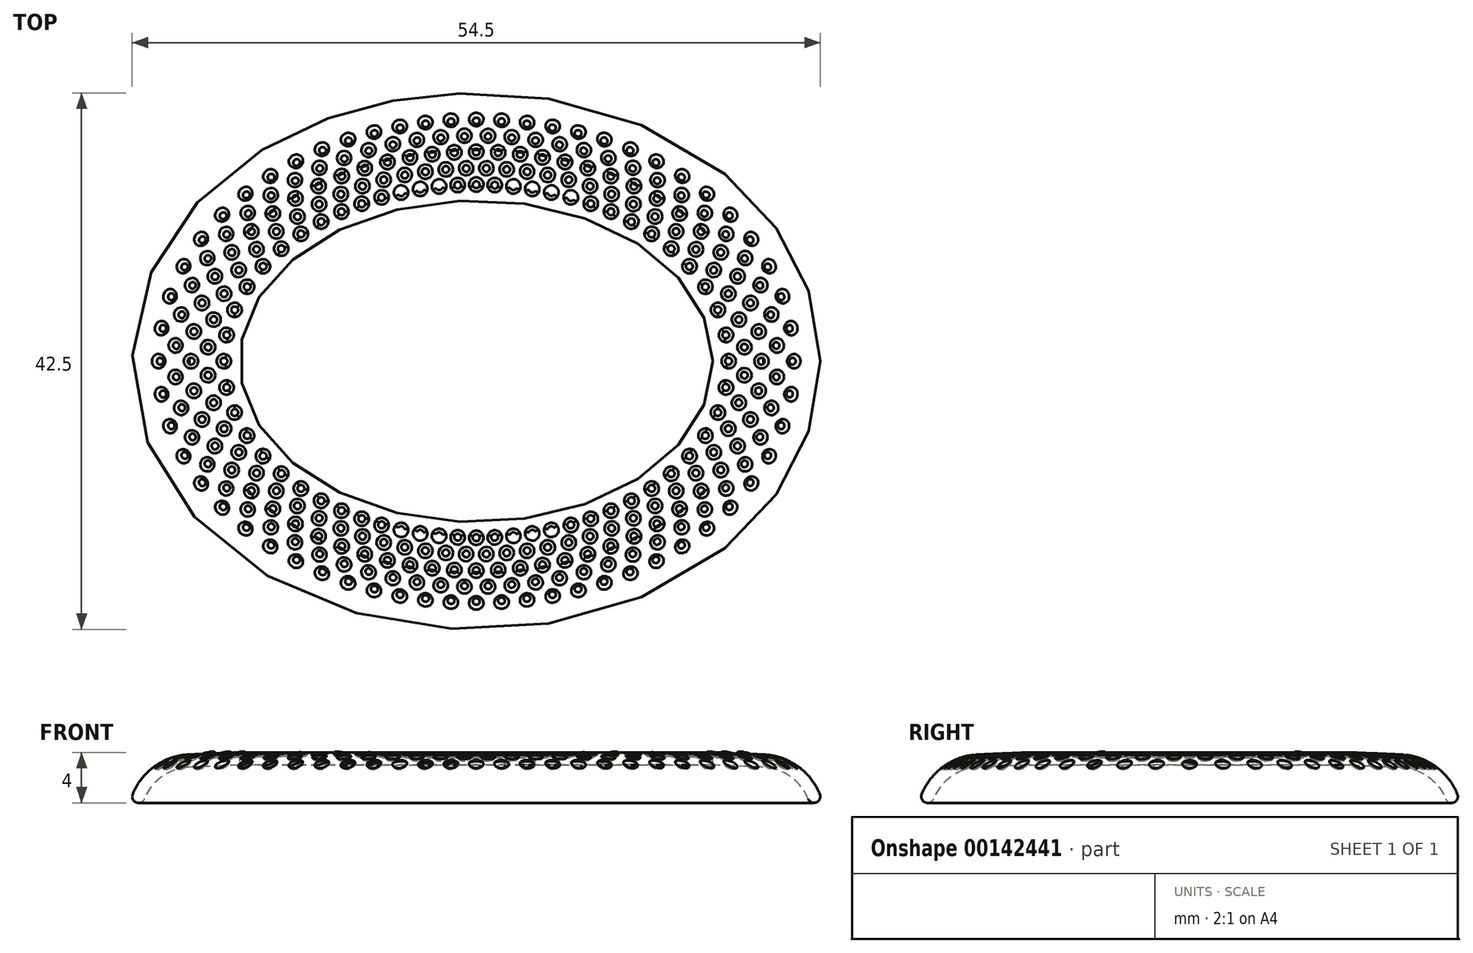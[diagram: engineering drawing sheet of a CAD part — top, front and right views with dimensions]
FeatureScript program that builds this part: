
annotation { "Feature Type Name" : "Feature", "Feature Type Description" : "" }
export const myFeature = defineFeature(function(context is Context, id is Id, definition is map)
    precondition{}
    {
        {
            var Q0;
            Q0=qCreatedBy(makeId("Top.planeOp"),FACE);
            var sketch = newSketch(context, id + "F0", { "sketchPlane" : qUnion([Q0])});
            skEllipse(sketch, "E0", {"center": v(0, 0) * mm, "majorRadius": 12.75 * mm, "minorRadius": 18.75 * mm, "majorAxis": v(0, -1)});
            skFitSpline(sketch, "E1.0", {"points": [v(27.13, -2.49) * mm, v(27.31, 0) * mm, v(27.13, 2.49) * mm, v(26.6, 4.9) * mm, v(25.75, 7.19) * mm, v(24.63, 9.32) * mm, v(23.26, 11.3) * mm, v(21.15, 13.67) * mm, v(18.12, 16.16) * mm, v(14.7, 18.07) * mm, v(11.75, 19.26) * mm, v(8.73, 20.23) * mm, v(5.6, 20.87) * mm, v(2.42, 21.2) * mm, v(0, 21.28) * mm, v(-2.42, 21.2) * mm, v(-5.6, 20.87) * mm, v(-8.73, 20.23) * mm, v(-11.75, 19.26) * mm, v(-14.7, 18.07) * mm, v(-18.12, 16.16) * mm, v(-21.15, 13.67) * mm, v(-23.26, 11.3) * mm, v(-24.63, 9.32) * mm, v(-25.75, 7.19) * mm, v(-26.6, 4.9) * mm, v(-27.13, 2.49) * mm, v(-27.31, 0) * mm, v(-27.13, -2.49) * mm, v(-26.6, -4.9) * mm, v(-25.75, -7.19) * mm, v(-24.63, -9.32) * mm, v(-23.26, -11.3) * mm, v(-21.15, -13.67) * mm, v(-18.12, -16.16) * mm, v(-14.7, -18.07) * mm, v(-11.75, -19.26) * mm, v(-8.73, -20.23) * mm, v(-5.6, -20.87) * mm, v(-2.42, -21.2) * mm, v(0, -21.28) * mm, v(2.42, -21.2) * mm, v(5.6, -20.87) * mm, v(8.73, -20.23) * mm, v(11.75, -19.26) * mm, v(14.7, -18.07) * mm, v(18.12, -16.16) * mm, v(21.15, -13.67) * mm, v(23.26, -11.3) * mm, v(24.63, -9.32) * mm, v(25.75, -7.19) * mm, v(26.6, -4.9) * mm, v(27.13, -2.49) * mm, v(27.31, 0) * mm, v(27.13, 2.49) * mm, v(27.13, -2.49) * mm]});
            skLineSegment(sketch, "E2", {"start": v(18.75, 0) * mm, "end": v(27.25, 0) * mm, "construction": true});
            skSolve(sketch);
        }
        {
            var Q0;
            Q0=qCreatedBy(makeId("Front.planeOp"),FACE);
            var sketch = newSketch(context, id + "F1", { "sketchPlane" : qUnion([Q0])});
            skLineSegment(sketch, "E3", {"start": v(18.75, 0) * mm, "end": v(18.75, -1) * mm, "construction": true});
            skLineSegment(sketch, "E4", {"start": v(18.75, -4) * mm, "end": v(27.25, -4) * mm, "construction": true});
            skLineSegment(sketch, "E5", {"start": v(18.75, 0) * mm, "end": v(22.75, -0.17) * mm});
            skLineSegment(sketch, "E6", {"start": v(18.75, 0) * mm, "end": v(18.75, -1) * mm});
            skArc(sketch, "E7", {"start": v(27.21, -3.31) * mm, "mid": v(25.44, -1.09) * mm, "end": v(22.75, -0.17) * mm});
            skPoint(sketch, "E7.third.point", {"position": v(22.75, -0.17) * mm});
            skArc(sketch, "E8.0", {"start": v(26.29, -3.69) * mm, "mid": v(24.89, -1.91) * mm, "end": v(22.75, -1.18) * mm});
            skLineSegment(sketch, "E8.1", {"start": v(18.75, -1) * mm, "end": v(22.75, -1.18) * mm});
            skLineSegment(sketch, "E9.trimOffspring", {"start": v(18.75, -1.3) * mm, "end": v(18.75, -4) * mm, "construction": true});
            skArc(sketch, "E10", {"start": v(26.29, -3.69) * mm, "mid": v(26.94, -3.96) * mm, "end": v(27.21, -3.31) * mm});
            skLineSegment(sketch, "E11", {"start": v(27.25, -4) * mm, "end": v(27.25, 0) * mm, "construction": true});
            skSolve(sketch);
        }
        {
            var Q0;
            Q0=qCreatedBy(makeId("Top.planeOp"),FACE);
            var sketch = newSketch(context, id + "F2", { "sketchPlane" : qUnion([Q0])});
            skFitSpline(sketch, "E12.0", {"points": [v(19.93, -1.44) * mm, v(20.03, 0) * mm, v(19.93, 1.44) * mm, v(19.52, 3.32) * mm, v(18.71, 5.12) * mm, v(17.55, 6.8) * mm, v(16.15, 8.37) * mm, v(14.04, 10.12) * mm, v(11.52, 11.53) * mm, v(9.28, 12.44) * mm, v(6.93, 13.2) * mm, v(4.47, 13.7) * mm, v(1.93, 13.96) * mm, v(0, 14.02) * mm, v(-1.93, 13.96) * mm, v(-4.47, 13.7) * mm, v(-6.93, 13.2) * mm, v(-9.28, 12.44) * mm, v(-11.52, 11.53) * mm, v(-14.04, 10.12) * mm, v(-16.15, 8.37) * mm, v(-17.55, 6.8) * mm, v(-18.71, 5.12) * mm, v(-19.52, 3.32) * mm, v(-19.93, 1.44) * mm, v(-20.03, 0) * mm, v(-19.93, -1.44) * mm, v(-19.52, -3.32) * mm, v(-18.71, -5.12) * mm, v(-17.55, -6.8) * mm, v(-16.15, -8.37) * mm, v(-14.04, -10.12) * mm, v(-11.52, -11.53) * mm, v(-9.28, -12.44) * mm, v(-6.93, -13.2) * mm, v(-4.47, -13.7) * mm, v(-1.93, -13.96) * mm, v(0, -14.02) * mm, v(1.93, -13.96) * mm, v(4.47, -13.7) * mm, v(6.93, -13.2) * mm, v(9.28, -12.44) * mm, v(11.52, -11.53) * mm, v(14.04, -10.12) * mm, v(16.15, -8.37) * mm, v(17.55, -6.8) * mm, v(18.71, -5.12) * mm, v(19.52, -3.32) * mm, v(19.93, -1.44) * mm, v(20.03, 0) * mm, v(19.93, 1.44) * mm, v(19.93, -1.44) * mm], "construction": true});
            skFitSpline(sketch, "E13.0", {"points": [v(21.22, -1.63) * mm, v(21.34, 0) * mm, v(21.22, 1.63) * mm, v(20.76, 3.75) * mm, v(19.86, 5.75) * mm, v(18.57, 7.6) * mm, v(17.05, 9.32) * mm, v(14.77, 11.2) * mm, v(12.09, 12.7) * mm, v(9.72, 13.66) * mm, v(7.26, 14.45) * mm, v(4.67, 14.99) * mm, v(2.02, 15.25) * mm, v(0, 15.32) * mm, v(-2.02, 15.25) * mm, v(-4.67, 14.99) * mm, v(-7.26, 14.45) * mm, v(-9.72, 13.66) * mm, v(-12.09, 12.7) * mm, v(-14.77, 11.2) * mm, v(-17.05, 9.32) * mm, v(-18.57, 7.6) * mm, v(-19.86, 5.75) * mm, v(-20.76, 3.75) * mm, v(-21.22, 1.63) * mm, v(-21.34, 0) * mm, v(-21.22, -1.63) * mm, v(-20.76, -3.75) * mm, v(-19.86, -5.75) * mm, v(-18.57, -7.6) * mm, v(-17.05, -9.32) * mm, v(-14.77, -11.2) * mm, v(-12.09, -12.7) * mm, v(-9.72, -13.66) * mm, v(-7.26, -14.45) * mm, v(-4.67, -14.99) * mm, v(-2.02, -15.25) * mm, v(0, -15.32) * mm, v(2.02, -15.25) * mm, v(4.67, -14.99) * mm, v(7.26, -14.45) * mm, v(9.72, -13.66) * mm, v(12.09, -12.7) * mm, v(14.77, -11.2) * mm, v(17.05, -9.32) * mm, v(18.57, -7.6) * mm, v(19.86, -5.75) * mm, v(20.76, -3.75) * mm, v(21.22, -1.63) * mm, v(21.34, 0) * mm, v(21.22, 1.63) * mm, v(21.22, -1.63) * mm], "construction": true});
            skFitSpline(sketch, "E14.0", {"points": [v(22.51, -1.81) * mm, v(22.64, 0) * mm, v(22.51, 1.81) * mm, v(22, 4.17) * mm, v(21, 6.4) * mm, v(19.6, 8.4) * mm, v(17.95, 10.27) * mm, v(15.5, 12.28) * mm, v(12.65, 13.87) * mm, v(10.16, 14.89) * mm, v(7.58, 15.72) * mm, v(4.88, 16.27) * mm, v(2.1, 16.55) * mm, v(0, 16.62) * mm, v(-2.1, 16.55) * mm, v(-4.88, 16.27) * mm, v(-7.58, 15.72) * mm, v(-10.16, 14.89) * mm, v(-12.65, 13.87) * mm, v(-15.5, 12.28) * mm, v(-17.95, 10.27) * mm, v(-19.6, 8.4) * mm, v(-21, 6.4) * mm, v(-22, 4.17) * mm, v(-22.51, 1.81) * mm, v(-22.64, 0) * mm, v(-22.51, -1.81) * mm, v(-22, -4.17) * mm, v(-21, -6.4) * mm, v(-19.6, -8.4) * mm, v(-17.95, -10.27) * mm, v(-15.5, -12.28) * mm, v(-12.65, -13.87) * mm, v(-10.16, -14.89) * mm, v(-7.58, -15.72) * mm, v(-4.88, -16.27) * mm, v(-2.1, -16.55) * mm, v(0, -16.62) * mm, v(2.1, -16.55) * mm, v(4.88, -16.27) * mm, v(7.58, -15.72) * mm, v(10.16, -14.89) * mm, v(12.65, -13.87) * mm, v(15.5, -12.28) * mm, v(17.95, -10.27) * mm, v(19.6, -8.4) * mm, v(21, -6.4) * mm, v(22, -4.17) * mm, v(22.51, -1.81) * mm, v(22.64, 0) * mm, v(22.51, 1.81) * mm, v(22.51, -1.81) * mm], "construction": true});
            skFitSpline(sketch, "E15.0", {"points": [v(23.8, -2) * mm, v(23.95, 0) * mm, v(23.8, 2) * mm, v(23.23, 4.6) * mm, v(22.14, 7.03) * mm, v(20.62, 9.21) * mm, v(18.84, 11.22) * mm, v(16.24, 13.37) * mm, v(13.22, 15.04) * mm, v(10.6, 16.11) * mm, v(7.9, 16.98) * mm, v(5.08, 17.56) * mm, v(2.2, 17.85) * mm, v(0, 17.92) * mm, v(-2.2, 17.85) * mm, v(-5.08, 17.56) * mm, v(-7.9, 16.98) * mm, v(-10.6, 16.11) * mm, v(-13.22, 15.04) * mm, v(-16.24, 13.37) * mm, v(-18.84, 11.22) * mm, v(-20.62, 9.21) * mm, v(-22.14, 7.03) * mm, v(-23.23, 4.6) * mm, v(-23.8, 2) * mm, v(-23.95, 0) * mm, v(-23.8, -2) * mm, v(-23.23, -4.6) * mm, v(-22.14, -7.03) * mm, v(-20.62, -9.21) * mm, v(-18.84, -11.22) * mm, v(-16.24, -13.37) * mm, v(-13.22, -15.04) * mm, v(-10.6, -16.11) * mm, v(-7.9, -16.98) * mm, v(-5.08, -17.56) * mm, v(-2.2, -17.85) * mm, v(0, -17.92) * mm, v(2.2, -17.85) * mm, v(5.08, -17.56) * mm, v(7.9, -16.98) * mm, v(10.6, -16.11) * mm, v(13.22, -15.04) * mm, v(16.24, -13.37) * mm, v(18.84, -11.22) * mm, v(20.62, -9.21) * mm, v(22.14, -7.03) * mm, v(23.23, -4.6) * mm, v(23.8, -2) * mm, v(23.95, 0) * mm, v(23.8, 2) * mm, v(23.8, -2) * mm], "construction": true});
            skFitSpline(sketch, "E16.0", {"points": [v(25.1, -2.2) * mm, v(25.25, 0) * mm, v(25.1, 2.2) * mm, v(24.47, 5.03) * mm, v(22.99, 8.32) * mm, v(20.3, 11.72) * mm, v(16.97, 14.45) * mm, v(13.8, 16.22) * mm, v(11.05, 17.33) * mm, v(8.22, 18.24) * mm, v(5.28, 18.85) * mm, v(2.28, 19.15) * mm, v(0, 19.23) * mm, v(-2.28, 19.15) * mm, v(-5.28, 18.85) * mm, v(-8.22, 18.24) * mm, v(-11.05, 17.33) * mm, v(-13.8, 16.22) * mm, v(-16.97, 14.45) * mm, v(-20.3, 11.72) * mm, v(-22.99, 8.32) * mm, v(-24.47, 5.03) * mm, v(-25.1, 2.2) * mm, v(-25.25, 0) * mm, v(-25.1, -2.2) * mm, v(-24.47, -5.03) * mm, v(-22.99, -8.32) * mm, v(-20.3, -11.72) * mm, v(-16.97, -14.45) * mm, v(-13.8, -16.22) * mm, v(-11.05, -17.33) * mm, v(-8.22, -18.24) * mm, v(-5.28, -18.85) * mm, v(-2.28, -19.15) * mm, v(0, -19.23) * mm, v(2.28, -19.15) * mm, v(5.28, -18.85) * mm, v(8.22, -18.24) * mm, v(11.05, -17.33) * mm, v(13.8, -16.22) * mm, v(16.97, -14.45) * mm, v(20.3, -11.72) * mm, v(22.99, -8.32) * mm, v(24.47, -5.03) * mm, v(25.1, -2.2) * mm, v(25.25, 0) * mm, v(25.1, 2.2) * mm, v(25.1, -2.2) * mm], "construction": true});
            skCircle(sketch, "E17", {"center": v(0, 14) * mm, "radius": 0.57 * mm});
            skCircle(sketch, "E18", {"center": v(0, 16.6) * mm, "radius": 0.57 * mm});
            skCircle(sketch, "E19", {"center": v(0, 19.2) * mm, "radius": 0.57 * mm});
            skLineSegment(sketch, "E20", {"start": v(0, 0) * mm, "end": v(0, 14) * mm, "construction": true});
            skLineSegment(sketch, "E21", {"start": v(0, 14) * mm, "end": v(0, 16.6) * mm, "construction": true});
            skLineSegment(sketch, "E22", {"start": v(0, 16.6) * mm, "end": v(0, 19.2) * mm, "construction": true});
            skLineSegment(sketch, "E23", {"start": v(0, 0) * mm, "end": v(0.8, 15.29) * mm, "construction": true});
            skLineSegment(sketch, "E24", {"start": v(0.8, 15.29) * mm, "end": v(0.94, 17.89) * mm, "construction": true});
            skCircle(sketch, "E25", {"center": v(0.94, 17.89) * mm, "radius": 0.57 * mm});
            skCircle(sketch, "E26", {"center": v(0.8, 15.29) * mm, "radius": 0.57 * mm});
            skLineSegment(sketch, "E27", {"start": v(0, 0) * mm, "end": v(1.47, 13.96) * mm, "construction": true});
            skLineSegment(sketch, "E28", {"start": v(1.47, 13.96) * mm, "end": v(1.74, 16.55) * mm, "construction": true});
            skLineSegment(sketch, "E29", {"start": v(1.74, 16.55) * mm, "end": v(2.01, 19.14) * mm, "construction": true});
            skLineSegment(sketch, "E30", {"start": v(0, 0) * mm, "end": v(2.4, 15.2) * mm, "construction": true});
            skLineSegment(sketch, "E31", {"start": v(2.4, 15.2) * mm, "end": v(2.82, 17.78) * mm, "construction": true});
            skLineSegment(sketch, "E32", {"start": v(0, 0) * mm, "end": v(2.94, 13.85) * mm, "construction": true});
            skLineSegment(sketch, "E33", {"start": v(2.94, 13.85) * mm, "end": v(3.49, 16.4) * mm, "construction": true});
            skLineSegment(sketch, "E34", {"start": v(3.49, 16.4) * mm, "end": v(4.03, 18.96) * mm, "construction": true});
            skLineSegment(sketch, "E35", {"start": v(0, 0) * mm, "end": v(4.03, 15.03) * mm, "construction": true});
            skLineSegment(sketch, "E36", {"start": v(4.03, 15.03) * mm, "end": v(4.7, 17.56) * mm, "construction": true});
            skLineSegment(sketch, "E37", {"start": v(0, 0) * mm, "end": v(4.44, 13.65) * mm, "construction": true});
            skLineSegment(sketch, "E38", {"start": v(4.44, 13.65) * mm, "end": v(5.25, 16.16) * mm, "construction": true});
            skLineSegment(sketch, "E39", {"start": v(5.25, 16.16) * mm, "end": v(6.06, 18.65) * mm, "construction": true});
            skLineSegment(sketch, "E40", {"start": v(0, 0) * mm, "end": v(5.66, 14.76) * mm, "construction": true});
            skLineSegment(sketch, "E41", {"start": v(5.66, 14.76) * mm, "end": v(6.6, 17.22) * mm, "construction": true});
            skLineSegment(sketch, "E42", {"start": v(0, 0) * mm, "end": v(5.95, 13.37) * mm, "construction": true});
            skLineSegment(sketch, "E43", {"start": v(5.95, 13.37) * mm, "end": v(7.03, 15.8) * mm, "construction": true});
            skLineSegment(sketch, "E44", {"start": v(7.03, 15.8) * mm, "end": v(8.1, 18.2) * mm, "construction": true});
            skLineSegment(sketch, "E45", {"start": v(0, 0) * mm, "end": v(7.33, 14.38) * mm, "construction": true});
            skLineSegment(sketch, "E46", {"start": v(7.33, 14.38) * mm, "end": v(8.53, 16.75) * mm, "construction": true});
            skLineSegment(sketch, "E47", {"start": v(0, 0) * mm, "end": v(7.5, 12.99) * mm, "construction": true});
            skLineSegment(sketch, "E48", {"start": v(7.5, 12.99) * mm, "end": v(8.84, 15.3) * mm, "construction": true});
            skLineSegment(sketch, "E49", {"start": v(8.84, 15.3) * mm, "end": v(10.17, 17.6) * mm, "construction": true});
            skLineSegment(sketch, "E50", {"start": v(0, 0) * mm, "end": v(9.02, 13.88) * mm, "construction": true});
            skLineSegment(sketch, "E51", {"start": v(9.02, 13.88) * mm, "end": v(10.47, 16.13) * mm, "construction": true});
            skLineSegment(sketch, "E52", {"start": v(0, 0) * mm, "end": v(9.07, 12.49) * mm, "construction": true});
            skLineSegment(sketch, "E53", {"start": v(9.07, 12.49) * mm, "end": v(10.66, 14.67) * mm, "construction": true});
            skLineSegment(sketch, "E54", {"start": v(10.66, 14.67) * mm, "end": v(12.24, 16.84) * mm, "construction": true});
            skLineSegment(sketch, "E55", {"start": v(0, 0) * mm, "end": v(10.73, 13.25) * mm, "construction": true});
            skLineSegment(sketch, "E56", {"start": v(10.73, 13.25) * mm, "end": v(12.43, 15.34) * mm, "construction": true});
            skLineSegment(sketch, "E57", {"start": v(0, 0) * mm, "end": v(10.67, 11.86) * mm, "construction": true});
            skLineSegment(sketch, "E58", {"start": v(10.67, 11.86) * mm, "end": v(12.5, 13.88) * mm, "construction": true});
            skLineSegment(sketch, "E59", {"start": v(12.5, 13.88) * mm, "end": v(14.3, 15.88) * mm, "construction": true});
            skLineSegment(sketch, "E60", {"start": v(0, 0) * mm, "end": v(12.45, 12.45) * mm, "construction": true});
            skLineSegment(sketch, "E61", {"start": v(12.45, 12.45) * mm, "end": v(14.37, 14.37) * mm, "construction": true});
            skLineSegment(sketch, "E62", {"start": v(0, 0) * mm, "end": v(12.29, 11.07) * mm, "construction": true});
            skLineSegment(sketch, "E63", {"start": v(12.29, 11.07) * mm, "end": v(14.33, 12.9) * mm, "construction": true});
            skLineSegment(sketch, "E64", {"start": v(14.33, 12.9) * mm, "end": v(16.34, 14.71) * mm, "construction": true});
            skLineSegment(sketch, "E65", {"start": v(0, 0) * mm, "end": v(14.17, 11.47) * mm, "construction": true});
            skLineSegment(sketch, "E66", {"start": v(14.17, 11.47) * mm, "end": v(16.28, 13.19) * mm, "construction": true});
            skLineSegment(sketch, "E67", {"start": v(0, 0) * mm, "end": v(13.9, 10.1) * mm, "construction": true});
            skLineSegment(sketch, "E68", {"start": v(13.9, 10.1) * mm, "end": v(16.11, 11.7) * mm, "construction": true});
            skLineSegment(sketch, "E69", {"start": v(16.11, 11.7) * mm, "end": v(18.3, 13.3) * mm, "construction": true});
            skLineSegment(sketch, "E70", {"start": v(0, 0) * mm, "end": v(15.84, 10.28) * mm, "construction": true});
            skLineSegment(sketch, "E71", {"start": v(15.84, 10.28) * mm, "end": v(18.12, 11.77) * mm, "construction": true});
            skLineSegment(sketch, "E72", {"start": v(0, 0) * mm, "end": v(15.45, 8.92) * mm, "construction": true});
            skLineSegment(sketch, "E73", {"start": v(15.45, 8.92) * mm, "end": v(17.82, 10.29) * mm, "construction": true});
            skLineSegment(sketch, "E74", {"start": v(17.82, 10.29) * mm, "end": v(20.16, 11.64) * mm, "construction": true});
            skLineSegment(sketch, "E75", {"start": v(0, 0) * mm, "end": v(17.4, 8.87) * mm, "construction": true});
            skLineSegment(sketch, "E76", {"start": v(17.4, 8.87) * mm, "end": v(19.82, 10.1) * mm, "construction": true});
            skLineSegment(sketch, "E77", {"start": v(0, 0) * mm, "end": v(16.9, 7.52) * mm, "construction": true});
            skLineSegment(sketch, "E78", {"start": v(16.9, 7.52) * mm, "end": v(19.37, 8.63) * mm, "construction": true});
            skLineSegment(sketch, "E79", {"start": v(19.37, 8.63) * mm, "end": v(21.82, 9.72) * mm, "construction": true});
            skLineSegment(sketch, "E80", {"start": v(0, 0) * mm, "end": v(18.82, 7.22) * mm, "construction": true});
            skLineSegment(sketch, "E81", {"start": v(18.82, 7.22) * mm, "end": v(21.32, 8.18) * mm, "construction": true});
            skLineSegment(sketch, "E82", {"start": v(0, 0) * mm, "end": v(18.16, 5.9) * mm, "construction": true});
            skLineSegment(sketch, "E83", {"start": v(18.16, 5.9) * mm, "end": v(20.7, 6.73) * mm, "construction": true});
            skLineSegment(sketch, "E84", {"start": v(20.7, 6.73) * mm, "end": v(23.23, 7.55) * mm, "construction": true});
            skLineSegment(sketch, "E85", {"start": v(0, 0) * mm, "end": v(19.98, 5.35) * mm, "construction": true});
            skLineSegment(sketch, "E86", {"start": v(19.98, 5.35) * mm, "end": v(22.54, 6.04) * mm, "construction": true});
            skLineSegment(sketch, "E87", {"start": v(0, 0) * mm, "end": v(19.15, 4.07) * mm, "construction": true});
            skLineSegment(sketch, "E88", {"start": v(19.15, 4.07) * mm, "end": v(21.73, 4.62) * mm, "construction": true});
            skLineSegment(sketch, "E89", {"start": v(21.73, 4.62) * mm, "end": v(24.3, 5.16) * mm, "construction": true});
            skLineSegment(sketch, "E90", {"start": v(0, 0) * mm, "end": v(20.8, 3.3) * mm, "construction": true});
            skLineSegment(sketch, "E91", {"start": v(20.8, 3.3) * mm, "end": v(23.4, 3.7) * mm, "construction": true});
            skLineSegment(sketch, "E92", {"start": v(0, 0) * mm, "end": v(19.78, 2.08) * mm, "construction": true});
            skLineSegment(sketch, "E93", {"start": v(19.78, 2.08) * mm, "end": v(22.38, 2.35) * mm, "construction": true});
            skLineSegment(sketch, "E94", {"start": v(22.38, 2.35) * mm, "end": v(24.97, 2.62) * mm, "construction": true});
            skLineSegment(sketch, "E95", {"start": v(0, 0) * mm, "end": v(21.24, 1.11) * mm, "construction": true});
            skLineSegment(sketch, "E96", {"start": v(21.24, 1.11) * mm, "end": v(23.84, 1.25) * mm, "construction": true});
            skLineSegment(sketch, "E97", {"start": v(0, 0) * mm, "end": v(20, 0) * mm, "construction": true});
            skLineSegment(sketch, "E98", {"start": v(20, 0) * mm, "end": v(22.6, 0) * mm, "construction": true});
            skLineSegment(sketch, "E99", {"start": v(22.6, 0) * mm, "end": v(25.2, 0) * mm, "construction": true});
            skCircle(sketch, "E100", {"center": v(2.01, 19.14) * mm, "radius": 0.57 * mm});
            skCircle(sketch, "E101", {"center": v(4.03, 18.96) * mm, "radius": 0.57 * mm});
            skCircle(sketch, "E102", {"center": v(6.06, 18.65) * mm, "radius": 0.57 * mm});
            skCircle(sketch, "E103", {"center": v(8.1, 18.2) * mm, "radius": 0.57 * mm});
            skCircle(sketch, "E104", {"center": v(10.17, 17.6) * mm, "radius": 0.57 * mm});
            skCircle(sketch, "E105", {"center": v(12.24, 16.84) * mm, "radius": 0.57 * mm});
            skCircle(sketch, "E106", {"center": v(14.3, 15.88) * mm, "radius": 0.57 * mm});
            skCircle(sketch, "E107", {"center": v(16.34, 14.71) * mm, "radius": 0.57 * mm});
            skCircle(sketch, "E108", {"center": v(18.3, 13.3) * mm, "radius": 0.57 * mm});
            skCircle(sketch, "E109", {"center": v(20.16, 11.64) * mm, "radius": 0.57 * mm});
            skCircle(sketch, "E110", {"center": v(21.82, 9.72) * mm, "radius": 0.57 * mm});
            skCircle(sketch, "E111", {"center": v(23.23, 7.55) * mm, "radius": 0.57 * mm});
            skCircle(sketch, "E112", {"center": v(24.3, 5.16) * mm, "radius": 0.57 * mm});
            skCircle(sketch, "E113", {"center": v(24.97, 2.62) * mm, "radius": 0.57 * mm});
            skCircle(sketch, "E114", {"center": v(25.2, 0) * mm, "radius": 0.57 * mm});
            skCircle(sketch, "E115", {"center": v(22.6, 0) * mm, "radius": 0.57 * mm});
            skCircle(sketch, "E116", {"center": v(20, 0) * mm, "radius": 0.57 * mm});
            skCircle(sketch, "E117", {"center": v(22.38, 2.35) * mm, "radius": 0.57 * mm});
            skCircle(sketch, "E118", {"center": v(19.78, 2.08) * mm, "radius": 0.57 * mm});
            skCircle(sketch, "E119", {"center": v(19.15, 4.07) * mm, "radius": 0.57 * mm});
            skCircle(sketch, "E120", {"center": v(21.73, 4.62) * mm, "radius": 0.57 * mm});
            skCircle(sketch, "E121", {"center": v(20.7, 6.73) * mm, "radius": 0.57 * mm});
            skCircle(sketch, "E122", {"center": v(18.16, 5.9) * mm, "radius": 0.57 * mm});
            skCircle(sketch, "E123", {"center": v(19.37, 8.63) * mm, "radius": 0.57 * mm});
            skCircle(sketch, "E124", {"center": v(16.9, 7.52) * mm, "radius": 0.57 * mm});
            skCircle(sketch, "E125", {"center": v(17.82, 10.29) * mm, "radius": 0.57 * mm});
            skCircle(sketch, "E126", {"center": v(15.45, 8.92) * mm, "radius": 0.57 * mm});
            skCircle(sketch, "E127", {"center": v(16.11, 11.7) * mm, "radius": 0.57 * mm});
            skCircle(sketch, "E128", {"center": v(13.9, 10.1) * mm, "radius": 0.57 * mm});
            skCircle(sketch, "E129", {"center": v(14.33, 12.9) * mm, "radius": 0.57 * mm});
            skCircle(sketch, "E130", {"center": v(12.29, 11.07) * mm, "radius": 0.57 * mm});
            skCircle(sketch, "E131", {"center": v(12.5, 13.88) * mm, "radius": 0.57 * mm});
            skCircle(sketch, "E132", {"center": v(10.67, 11.86) * mm, "radius": 0.57 * mm});
            skCircle(sketch, "E133", {"center": v(9.07, 12.49) * mm, "radius": 0.57 * mm});
            skCircle(sketch, "E134", {"center": v(10.66, 14.67) * mm, "radius": 0.57 * mm});
            skCircle(sketch, "E135", {"center": v(8.84, 15.3) * mm, "radius": 0.57 * mm});
            skCircle(sketch, "E136", {"center": v(7.03, 15.8) * mm, "radius": 0.57 * mm});
            skCircle(sketch, "E137", {"center": v(7.5, 12.99) * mm, "radius": 0.57 * mm});
            skCircle(sketch, "E138", {"center": v(5.95, 13.37) * mm, "radius": 0.57 * mm});
            skCircle(sketch, "E139", {"center": v(4.44, 13.65) * mm, "radius": 0.57 * mm});
            skCircle(sketch, "E140", {"center": v(2.94, 13.85) * mm, "radius": 0.57 * mm});
            skCircle(sketch, "E141", {"center": v(1.47, 13.96) * mm, "radius": 0.57 * mm});
            skCircle(sketch, "E142", {"center": v(1.74, 16.55) * mm, "radius": 0.57 * mm});
            skCircle(sketch, "E143", {"center": v(3.49, 16.4) * mm, "radius": 0.57 * mm});
            skCircle(sketch, "E144", {"center": v(5.25, 16.16) * mm, "radius": 0.57 * mm});
            skCircle(sketch, "E145", {"center": v(2.82, 17.78) * mm, "radius": 0.57 * mm});
            skCircle(sketch, "E146", {"center": v(4.7, 17.56) * mm, "radius": 0.57 * mm});
            skCircle(sketch, "E147", {"center": v(6.6, 17.22) * mm, "radius": 0.57 * mm});
            skCircle(sketch, "E148", {"center": v(8.53, 16.75) * mm, "radius": 0.57 * mm});
            skCircle(sketch, "E149", {"center": v(10.47, 16.13) * mm, "radius": 0.57 * mm});
            skCircle(sketch, "E150", {"center": v(12.43, 15.34) * mm, "radius": 0.57 * mm});
            skCircle(sketch, "E151", {"center": v(14.37, 14.37) * mm, "radius": 0.57 * mm});
            skCircle(sketch, "E152", {"center": v(16.28, 13.19) * mm, "radius": 0.57 * mm});
            skCircle(sketch, "E153", {"center": v(18.12, 11.77) * mm, "radius": 0.57 * mm});
            skCircle(sketch, "E154", {"center": v(19.82, 10.1) * mm, "radius": 0.57 * mm});
            skCircle(sketch, "E155", {"center": v(21.32, 8.18) * mm, "radius": 0.57 * mm});
            skCircle(sketch, "E156", {"center": v(22.54, 6.04) * mm, "radius": 0.57 * mm});
            skCircle(sketch, "E157", {"center": v(23.4, 3.7) * mm, "radius": 0.57 * mm});
            skCircle(sketch, "E158", {"center": v(23.84, 1.25) * mm, "radius": 0.57 * mm});
            skCircle(sketch, "E159", {"center": v(2.4, 15.2) * mm, "radius": 0.57 * mm});
            skCircle(sketch, "E160", {"center": v(4.03, 15.03) * mm, "radius": 0.57 * mm});
            skCircle(sketch, "E161", {"center": v(5.66, 14.76) * mm, "radius": 0.57 * mm});
            skCircle(sketch, "E162", {"center": v(7.33, 14.38) * mm, "radius": 0.57 * mm});
            skCircle(sketch, "E163", {"center": v(9.02, 13.88) * mm, "radius": 0.57 * mm});
            skCircle(sketch, "E164", {"center": v(10.73, 13.25) * mm, "radius": 0.57 * mm});
            skCircle(sketch, "E165", {"center": v(12.45, 12.45) * mm, "radius": 0.57 * mm});
            skCircle(sketch, "E166", {"center": v(14.17, 11.47) * mm, "radius": 0.57 * mm});
            skCircle(sketch, "E167", {"center": v(15.84, 10.28) * mm, "radius": 0.57 * mm});
            skCircle(sketch, "E168", {"center": v(17.4, 8.87) * mm, "radius": 0.57 * mm});
            skCircle(sketch, "E169", {"center": v(18.82, 7.22) * mm, "radius": 0.57 * mm});
            skCircle(sketch, "E170", {"center": v(19.98, 5.35) * mm, "radius": 0.57 * mm});
            skCircle(sketch, "E171", {"center": v(20.8, 3.3) * mm, "radius": 0.57 * mm});
            skCircle(sketch, "E172", {"center": v(21.24, 1.11) * mm, "radius": 0.57 * mm});
            skCircle(sketch, "E173.MirrorC", {"center": v(-10.66, 14.67) * mm, "radius": 0.57 * mm});
            skCircle(sketch, "E174.MirrorC", {"center": v(-12.43, 15.34) * mm, "radius": 0.57 * mm});
            skLineSegment(sketch, "E175.MirrorCS", {"start": v(0, 0) * mm, "end": v(-1.47, 13.96) * mm, "construction": true});
            skCircle(sketch, "E176.MirrorC", {"center": v(-14.17, 11.47) * mm, "radius": 0.57 * mm});
            skLineSegment(sketch, "E177.MirrorCS", {"start": v(-19.98, 5.35) * mm, "end": v(-22.54, 6.04) * mm, "construction": true});
            skLineSegment(sketch, "E178.MirrorCS", {"start": v(0, 0) * mm, "end": v(-15.84, 10.28) * mm, "construction": true});
            skCircle(sketch, "E179.MirrorC", {"center": v(-0.8, 15.29) * mm, "radius": 0.57 * mm});
            skCircle(sketch, "E180.MirrorC", {"center": v(-6.06, 18.65) * mm, "radius": 0.57 * mm});
            skCircle(sketch, "E181.MirrorC", {"center": v(-19.78, 2.08) * mm, "radius": 0.57 * mm});
            skCircle(sketch, "E182.MirrorC", {"center": v(-0.94, 17.89) * mm, "radius": 0.57 * mm});
            skLineSegment(sketch, "E183.MirrorCS", {"start": v(-4.44, 13.65) * mm, "end": v(-5.25, 16.16) * mm, "construction": true});
            skLineSegment(sketch, "E184.MirrorCS", {"start": v(-10.66, 14.67) * mm, "end": v(-12.24, 16.84) * mm, "construction": true});
            skCircle(sketch, "E185.MirrorC", {"center": v(-9.07, 12.49) * mm, "radius": 0.57 * mm});
            skCircle(sketch, "E186.MirrorC", {"center": v(-10.47, 16.13) * mm, "radius": 0.57 * mm});
            skCircle(sketch, "E187.MirrorC", {"center": v(-12.45, 12.45) * mm, "radius": 0.57 * mm});
            skLineSegment(sketch, "E188.MirrorCS", {"start": v(-16.11, 11.7) * mm, "end": v(-18.3, 13.3) * mm, "construction": true});
            skLineSegment(sketch, "E189.MirrorCS", {"start": v(0, 0) * mm, "end": v(-19.98, 5.35) * mm, "construction": true});
            skCircle(sketch, "E190.MirrorC", {"center": v(-4.03, 18.96) * mm, "radius": 0.57 * mm});
            skLineSegment(sketch, "E191.MirrorCS", {"start": v(0, 0) * mm, "end": v(-10.67, 11.86) * mm, "construction": true});
            skCircle(sketch, "E192.MirrorC", {"center": v(-22.38, 2.35) * mm, "radius": 0.57 * mm});
            skLineSegment(sketch, "E193.MirrorCS", {"start": v(0, 0) * mm, "end": v(-4.44, 13.65) * mm, "construction": true});
            skLineSegment(sketch, "E194.MirrorCS", {"start": v(-9.07, 12.49) * mm, "end": v(-10.66, 14.67) * mm, "construction": true});
            skCircle(sketch, "E195.MirrorC", {"center": v(-2.01, 19.14) * mm, "radius": 0.57 * mm});
            skLineSegment(sketch, "E196.MirrorCS", {"start": v(0, 0) * mm, "end": v(-15.45, 8.92) * mm, "construction": true});
            skLineSegment(sketch, "E197.MirrorCS", {"start": v(0, 0) * mm, "end": v(-5.95, 13.37) * mm, "construction": true});
            skCircle(sketch, "E198.MirrorC", {"center": v(-5.95, 13.37) * mm, "radius": 0.57 * mm});
            skCircle(sketch, "E199.MirrorC", {"center": v(-10.67, 11.86) * mm, "radius": 0.57 * mm});
            skLineSegment(sketch, "E200.MirrorCS", {"start": v(-21.24, 1.11) * mm, "end": v(-23.84, 1.25) * mm, "construction": true});
            skCircle(sketch, "E201.MirrorC", {"center": v(-4.03, 15.03) * mm, "radius": 0.57 * mm});
            skCircle(sketch, "E202.MirrorC", {"center": v(-24.3, 5.16) * mm, "radius": 0.57 * mm});
            skCircle(sketch, "E203.MirrorC", {"center": v(-13.9, 10.1) * mm, "radius": 0.57 * mm});
            skCircle(sketch, "E204.MirrorC", {"center": v(-5.25, 16.16) * mm, "radius": 0.57 * mm});
            skLineSegment(sketch, "E205.MirrorCS", {"start": v(0, 0) * mm, "end": v(-2.94, 13.85) * mm, "construction": true});
            skLineSegment(sketch, "E206.MirrorCS", {"start": v(-7.5, 12.99) * mm, "end": v(-8.84, 15.3) * mm, "construction": true});
            skLineSegment(sketch, "E207.MirrorCS", {"start": v(-14.33, 12.9) * mm, "end": v(-16.34, 14.71) * mm, "construction": true});
            skLineSegment(sketch, "E208.MirrorCS", {"start": v(0, 0) * mm, "end": v(-18.82, 7.22) * mm, "construction": true});
            skLineSegment(sketch, "E209.MirrorCS", {"start": v(-19.15, 4.07) * mm, "end": v(-21.73, 4.62) * mm, "construction": true});
            skLineSegment(sketch, "E210.MirrorCS", {"start": v(0, 0) * mm, "end": v(-0.8, 15.29) * mm, "construction": true});
            skCircle(sketch, "E211.MirrorC", {"center": v(-10.73, 13.25) * mm, "radius": 0.57 * mm});
            skCircle(sketch, "E212.MirrorC", {"center": v(-8.53, 16.75) * mm, "radius": 0.57 * mm});
            skLineSegment(sketch, "E213.MirrorCS", {"start": v(-13.9, 10.1) * mm, "end": v(-16.11, 11.7) * mm, "construction": true});
            skLineSegment(sketch, "E214.MirrorCS", {"start": v(-20.7, 6.73) * mm, "end": v(-23.23, 7.55) * mm, "construction": true});
            skLineSegment(sketch, "E215.MirrorCS", {"start": v(-18.82, 7.22) * mm, "end": v(-21.32, 8.18) * mm, "construction": true});
            skLineSegment(sketch, "E216.MirrorCS", {"start": v(0, 0) * mm, "end": v(-14.17, 11.47) * mm, "construction": true});
            skLineSegment(sketch, "E217.MirrorCS", {"start": v(-0.8, 15.29) * mm, "end": v(-0.94, 17.89) * mm, "construction": true});
            skCircle(sketch, "E218.MirrorC", {"center": v(-7.03, 15.8) * mm, "radius": 0.57 * mm});
            skLineSegment(sketch, "E219.MirrorCS", {"start": v(-4.03, 15.03) * mm, "end": v(-4.7, 17.56) * mm, "construction": true});
            skLineSegment(sketch, "E220.MirrorCS", {"start": v(0, 0) * mm, "end": v(-9.07, 12.49) * mm, "construction": true});
            skCircle(sketch, "E221.MirrorC", {"center": v(-20, 0) * mm, "radius": 0.57 * mm});
            skLineSegment(sketch, "E222.MirrorCS", {"start": v(-8.84, 15.3) * mm, "end": v(-10.17, 17.6) * mm, "construction": true});
            skLineSegment(sketch, "E223.MirrorCS", {"start": v(-2.94, 13.85) * mm, "end": v(-3.49, 16.4) * mm, "construction": true});
            skCircle(sketch, "E224.MirrorC", {"center": v(-2.82, 17.78) * mm, "radius": 0.57 * mm});
            skLineSegment(sketch, "E225.MirrorCS", {"start": v(-9.02, 13.88) * mm, "end": v(-10.47, 16.13) * mm, "construction": true});
            skCircle(sketch, "E226.MirrorC", {"center": v(-12.5, 13.88) * mm, "radius": 0.57 * mm});
            skCircle(sketch, "E227.MirrorC", {"center": v(-24.97, 2.62) * mm, "radius": 0.57 * mm});
            skLineSegment(sketch, "E228.MirrorCS", {"start": v(0, 0) * mm, "end": v(-20, 0) * mm, "construction": true});
            skCircle(sketch, "E229.MirrorC", {"center": v(-14.33, 12.9) * mm, "radius": 0.57 * mm});
            skCircle(sketch, "E230.MirrorC", {"center": v(-6.6, 17.22) * mm, "radius": 0.57 * mm});
            skCircle(sketch, "E231.MirrorC", {"center": v(-9.02, 13.88) * mm, "radius": 0.57 * mm});
            skLineSegment(sketch, "E232.MirrorCS", {"start": v(-19.78, 2.08) * mm, "end": v(-22.38, 2.35) * mm, "construction": true});
            skCircle(sketch, "E233.MirrorC", {"center": v(-5.66, 14.76) * mm, "radius": 0.57 * mm});
            skCircle(sketch, "E234.MirrorC", {"center": v(-10.17, 17.6) * mm, "radius": 0.57 * mm});
            skCircle(sketch, "E235.MirrorC", {"center": v(-19.98, 5.35) * mm, "radius": 0.57 * mm});
            skLineSegment(sketch, "E236.MirrorCS", {"start": v(0, 0) * mm, "end": v(-13.9, 10.1) * mm, "construction": true});
            skLineSegment(sketch, "E237.MirrorCS", {"start": v(-18.16, 5.9) * mm, "end": v(-20.7, 6.73) * mm, "construction": true});
            skLineSegment(sketch, "E238.MirrorCS", {"start": v(0, 0) * mm, "end": v(-10.73, 13.25) * mm, "construction": true});
            skLineSegment(sketch, "E239.MirrorCS", {"start": v(-5.25, 16.16) * mm, "end": v(-6.06, 18.65) * mm, "construction": true});
            skCircle(sketch, "E240.MirrorC", {"center": v(-19.15, 4.07) * mm, "radius": 0.57 * mm});
            skLineSegment(sketch, "E241.MirrorCS", {"start": v(-10.67, 11.86) * mm, "end": v(-12.5, 13.88) * mm, "construction": true});
            skLineSegment(sketch, "E242.MirrorCS", {"start": v(-22.6, 0) * mm, "end": v(-25.2, 0) * mm, "construction": true});
            skCircle(sketch, "E243.MirrorC", {"center": v(-14.37, 14.37) * mm, "radius": 0.57 * mm});
            skLineSegment(sketch, "E244.MirrorCS", {"start": v(0, 0) * mm, "end": v(-19.15, 4.07) * mm, "construction": true});
            skCircle(sketch, "E245.MirrorC", {"center": v(-14.3, 15.88) * mm, "radius": 0.57 * mm});
            skCircle(sketch, "E246.MirrorC", {"center": v(-16.28, 13.19) * mm, "radius": 0.57 * mm});
            skCircle(sketch, "E247.MirrorC", {"center": v(-22.6, 0) * mm, "radius": 0.57 * mm});
            skCircle(sketch, "E248.MirrorC", {"center": v(-2.4, 15.2) * mm, "radius": 0.57 * mm});
            skCircle(sketch, "E249.MirrorC", {"center": v(-7.5, 12.99) * mm, "radius": 0.57 * mm});
            skLineSegment(sketch, "E250.MirrorCS", {"start": v(-5.66, 14.76) * mm, "end": v(-6.6, 17.22) * mm, "construction": true});
            skLineSegment(sketch, "E251.MirrorCS", {"start": v(-15.45, 8.92) * mm, "end": v(-17.82, 10.29) * mm, "construction": true});
            skCircle(sketch, "E252.MirrorC", {"center": v(-20.7, 6.73) * mm, "radius": 0.57 * mm});
            skLineSegment(sketch, "E253.MirrorCS", {"start": v(0, 0) * mm, "end": v(-21.24, 1.11) * mm, "construction": true});
            skCircle(sketch, "E254.MirrorC", {"center": v(-23.23, 7.55) * mm, "radius": 0.57 * mm});
            skCircle(sketch, "E255.MirrorC", {"center": v(-16.11, 11.7) * mm, "radius": 0.57 * mm});
            skCircle(sketch, "E256.MirrorC", {"center": v(-3.49, 16.4) * mm, "radius": 0.57 * mm});
            skLineSegment(sketch, "E257.MirrorCS", {"start": v(-2.4, 15.2) * mm, "end": v(-2.82, 17.78) * mm, "construction": true});
            skCircle(sketch, "E258.MirrorC", {"center": v(-12.24, 16.84) * mm, "radius": 0.57 * mm});
            skLineSegment(sketch, "E259.MirrorCS", {"start": v(0, 0) * mm, "end": v(-7.5, 12.99) * mm, "construction": true});
            skLineSegment(sketch, "E260.MirrorCS", {"start": v(-21.73, 4.62) * mm, "end": v(-24.3, 5.16) * mm, "construction": true});
            skLineSegment(sketch, "E261.MirrorCS", {"start": v(-17.82, 10.29) * mm, "end": v(-20.16, 11.64) * mm, "construction": true});
            skLineSegment(sketch, "E262.MirrorCS", {"start": v(-10.73, 13.25) * mm, "end": v(-12.43, 15.34) * mm, "construction": true});
            skLineSegment(sketch, "E263.MirrorCS", {"start": v(-12.29, 11.07) * mm, "end": v(-14.33, 12.9) * mm, "construction": true});
            skLineSegment(sketch, "E264.MirrorCS", {"start": v(-19.37, 8.63) * mm, "end": v(-21.82, 9.72) * mm, "construction": true});
            skCircle(sketch, "E265.MirrorC", {"center": v(-18.16, 5.9) * mm, "radius": 0.57 * mm});
            skLineSegment(sketch, "E266.MirrorCS", {"start": v(-12.5, 13.88) * mm, "end": v(-14.3, 15.88) * mm, "construction": true});
            skCircle(sketch, "E267.MirrorC", {"center": v(-18.12, 11.77) * mm, "radius": 0.57 * mm});
            skCircle(sketch, "E268.MirrorC", {"center": v(-8.84, 15.3) * mm, "radius": 0.57 * mm});
            skCircle(sketch, "E269.MirrorC", {"center": v(-18.82, 7.22) * mm, "radius": 0.57 * mm});
            skCircle(sketch, "E270.MirrorC", {"center": v(-21.32, 8.18) * mm, "radius": 0.57 * mm});
            skCircle(sketch, "E271.MirrorC", {"center": v(-16.34, 14.71) * mm, "radius": 0.57 * mm});
            skLineSegment(sketch, "E272.MirrorCS", {"start": v(-5.95, 13.37) * mm, "end": v(-7.03, 15.8) * mm, "construction": true});
            skLineSegment(sketch, "E273.MirrorCS", {"start": v(-20.8, 3.3) * mm, "end": v(-23.4, 3.7) * mm, "construction": true});
            skLineSegment(sketch, "E274.MirrorCS", {"start": v(0, 0) * mm, "end": v(-9.02, 13.88) * mm, "construction": true});
            skCircle(sketch, "E275.MirrorC", {"center": v(-15.84, 10.28) * mm, "radius": 0.57 * mm});
            skLineSegment(sketch, "E276.MirrorCS", {"start": v(0, 0) * mm, "end": v(-20.8, 3.3) * mm, "construction": true});
            skCircle(sketch, "E277.MirrorC", {"center": v(-21.73, 4.62) * mm, "radius": 0.57 * mm});
            skLineSegment(sketch, "E278.MirrorCS", {"start": v(0, 0) * mm, "end": v(-4.03, 15.03) * mm, "construction": true});
            skLineSegment(sketch, "E279.MirrorCS", {"start": v(0, 0) * mm, "end": v(-12.45, 12.45) * mm, "construction": true});
            skCircle(sketch, "E280.MirrorC", {"center": v(-21.82, 9.72) * mm, "radius": 0.57 * mm});
            skLineSegment(sketch, "E281.MirrorCS", {"start": v(-17.4, 8.87) * mm, "end": v(-19.82, 10.1) * mm, "construction": true});
            skCircle(sketch, "E282.MirrorC", {"center": v(-15.45, 8.92) * mm, "radius": 0.57 * mm});
            skLineSegment(sketch, "E283.MirrorCS", {"start": v(0, 0) * mm, "end": v(-2.4, 15.2) * mm, "construction": true});
            skLineSegment(sketch, "E284.MirrorCS", {"start": v(-22.38, 2.35) * mm, "end": v(-24.97, 2.62) * mm, "construction": true});
            skCircle(sketch, "E285.MirrorC", {"center": v(-20.16, 11.64) * mm, "radius": 0.57 * mm});
            skLineSegment(sketch, "E286.MirrorCS", {"start": v(-1.47, 13.96) * mm, "end": v(-1.74, 16.55) * mm, "construction": true});
            skCircle(sketch, "E287.MirrorC", {"center": v(-17.4, 8.87) * mm, "radius": 0.57 * mm});
            skCircle(sketch, "E288.MirrorC", {"center": v(-1.74, 16.55) * mm, "radius": 0.57 * mm});
            skCircle(sketch, "E289.MirrorC", {"center": v(-18.3, 13.3) * mm, "radius": 0.57 * mm});
            skLineSegment(sketch, "E290.MirrorCS", {"start": v(-7.03, 15.8) * mm, "end": v(-8.1, 18.2) * mm, "construction": true});
            skCircle(sketch, "E291.MirrorC", {"center": v(-2.94, 13.85) * mm, "radius": 0.57 * mm});
            skCircle(sketch, "E292.MirrorC", {"center": v(-16.9, 7.52) * mm, "radius": 0.57 * mm});
            skLineSegment(sketch, "E293.MirrorCS", {"start": v(-7.33, 14.38) * mm, "end": v(-8.53, 16.75) * mm, "construction": true});
            skLineSegment(sketch, "E294.MirrorCS", {"start": v(0, 0) * mm, "end": v(-19.78, 2.08) * mm, "construction": true});
            skCircle(sketch, "E295.MirrorC", {"center": v(-22.54, 6.04) * mm, "radius": 0.57 * mm});
            skLineSegment(sketch, "E296.MirrorCS", {"start": v(-14.17, 11.47) * mm, "end": v(-16.28, 13.19) * mm, "construction": true});
            skCircle(sketch, "E297.MirrorC", {"center": v(-17.82, 10.29) * mm, "radius": 0.57 * mm});
            skCircle(sketch, "E298.MirrorC", {"center": v(-1.47, 13.96) * mm, "radius": 0.57 * mm});
            skCircle(sketch, "E299.MirrorC", {"center": v(-21.24, 1.11) * mm, "radius": 0.57 * mm});
            skLineSegment(sketch, "E300.MirrorCS", {"start": v(0, 0) * mm, "end": v(-5.66, 14.76) * mm, "construction": true});
            skCircle(sketch, "E301.MirrorC", {"center": v(-19.82, 10.1) * mm, "radius": 0.57 * mm});
            skLineSegment(sketch, "E302.MirrorCS", {"start": v(0, 0) * mm, "end": v(-7.33, 14.38) * mm, "construction": true});
            skCircle(sketch, "E303.MirrorC", {"center": v(-4.7, 17.56) * mm, "radius": 0.57 * mm});
            skCircle(sketch, "E304.MirrorC", {"center": v(-12.29, 11.07) * mm, "radius": 0.57 * mm});
            skCircle(sketch, "E305.MirrorC", {"center": v(-25.2, 0) * mm, "radius": 0.57 * mm});
            skLineSegment(sketch, "E306.MirrorCS", {"start": v(-3.49, 16.4) * mm, "end": v(-4.03, 18.96) * mm, "construction": true});
            skLineSegment(sketch, "E307.MirrorCS", {"start": v(0, 0) * mm, "end": v(-12.29, 11.07) * mm, "construction": true});
            skCircle(sketch, "E308.MirrorC", {"center": v(-23.4, 3.7) * mm, "radius": 0.57 * mm});
            skLineSegment(sketch, "E309.MirrorCS", {"start": v(-20, 0) * mm, "end": v(-22.6, 0) * mm, "construction": true});
            skLineSegment(sketch, "E310.MirrorCS", {"start": v(-12.45, 12.45) * mm, "end": v(-14.37, 14.37) * mm, "construction": true});
            skCircle(sketch, "E311.MirrorC", {"center": v(-4.44, 13.65) * mm, "radius": 0.57 * mm});
            skCircle(sketch, "E312.MirrorC", {"center": v(-7.33, 14.38) * mm, "radius": 0.57 * mm});
            skLineSegment(sketch, "E313.MirrorCS", {"start": v(-1.74, 16.55) * mm, "end": v(-2.01, 19.14) * mm, "construction": true});
            skLineSegment(sketch, "E314.MirrorCS", {"start": v(-16.9, 7.52) * mm, "end": v(-19.37, 8.63) * mm, "construction": true});
            skCircle(sketch, "E315.MirrorC", {"center": v(-8.1, 18.2) * mm, "radius": 0.57 * mm});
            skLineSegment(sketch, "E316.MirrorCS", {"start": v(0, 0) * mm, "end": v(-17.4, 8.87) * mm, "construction": true});
            skCircle(sketch, "E317.MirrorC", {"center": v(-19.37, 8.63) * mm, "radius": 0.57 * mm});
            skLineSegment(sketch, "E318.MirrorCS", {"start": v(-15.84, 10.28) * mm, "end": v(-18.12, 11.77) * mm, "construction": true});
            skCircle(sketch, "E319.MirrorC", {"center": v(-23.84, 1.25) * mm, "radius": 0.57 * mm});
            skCircle(sketch, "E320.MirrorC", {"center": v(-20.8, 3.3) * mm, "radius": 0.57 * mm});
            skLineSegment(sketch, "E321.MirrorCS", {"start": v(0, 0) * mm, "end": v(-16.9, 7.52) * mm, "construction": true});
            skLineSegment(sketch, "E322.MirrorCS", {"start": v(0, 0) * mm, "end": v(-18.16, 5.9) * mm, "construction": true});
            skCircle(sketch, "E323.MirrorC", {"center": v(0, -16.6) * mm, "radius": 0.57 * mm});
            skCircle(sketch, "E324.MirrorC", {"center": v(0, -14) * mm, "radius": 0.57 * mm});
            skCircle(sketch, "E325.MirrorC", {"center": v(0, -19.2) * mm, "radius": 0.57 * mm});
            skLineSegment(sketch, "E326.MirrorCS", {"start": v(0, -14) * mm, "end": v(0, -16.6) * mm, "construction": true});
            skCircle(sketch, "E327.MirrorC", {"center": v(-15.84, -10.28) * mm, "radius": 0.57 * mm});
            skCircle(sketch, "E328.MirrorC", {"center": v(-2.94, -13.85) * mm, "radius": 0.57 * mm});
            skCircle(sketch, "E329.MirrorC", {"center": v(-10.73, -13.25) * mm, "radius": 0.57 * mm});
            skCircle(sketch, "E330.MirrorC", {"center": v(8.84, -15.3) * mm, "radius": 0.57 * mm});
            skCircle(sketch, "E331.MirrorC", {"center": v(15.84, -10.28) * mm, "radius": 0.57 * mm});
            skLineSegment(sketch, "E332.MirrorCS", {"start": v(-4.44, -13.65) * mm, "end": v(-5.25, -16.16) * mm, "construction": true});
            skCircle(sketch, "E333.MirrorC", {"center": v(19.15, -4.07) * mm, "radius": 0.57 * mm});
            skCircle(sketch, "E334.MirrorC", {"center": v(-12.5, -13.88) * mm, "radius": 0.57 * mm});
            skCircle(sketch, "E335.MirrorC", {"center": v(10.66, -14.67) * mm, "radius": 0.57 * mm});
            skCircle(sketch, "E336.MirrorC", {"center": v(14.17, -11.47) * mm, "radius": 0.57 * mm});
            skCircle(sketch, "E337.MirrorC", {"center": v(0.8, -15.29) * mm, "radius": 0.57 * mm});
            skCircle(sketch, "E338.MirrorC", {"center": v(19.78, -2.08) * mm, "radius": 0.57 * mm});
            skLineSegment(sketch, "E339.MirrorCS", {"start": v(4.44, -13.65) * mm, "end": v(5.25, -16.16) * mm, "construction": true});
            skCircle(sketch, "E340.MirrorC", {"center": v(-20.8, -3.3) * mm, "radius": 0.57 * mm});
            skCircle(sketch, "E341.MirrorC", {"center": v(-12.29, -11.07) * mm, "radius": 0.57 * mm});
            skLineSegment(sketch, "E342.MirrorCS", {"start": v(-19.15, -4.07) * mm, "end": v(-21.73, -4.62) * mm, "construction": true});
            skLineSegment(sketch, "E343.MirrorCS", {"start": v(-10.67, -11.86) * mm, "end": v(-12.5, -13.88) * mm, "construction": true});
            skCircle(sketch, "E344.MirrorC", {"center": v(9.07, -12.49) * mm, "radius": 0.57 * mm});
            skCircle(sketch, "E345.MirrorC", {"center": v(12.45, -12.45) * mm, "radius": 0.57 * mm});
            skCircle(sketch, "E346.MirrorC", {"center": v(-19.78, -2.08) * mm, "radius": 0.57 * mm});
            skCircle(sketch, "E347.MirrorC", {"center": v(22.38, -2.35) * mm, "radius": 0.57 * mm});
            skLineSegment(sketch, "E348.MirrorCS", {"start": v(9.07, -12.49) * mm, "end": v(10.66, -14.67) * mm, "construction": true});
            skCircle(sketch, "E349.MirrorC", {"center": v(-3.49, -16.4) * mm, "radius": 0.57 * mm});
            skLineSegment(sketch, "E350.MirrorCS", {"start": v(-5.95, -13.37) * mm, "end": v(-7.03, -15.8) * mm, "construction": true});
            skCircle(sketch, "E351.MirrorC", {"center": v(-1.74, -16.55) * mm, "radius": 0.57 * mm});
            skLineSegment(sketch, "E352.MirrorCS", {"start": v(-9.07, -12.49) * mm, "end": v(-10.66, -14.67) * mm, "construction": true});
            skCircle(sketch, "E353.MirrorC", {"center": v(-19.15, -4.07) * mm, "radius": 0.57 * mm});
            skCircle(sketch, "E354.MirrorC", {"center": v(10.67, -11.86) * mm, "radius": 0.57 * mm});
            skLineSegment(sketch, "E355.MirrorCS", {"start": v(0, -16.6) * mm, "end": v(0, -19.2) * mm, "construction": true});
            skCircle(sketch, "E356.MirrorC", {"center": v(13.9, -10.1) * mm, "radius": 0.57 * mm});
            skCircle(sketch, "E357.MirrorC", {"center": v(5.25, -16.16) * mm, "radius": 0.57 * mm});
            skLineSegment(sketch, "E358.MirrorCS", {"start": v(7.5, -12.99) * mm, "end": v(8.84, -15.3) * mm, "construction": true});
            skCircle(sketch, "E359.MirrorC", {"center": v(10.73, -13.25) * mm, "radius": 0.57 * mm});
            skLineSegment(sketch, "E360.MirrorCS", {"start": v(13.9, -10.1) * mm, "end": v(16.11, -11.7) * mm, "construction": true});
            skCircle(sketch, "E361.MirrorC", {"center": v(15.45, -8.92) * mm, "radius": 0.57 * mm});
            skLineSegment(sketch, "E362.MirrorCS", {"start": v(15.45, -8.92) * mm, "end": v(17.82, -10.29) * mm, "construction": true});
            skCircle(sketch, "E363.MirrorC", {"center": v(17.4, -8.87) * mm, "radius": 0.57 * mm});
            skCircle(sketch, "E364.MirrorC", {"center": v(-19.98, -5.35) * mm, "radius": 0.57 * mm});
            skCircle(sketch, "E365.MirrorC", {"center": v(-14.17, -11.47) * mm, "radius": 0.57 * mm});
            skCircle(sketch, "E366.MirrorC", {"center": v(20.7, -6.73) * mm, "radius": 0.57 * mm});
            skCircle(sketch, "E367.MirrorC", {"center": v(-21.73, -4.62) * mm, "radius": 0.57 * mm});
            skLineSegment(sketch, "E368.MirrorCS", {"start": v(5.95, -13.37) * mm, "end": v(7.03, -15.8) * mm, "construction": true});
            skCircle(sketch, "E369.MirrorC", {"center": v(4.44, -13.65) * mm, "radius": 0.57 * mm});
            skCircle(sketch, "E370.MirrorC", {"center": v(-4.03, -15.03) * mm, "radius": 0.57 * mm});
            skCircle(sketch, "E371.MirrorC", {"center": v(19.37, -8.63) * mm, "radius": 0.57 * mm});
            skCircle(sketch, "E372.MirrorC", {"center": v(20.8, -3.3) * mm, "radius": 0.57 * mm});
            skLineSegment(sketch, "E373.MirrorCS", {"start": v(-12.29, -11.07) * mm, "end": v(-14.33, -12.9) * mm, "construction": true});
            skCircle(sketch, "E374.MirrorC", {"center": v(-9.02, -13.88) * mm, "radius": 0.57 * mm});
            skLineSegment(sketch, "E375.MirrorCS", {"start": v(12.29, -11.07) * mm, "end": v(14.33, -12.9) * mm, "construction": true});
            skCircle(sketch, "E376.MirrorC", {"center": v(7.5, -12.99) * mm, "radius": 0.57 * mm});
            skCircle(sketch, "E377.MirrorC", {"center": v(-10.67, -11.86) * mm, "radius": 0.57 * mm});
            skCircle(sketch, "E378.MirrorC", {"center": v(-9.07, -12.49) * mm, "radius": 0.57 * mm});
            skCircle(sketch, "E379.MirrorC", {"center": v(18.82, -7.22) * mm, "radius": 0.57 * mm});
            skCircle(sketch, "E380.MirrorC", {"center": v(-14.33, -12.9) * mm, "radius": 0.57 * mm});
            skLineSegment(sketch, "E381.MirrorCS", {"start": v(-13.9, -10.1) * mm, "end": v(-16.11, -11.7) * mm, "construction": true});
            skCircle(sketch, "E382.MirrorC", {"center": v(-21.24, -1.11) * mm, "radius": 0.57 * mm});
            skLineSegment(sketch, "E383.MirrorCS", {"start": v(-16.9, -7.52) * mm, "end": v(-19.37, -8.63) * mm, "construction": true});
            skCircle(sketch, "E384.MirrorC", {"center": v(4.03, -15.03) * mm, "radius": 0.57 * mm});
            skCircle(sketch, "E385.MirrorC", {"center": v(-8.84, -15.3) * mm, "radius": 0.57 * mm});
            skLineSegment(sketch, "E386.MirrorCS", {"start": v(1.47, -13.96) * mm, "end": v(1.74, -16.55) * mm, "construction": true});
            skCircle(sketch, "E387.MirrorC", {"center": v(16.9, -7.52) * mm, "radius": 0.57 * mm});
            skCircle(sketch, "E388.MirrorC", {"center": v(2.94, -13.85) * mm, "radius": 0.57 * mm});
            skCircle(sketch, "E389.MirrorC", {"center": v(-17.4, -8.87) * mm, "radius": 0.57 * mm});
            skCircle(sketch, "E390.MirrorC", {"center": v(-16.11, -11.7) * mm, "radius": 0.57 * mm});
            skCircle(sketch, "E391.MirrorC", {"center": v(21.24, -1.11) * mm, "radius": 0.57 * mm});
            skLineSegment(sketch, "E392.MirrorCS", {"start": v(-2.94, -13.85) * mm, "end": v(-3.49, -16.4) * mm, "construction": true});
            skCircle(sketch, "E393.MirrorC", {"center": v(12.5, -13.88) * mm, "radius": 0.57 * mm});
            skLineSegment(sketch, "E394.MirrorCS", {"start": v(16.9, -7.52) * mm, "end": v(19.37, -8.63) * mm, "construction": true});
            skLineSegment(sketch, "E395.MirrorCS", {"start": v(-15.45, -8.92) * mm, "end": v(-17.82, -10.29) * mm, "construction": true});
            skCircle(sketch, "E396.MirrorC", {"center": v(-2.4, -15.2) * mm, "radius": 0.57 * mm});
            skLineSegment(sketch, "E397.MirrorCS", {"start": v(-19.78, -2.08) * mm, "end": v(-22.38, -2.35) * mm, "construction": true});
            skLineSegment(sketch, "E398.MirrorCS", {"start": v(19.15, -4.07) * mm, "end": v(21.73, -4.62) * mm, "construction": true});
            skCircle(sketch, "E399.MirrorC", {"center": v(-4.44, -13.65) * mm, "radius": 0.57 * mm});
            skCircle(sketch, "E400.MirrorC", {"center": v(21.73, -4.62) * mm, "radius": 0.57 * mm});
            skCircle(sketch, "E401.MirrorC", {"center": v(1.74, -16.55) * mm, "radius": 0.57 * mm});
            skCircle(sketch, "E402.MirrorC", {"center": v(9.02, -13.88) * mm, "radius": 0.57 * mm});
            skCircle(sketch, "E403.MirrorC", {"center": v(-0.8, -15.29) * mm, "radius": 0.57 * mm});
            skCircle(sketch, "E404.MirrorC", {"center": v(-20.7, -6.73) * mm, "radius": 0.57 * mm});
            skLineSegment(sketch, "E405.MirrorCS", {"start": v(18.16, -5.9) * mm, "end": v(20.7, -6.73) * mm, "construction": true});
            skCircle(sketch, "E406.MirrorC", {"center": v(3.49, -16.4) * mm, "radius": 0.57 * mm});
            skCircle(sketch, "E407.MirrorC", {"center": v(7.03, -15.8) * mm, "radius": 0.57 * mm});
            skCircle(sketch, "E408.MirrorC", {"center": v(-15.45, -8.92) * mm, "radius": 0.57 * mm});
            skCircle(sketch, "E409.MirrorC", {"center": v(-1.47, -13.96) * mm, "radius": 0.57 * mm});
            skLineSegment(sketch, "E410.MirrorCS", {"start": v(-1.47, -13.96) * mm, "end": v(-1.74, -16.55) * mm, "construction": true});
            skCircle(sketch, "E411.MirrorC", {"center": v(-19.37, -8.63) * mm, "radius": 0.57 * mm});
            skCircle(sketch, "E412.MirrorC", {"center": v(-7.03, -15.8) * mm, "radius": 0.57 * mm});
            skLineSegment(sketch, "E413.MirrorCS", {"start": v(2.94, -13.85) * mm, "end": v(3.49, -16.4) * mm, "construction": true});
            skCircle(sketch, "E414.MirrorC", {"center": v(14.33, -12.9) * mm, "radius": 0.57 * mm});
            skCircle(sketch, "E415.MirrorC", {"center": v(16.11, -11.7) * mm, "radius": 0.57 * mm});
            skCircle(sketch, "E416.MirrorC", {"center": v(7.33, -14.38) * mm, "radius": 0.57 * mm});
            skLineSegment(sketch, "E417.MirrorCS", {"start": v(-7.5, -12.99) * mm, "end": v(-8.84, -15.3) * mm, "construction": true});
            skCircle(sketch, "E418.MirrorC", {"center": v(-22.38, -2.35) * mm, "radius": 0.57 * mm});
            skCircle(sketch, "E419.MirrorC", {"center": v(-5.25, -16.16) * mm, "radius": 0.57 * mm});
            skCircle(sketch, "E420.MirrorC", {"center": v(2.4, -15.2) * mm, "radius": 0.57 * mm});
            skCircle(sketch, "E421.MirrorC", {"center": v(12.29, -11.07) * mm, "radius": 0.57 * mm});
            skCircle(sketch, "E422.MirrorC", {"center": v(19.98, -5.35) * mm, "radius": 0.57 * mm});
            skCircle(sketch, "E423.MirrorC", {"center": v(5.66, -14.76) * mm, "radius": 0.57 * mm});
            skCircle(sketch, "E424.MirrorC", {"center": v(-18.82, -7.22) * mm, "radius": 0.57 * mm});
            skCircle(sketch, "E425.MirrorC", {"center": v(-17.82, -10.29) * mm, "radius": 0.57 * mm});
            skLineSegment(sketch, "E426.MirrorCS", {"start": v(10.67, -11.86) * mm, "end": v(12.5, -13.88) * mm, "construction": true});
            skCircle(sketch, "E427.MirrorC", {"center": v(-7.33, -14.38) * mm, "radius": 0.57 * mm});
            skCircle(sketch, "E428.MirrorC", {"center": v(-7.5, -12.99) * mm, "radius": 0.57 * mm});
            skCircle(sketch, "E429.MirrorC", {"center": v(-16.9, -7.52) * mm, "radius": 0.57 * mm});
            skCircle(sketch, "E430.MirrorC", {"center": v(-5.66, -14.76) * mm, "radius": 0.57 * mm});
            skCircle(sketch, "E431.MirrorC", {"center": v(17.82, -10.29) * mm, "radius": 0.57 * mm});
            skCircle(sketch, "E432.MirrorC", {"center": v(-12.45, -12.45) * mm, "radius": 0.57 * mm});
            skCircle(sketch, "E433.MirrorC", {"center": v(-13.9, -10.1) * mm, "radius": 0.57 * mm});
            skLineSegment(sketch, "E434.MirrorCS", {"start": v(-18.16, -5.9) * mm, "end": v(-20.7, -6.73) * mm, "construction": true});
            skCircle(sketch, "E435.MirrorC", {"center": v(-5.95, -13.37) * mm, "radius": 0.57 * mm});
            skCircle(sketch, "E436.MirrorC", {"center": v(-18.16, -5.9) * mm, "radius": 0.57 * mm});
            skCircle(sketch, "E437.MirrorC", {"center": v(-10.66, -14.67) * mm, "radius": 0.57 * mm});
            skCircle(sketch, "E438.MirrorC", {"center": v(5.95, -13.37) * mm, "radius": 0.57 * mm});
            skCircle(sketch, "E439.MirrorC", {"center": v(18.16, -5.9) * mm, "radius": 0.57 * mm});
            skCircle(sketch, "E440.MirrorC", {"center": v(1.47, -13.96) * mm, "radius": 0.57 * mm});
            skLineSegment(sketch, "E441.MirrorCS", {"start": v(19.78, -2.08) * mm, "end": v(22.38, -2.35) * mm, "construction": true});
            skLineSegment(sketch, "E442.MirrorCS", {"start": v(-3.49, -16.4) * mm, "end": v(-4.03, -18.96) * mm, "construction": true});
            skCircle(sketch, "E443.MirrorC", {"center": v(-24.97, -2.62) * mm, "radius": 0.57 * mm});
            skCircle(sketch, "E444.MirrorC", {"center": v(-14.37, -14.37) * mm, "radius": 0.57 * mm});
            skCircle(sketch, "E445.MirrorC", {"center": v(14.37, -14.37) * mm, "radius": 0.57 * mm});
            skLineSegment(sketch, "E446.MirrorCS", {"start": v(15.84, -10.28) * mm, "end": v(18.12, -11.77) * mm, "construction": true});
            skCircle(sketch, "E447.MirrorC", {"center": v(8.1, -18.2) * mm, "radius": 0.57 * mm});
            skLineSegment(sketch, "E448.MirrorCS", {"start": v(5.25, -16.16) * mm, "end": v(6.06, -18.65) * mm, "construction": true});
            skCircle(sketch, "E449.MirrorC", {"center": v(-12.24, -16.84) * mm, "radius": 0.57 * mm});
            skLineSegment(sketch, "E450.MirrorCS", {"start": v(-7.03, -15.8) * mm, "end": v(-8.1, -18.2) * mm, "construction": true});
            skLineSegment(sketch, "E451.MirrorCS", {"start": v(0.8, -15.29) * mm, "end": v(0.94, -17.89) * mm, "construction": true});
            skCircle(sketch, "E452.MirrorC", {"center": v(12.43, -15.34) * mm, "radius": 0.57 * mm});
            skCircle(sketch, "E453.MirrorC", {"center": v(-0.94, -17.89) * mm, "radius": 0.57 * mm});
            skLineSegment(sketch, "E454.MirrorCS", {"start": v(19.98, -5.35) * mm, "end": v(22.54, -6.04) * mm, "construction": true});
            skCircle(sketch, "E455.MirrorC", {"center": v(6.06, -18.65) * mm, "radius": 0.57 * mm});
            skCircle(sketch, "E456.MirrorC", {"center": v(0.94, -17.89) * mm, "radius": 0.57 * mm});
            skLineSegment(sketch, "E457.MirrorCS", {"start": v(10.66, -14.67) * mm, "end": v(12.24, -16.84) * mm, "construction": true});
            skLineSegment(sketch, "E458.MirrorCS", {"start": v(-2.4, -15.2) * mm, "end": v(-2.82, -17.78) * mm, "construction": true});
            skLineSegment(sketch, "E459.MirrorCS", {"start": v(-20.8, -3.3) * mm, "end": v(-23.4, -3.7) * mm, "construction": true});
            skCircle(sketch, "E460.MirrorC", {"center": v(-18.3, -13.3) * mm, "radius": 0.57 * mm});
            skCircle(sketch, "E461.MirrorC", {"center": v(-2.01, -19.14) * mm, "radius": 0.57 * mm});
            skLineSegment(sketch, "E462.MirrorCS", {"start": v(-9.02, -13.88) * mm, "end": v(-10.47, -16.13) * mm, "construction": true});
            skCircle(sketch, "E463.MirrorC", {"center": v(10.47, -16.13) * mm, "radius": 0.57 * mm});
            skLineSegment(sketch, "E464.MirrorCS", {"start": v(16.11, -11.7) * mm, "end": v(18.3, -13.3) * mm, "construction": true});
            skCircle(sketch, "E465.MirrorC", {"center": v(4.03, -18.96) * mm, "radius": 0.57 * mm});
            skCircle(sketch, "E466.MirrorC", {"center": v(-23.84, -1.25) * mm, "radius": 0.57 * mm});
            skCircle(sketch, "E467.MirrorC", {"center": v(-4.7, -17.56) * mm, "radius": 0.57 * mm});
            skCircle(sketch, "E468.MirrorC", {"center": v(-2.82, -17.78) * mm, "radius": 0.57 * mm});
            skLineSegment(sketch, "E469.MirrorCS", {"start": v(14.33, -12.9) * mm, "end": v(16.34, -14.71) * mm, "construction": true});
            skCircle(sketch, "E470.MirrorC", {"center": v(8.53, -16.75) * mm, "radius": 0.57 * mm});
            skCircle(sketch, "E471.MirrorC", {"center": v(-6.06, -18.65) * mm, "radius": 0.57 * mm});
            skLineSegment(sketch, "E472.MirrorCS", {"start": v(20.7, -6.73) * mm, "end": v(23.23, -7.55) * mm, "construction": true});
            skCircle(sketch, "E473.MirrorC", {"center": v(2.01, -19.14) * mm, "radius": 0.57 * mm});
            skLineSegment(sketch, "E474.MirrorCS", {"start": v(4.03, -15.03) * mm, "end": v(4.7, -17.56) * mm, "construction": true});
            skCircle(sketch, "E475.MirrorC", {"center": v(-23.4, -3.7) * mm, "radius": 0.57 * mm});
            skLineSegment(sketch, "E476.MirrorCS", {"start": v(12.5, -13.88) * mm, "end": v(14.3, -15.88) * mm, "construction": true});
            skLineSegment(sketch, "E477.MirrorCS", {"start": v(-7.33, -14.38) * mm, "end": v(-8.53, -16.75) * mm, "construction": true});
            skCircle(sketch, "E478.MirrorC", {"center": v(16.34, -14.71) * mm, "radius": 0.57 * mm});
            skLineSegment(sketch, "E479.MirrorCS", {"start": v(20.8, -3.3) * mm, "end": v(23.4, -3.7) * mm, "construction": true});
            skCircle(sketch, "E480.MirrorC", {"center": v(21.32, -8.18) * mm, "radius": 0.57 * mm});
            skCircle(sketch, "E481.MirrorC", {"center": v(-4.03, -18.96) * mm, "radius": 0.57 * mm});
            skLineSegment(sketch, "E482.MirrorCS", {"start": v(19.37, -8.63) * mm, "end": v(21.82, -9.72) * mm, "construction": true});
            skCircle(sketch, "E483.MirrorC", {"center": v(24.3, -5.16) * mm, "radius": 0.57 * mm});
            skLineSegment(sketch, "E484.MirrorCS", {"start": v(-18.82, -7.22) * mm, "end": v(-21.32, -8.18) * mm, "construction": true});
            skLineSegment(sketch, "E485.MirrorCS", {"start": v(-12.45, -12.45) * mm, "end": v(-14.37, -14.37) * mm, "construction": true});
            skCircle(sketch, "E486.MirrorC", {"center": v(-22.54, -6.04) * mm, "radius": 0.57 * mm});
            skLineSegment(sketch, "E487.MirrorCS", {"start": v(5.66, -14.76) * mm, "end": v(6.6, -17.22) * mm, "construction": true});
            skLineSegment(sketch, "E488.MirrorCS", {"start": v(21.73, -4.62) * mm, "end": v(24.3, -5.16) * mm, "construction": true});
            skCircle(sketch, "E489.MirrorC", {"center": v(12.24, -16.84) * mm, "radius": 0.57 * mm});
            skLineSegment(sketch, "E490.MirrorCS", {"start": v(17.4, -8.87) * mm, "end": v(19.82, -10.1) * mm, "construction": true});
            skCircle(sketch, "E491.MirrorC", {"center": v(-14.3, -15.88) * mm, "radius": 0.57 * mm});
            skCircle(sketch, "E492.MirrorC", {"center": v(18.12, -11.77) * mm, "radius": 0.57 * mm});
            skLineSegment(sketch, "E493.MirrorCS", {"start": v(-17.82, -10.29) * mm, "end": v(-20.16, -11.64) * mm, "construction": true});
            skLineSegment(sketch, "E494.MirrorCS", {"start": v(7.03, -15.8) * mm, "end": v(8.1, -18.2) * mm, "construction": true});
            skLineSegment(sketch, "E495.MirrorCS", {"start": v(-15.84, -10.28) * mm, "end": v(-18.12, -11.77) * mm, "construction": true});
            skCircle(sketch, "E496.MirrorC", {"center": v(-16.34, -14.71) * mm, "radius": 0.57 * mm});
            skCircle(sketch, "E497.MirrorC", {"center": v(18.3, -13.3) * mm, "radius": 0.57 * mm});
            skLineSegment(sketch, "E498.MirrorCS", {"start": v(-21.73, -4.62) * mm, "end": v(-24.3, -5.16) * mm, "construction": true});
            skCircle(sketch, "E499.MirrorC", {"center": v(-24.3, -5.16) * mm, "radius": 0.57 * mm});
            skLineSegment(sketch, "E500.MirrorCS", {"start": v(21.24, -1.11) * mm, "end": v(23.84, -1.25) * mm, "construction": true});
            skLineSegment(sketch, "E501.MirrorCS", {"start": v(7.33, -14.38) * mm, "end": v(8.53, -16.75) * mm, "construction": true});
            skCircle(sketch, "E502.MirrorC", {"center": v(-10.47, -16.13) * mm, "radius": 0.57 * mm});
            skLineSegment(sketch, "E503.MirrorCS", {"start": v(-14.33, -12.9) * mm, "end": v(-16.34, -14.71) * mm, "construction": true});
            skCircle(sketch, "E504.MirrorC", {"center": v(22.54, -6.04) * mm, "radius": 0.57 * mm});
            skLineSegment(sketch, "E505.MirrorCS", {"start": v(-10.66, -14.67) * mm, "end": v(-12.24, -16.84) * mm, "construction": true});
            skCircle(sketch, "E506.MirrorC", {"center": v(-8.1, -18.2) * mm, "radius": 0.57 * mm});
            skCircle(sketch, "E507.MirrorC", {"center": v(6.6, -17.22) * mm, "radius": 0.57 * mm});
            skLineSegment(sketch, "E508.MirrorCS", {"start": v(-5.25, -16.16) * mm, "end": v(-6.06, -18.65) * mm, "construction": true});
            skLineSegment(sketch, "E509.MirrorCS", {"start": v(-19.37, -8.63) * mm, "end": v(-21.82, -9.72) * mm, "construction": true});
            skCircle(sketch, "E510.MirrorC", {"center": v(16.28, -13.19) * mm, "radius": 0.57 * mm});
            skCircle(sketch, "E511.MirrorC", {"center": v(-18.12, -11.77) * mm, "radius": 0.57 * mm});
            skLineSegment(sketch, "E512.MirrorCS", {"start": v(-4.03, -15.03) * mm, "end": v(-4.7, -17.56) * mm, "construction": true});
            skCircle(sketch, "E513.MirrorC", {"center": v(10.17, -17.6) * mm, "radius": 0.57 * mm});
            skCircle(sketch, "E514.MirrorC", {"center": v(21.82, -9.72) * mm, "radius": 0.57 * mm});
            skLineSegment(sketch, "E515.MirrorCS", {"start": v(-14.17, -11.47) * mm, "end": v(-16.28, -13.19) * mm, "construction": true});
            skCircle(sketch, "E516.MirrorC", {"center": v(-21.82, -9.72) * mm, "radius": 0.57 * mm});
            skLineSegment(sketch, "E517.MirrorCS", {"start": v(2.4, -15.2) * mm, "end": v(2.82, -17.78) * mm, "construction": true});
            skLineSegment(sketch, "E518.MirrorCS", {"start": v(10.73, -13.25) * mm, "end": v(12.43, -15.34) * mm, "construction": true});
            skLineSegment(sketch, "E519.MirrorCS", {"start": v(-10.73, -13.25) * mm, "end": v(-12.43, -15.34) * mm, "construction": true});
            skLineSegment(sketch, "E520.MirrorCS", {"start": v(18.82, -7.22) * mm, "end": v(21.32, -8.18) * mm, "construction": true});
            skCircle(sketch, "E521.MirrorC", {"center": v(-8.53, -16.75) * mm, "radius": 0.57 * mm});
            skCircle(sketch, "E522.MirrorC", {"center": v(-23.23, -7.55) * mm, "radius": 0.57 * mm});
            skLineSegment(sketch, "E523.MirrorCS", {"start": v(8.84, -15.3) * mm, "end": v(10.17, -17.6) * mm, "construction": true});
            skCircle(sketch, "E524.MirrorC", {"center": v(-21.32, -8.18) * mm, "radius": 0.57 * mm});
            skLineSegment(sketch, "E525.MirrorCS", {"start": v(-1.74, -16.55) * mm, "end": v(-2.01, -19.14) * mm, "construction": true});
            skLineSegment(sketch, "E526.MirrorCS", {"start": v(-5.66, -14.76) * mm, "end": v(-6.6, -17.22) * mm, "construction": true});
            skCircle(sketch, "E527.MirrorC", {"center": v(-12.43, -15.34) * mm, "radius": 0.57 * mm});
            skCircle(sketch, "E528.MirrorC", {"center": v(2.82, -17.78) * mm, "radius": 0.57 * mm});
            skCircle(sketch, "E529.MirrorC", {"center": v(24.97, -2.62) * mm, "radius": 0.57 * mm});
            skCircle(sketch, "E530.MirrorC", {"center": v(-10.17, -17.6) * mm, "radius": 0.57 * mm});
            skLineSegment(sketch, "E531.MirrorCS", {"start": v(-12.5, -13.88) * mm, "end": v(-14.3, -15.88) * mm, "construction": true});
            skLineSegment(sketch, "E532.MirrorCS", {"start": v(-8.84, -15.3) * mm, "end": v(-10.17, -17.6) * mm, "construction": true});
            skCircle(sketch, "E533.MirrorC", {"center": v(23.84, -1.25) * mm, "radius": 0.57 * mm});
            skLineSegment(sketch, "E534.MirrorCS", {"start": v(-20.7, -6.73) * mm, "end": v(-23.23, -7.55) * mm, "construction": true});
            skLineSegment(sketch, "E535.MirrorCS", {"start": v(-16.11, -11.7) * mm, "end": v(-18.3, -13.3) * mm, "construction": true});
            skCircle(sketch, "E536.MirrorC", {"center": v(-16.28, -13.19) * mm, "radius": 0.57 * mm});
            skLineSegment(sketch, "E537.MirrorCS", {"start": v(9.02, -13.88) * mm, "end": v(10.47, -16.13) * mm, "construction": true});
            skCircle(sketch, "E538.MirrorC", {"center": v(4.7, -17.56) * mm, "radius": 0.57 * mm});
            skCircle(sketch, "E539.MirrorC", {"center": v(23.23, -7.55) * mm, "radius": 0.57 * mm});
            skLineSegment(sketch, "E540.MirrorCS", {"start": v(-21.24, -1.11) * mm, "end": v(-23.84, -1.25) * mm, "construction": true});
            skLineSegment(sketch, "E541.MirrorCS", {"start": v(1.74, -16.55) * mm, "end": v(2.01, -19.14) * mm, "construction": true});
            skLineSegment(sketch, "E542.MirrorCS", {"start": v(-19.98, -5.35) * mm, "end": v(-22.54, -6.04) * mm, "construction": true});
            skCircle(sketch, "E543.MirrorC", {"center": v(19.82, -10.1) * mm, "radius": 0.57 * mm});
            skLineSegment(sketch, "E544.MirrorCS", {"start": v(12.45, -12.45) * mm, "end": v(14.37, -14.37) * mm, "construction": true});
            skLineSegment(sketch, "E545.MirrorCS", {"start": v(3.49, -16.4) * mm, "end": v(4.03, -18.96) * mm, "construction": true});
            skLineSegment(sketch, "E546.MirrorCS", {"start": v(17.82, -10.29) * mm, "end": v(20.16, -11.64) * mm, "construction": true});
            skCircle(sketch, "E547.MirrorC", {"center": v(14.3, -15.88) * mm, "radius": 0.57 * mm});
            skLineSegment(sketch, "E548.MirrorCS", {"start": v(-17.4, -8.87) * mm, "end": v(-19.82, -10.1) * mm, "construction": true});
            skLineSegment(sketch, "E549.MirrorCS", {"start": v(-0.8, -15.29) * mm, "end": v(-0.94, -17.89) * mm, "construction": true});
            skCircle(sketch, "E550.MirrorC", {"center": v(-19.82, -10.1) * mm, "radius": 0.57 * mm});
            skCircle(sketch, "E551.MirrorC", {"center": v(20.16, -11.64) * mm, "radius": 0.57 * mm});
            skLineSegment(sketch, "E552.MirrorCS", {"start": v(14.17, -11.47) * mm, "end": v(16.28, -13.19) * mm, "construction": true});
            skCircle(sketch, "E553.MirrorC", {"center": v(-20.16, -11.64) * mm, "radius": 0.57 * mm});
            skCircle(sketch, "E554.MirrorC", {"center": v(23.4, -3.7) * mm, "radius": 0.57 * mm});
            skCircle(sketch, "E555.MirrorC", {"center": v(-6.6, -17.22) * mm, "radius": 0.57 * mm});
            skLineSegment(sketch, "E556.MirrorCS", {"start": v(0, 0) * mm, "end": v(-18.16, -5.9) * mm, "construction": true});
            skLineSegment(sketch, "E557.MirrorCS", {"start": v(0, 0) * mm, "end": v(-7.5, -12.99) * mm, "construction": true});
            skLineSegment(sketch, "E558.MirrorCS", {"start": v(0, 0) * mm, "end": v(-5.95, -13.37) * mm, "construction": true});
            skLineSegment(sketch, "E559.MirrorCS", {"start": v(0, 0) * mm, "end": v(19.15, -4.07) * mm, "construction": true});
            skLineSegment(sketch, "E560.MirrorCS", {"start": v(0, 0) * mm, "end": v(10.73, -13.25) * mm, "construction": true});
            skLineSegment(sketch, "E561.MirrorCS", {"start": v(0, 0) * mm, "end": v(-16.9, -7.52) * mm, "construction": true});
            skLineSegment(sketch, "E562.MirrorCS", {"start": v(0, 0) * mm, "end": v(-9.02, -13.88) * mm, "construction": true});
            skLineSegment(sketch, "E563.MirrorCS", {"start": v(0, 0) * mm, "end": v(0.8, -15.29) * mm, "construction": true});
            skLineSegment(sketch, "E564.MirrorCS", {"start": v(0, 0) * mm, "end": v(0, -14) * mm, "construction": true});
            skLineSegment(sketch, "E565.MirrorCS", {"start": v(0, 0) * mm, "end": v(-15.45, -8.92) * mm, "construction": true});
            skLineSegment(sketch, "E566.MirrorCS", {"start": v(0, 0) * mm, "end": v(-0.8, -15.29) * mm, "construction": true});
            skLineSegment(sketch, "E567.MirrorCS", {"start": v(0, 0) * mm, "end": v(1.47, -13.96) * mm, "construction": true});
            skLineSegment(sketch, "E568.MirrorCS", {"start": v(0, 0) * mm, "end": v(15.84, -10.28) * mm, "construction": true});
            skLineSegment(sketch, "E569.MirrorCS", {"start": v(0, 0) * mm, "end": v(19.98, -5.35) * mm, "construction": true});
            skLineSegment(sketch, "E570.MirrorCS", {"start": v(0, 0) * mm, "end": v(4.44, -13.65) * mm, "construction": true});
            skLineSegment(sketch, "E571.MirrorCS", {"start": v(0, 0) * mm, "end": v(-18.82, -7.22) * mm, "construction": true});
            skLineSegment(sketch, "E572.MirrorCS", {"start": v(0, 0) * mm, "end": v(2.94, -13.85) * mm, "construction": true});
            skLineSegment(sketch, "E573.MirrorCS", {"start": v(0, 0) * mm, "end": v(18.82, -7.22) * mm, "construction": true});
            skLineSegment(sketch, "E574.MirrorCS", {"start": v(0, 0) * mm, "end": v(10.67, -11.86) * mm, "construction": true});
            skLineSegment(sketch, "E575.MirrorCS", {"start": v(0, 0) * mm, "end": v(9.07, -12.49) * mm, "construction": true});
            skLineSegment(sketch, "E576.MirrorCS", {"start": v(0, 0) * mm, "end": v(17.4, -8.87) * mm, "construction": true});
            skLineSegment(sketch, "E577.MirrorCS", {"start": v(-22.38, -2.35) * mm, "end": v(-24.97, -2.62) * mm, "construction": true});
            skLineSegment(sketch, "E578.MirrorCS", {"start": v(0, 0) * mm, "end": v(2.4, -15.2) * mm, "construction": true});
            skLineSegment(sketch, "E579.MirrorCS", {"start": v(0, 0) * mm, "end": v(-12.45, -12.45) * mm, "construction": true});
            skLineSegment(sketch, "E580.MirrorCS", {"start": v(0, 0) * mm, "end": v(-2.4, -15.2) * mm, "construction": true});
            skLineSegment(sketch, "E581.MirrorCS", {"start": v(0, 0) * mm, "end": v(12.45, -12.45) * mm, "construction": true});
            skLineSegment(sketch, "E582.MirrorCS", {"start": v(0, 0) * mm, "end": v(12.29, -11.07) * mm, "construction": true});
            skLineSegment(sketch, "E583.MirrorCS", {"start": v(0, 0) * mm, "end": v(-7.33, -14.38) * mm, "construction": true});
            skLineSegment(sketch, "E584.MirrorCS", {"start": v(0, 0) * mm, "end": v(-20.8, -3.3) * mm, "construction": true});
            skLineSegment(sketch, "E585.MirrorCS", {"start": v(0, 0) * mm, "end": v(-13.9, -10.1) * mm, "construction": true});
            skLineSegment(sketch, "E586.MirrorCS", {"start": v(0, 0) * mm, "end": v(19.78, -2.08) * mm, "construction": true});
            skLineSegment(sketch, "E587.MirrorCS", {"start": v(0, 0) * mm, "end": v(-12.29, -11.07) * mm, "construction": true});
            skLineSegment(sketch, "E588.MirrorCS", {"start": v(0, 0) * mm, "end": v(-4.44, -13.65) * mm, "construction": true});
            skLineSegment(sketch, "E589.MirrorCS", {"start": v(0, 0) * mm, "end": v(15.45, -8.92) * mm, "construction": true});
            skLineSegment(sketch, "E590.MirrorCS", {"start": v(0, 0) * mm, "end": v(-14.17, -11.47) * mm, "construction": true});
            skLineSegment(sketch, "E591.MirrorCS", {"start": v(0, 0) * mm, "end": v(7.5, -12.99) * mm, "construction": true});
            skLineSegment(sketch, "E592.MirrorCS", {"start": v(0, 0) * mm, "end": v(5.66, -14.76) * mm, "construction": true});
            skLineSegment(sketch, "E593.MirrorCS", {"start": v(0, 0) * mm, "end": v(13.9, -10.1) * mm, "construction": true});
            skLineSegment(sketch, "E594.MirrorCS", {"start": v(0, 0) * mm, "end": v(-19.15, -4.07) * mm, "construction": true});
            skLineSegment(sketch, "E595.MirrorCS", {"start": v(22.38, -2.35) * mm, "end": v(24.97, -2.62) * mm, "construction": true});
            skLineSegment(sketch, "E596.MirrorCS", {"start": v(0, 0) * mm, "end": v(-10.73, -13.25) * mm, "construction": true});
            skLineSegment(sketch, "E597.MirrorCS", {"start": v(0, 0) * mm, "end": v(14.17, -11.47) * mm, "construction": true});
            skLineSegment(sketch, "E598.MirrorCS", {"start": v(0, 0) * mm, "end": v(-5.66, -14.76) * mm, "construction": true});
            skLineSegment(sketch, "E599.MirrorCS", {"start": v(0, 0) * mm, "end": v(-10.67, -11.86) * mm, "construction": true});
            skLineSegment(sketch, "E600.MirrorCS", {"start": v(0, 0) * mm, "end": v(-2.94, -13.85) * mm, "construction": true});
            skLineSegment(sketch, "E601.MirrorCS", {"start": v(0, 0) * mm, "end": v(-15.84, -10.28) * mm, "construction": true});
            skLineSegment(sketch, "E602.MirrorCS", {"start": v(0, 0) * mm, "end": v(-4.03, -15.03) * mm, "construction": true});
            skLineSegment(sketch, "E603.MirrorCS", {"start": v(0, 0) * mm, "end": v(-19.78, -2.08) * mm, "construction": true});
            skLineSegment(sketch, "E604.MirrorCS", {"start": v(0, 0) * mm, "end": v(4.03, -15.03) * mm, "construction": true});
            skLineSegment(sketch, "E605.MirrorCS", {"start": v(0, 0) * mm, "end": v(16.9, -7.52) * mm, "construction": true});
            skLineSegment(sketch, "E606.MirrorCS", {"start": v(0, 0) * mm, "end": v(-19.98, -5.35) * mm, "construction": true});
            skLineSegment(sketch, "E607.MirrorCS", {"start": v(0, 0) * mm, "end": v(-1.47, -13.96) * mm, "construction": true});
            skLineSegment(sketch, "E608.MirrorCS", {"start": v(0, 0) * mm, "end": v(7.33, -14.38) * mm, "construction": true});
            skLineSegment(sketch, "E609.MirrorCS", {"start": v(0, 0) * mm, "end": v(20.8, -3.3) * mm, "construction": true});
            skLineSegment(sketch, "E610.MirrorCS", {"start": v(0, 0) * mm, "end": v(21.24, -1.11) * mm, "construction": true});
            skLineSegment(sketch, "E611.MirrorCS", {"start": v(0, 0) * mm, "end": v(-17.4, -8.87) * mm, "construction": true});
            skLineSegment(sketch, "E612.MirrorCS", {"start": v(0, 0) * mm, "end": v(-9.07, -12.49) * mm, "construction": true});
            skLineSegment(sketch, "E613.MirrorCS", {"start": v(0, 0) * mm, "end": v(5.95, -13.37) * mm, "construction": true});
            skLineSegment(sketch, "E614.MirrorCS", {"start": v(0, 0) * mm, "end": v(18.16, -5.9) * mm, "construction": true});
            skLineSegment(sketch, "E615.MirrorCS", {"start": v(0, 0) * mm, "end": v(-21.24, -1.11) * mm, "construction": true});
            skLineSegment(sketch, "E616.MirrorCS", {"start": v(0, 0) * mm, "end": v(9.02, -13.88) * mm, "construction": true});
            skSolve(sketch);
        }
        {
            var Q0;
            Q0=qCreatedBy(makeId("Front.planeOp"),FACE);
            var sketch = newSketch(context, id + "F3", { "sketchPlane" : qUnion([Q0])});
            skLineSegment(sketch, "E617.0.1", {"start": v(18.75, -0.25) * mm, "end": v(18.75, -1) * mm});
            skLineSegment(sketch, "E617.0.2", {"start": v(18.75, -1) * mm, "end": v(22.75, -1.18) * mm});
            skArc(sketch, "E617.0.3", {"start": v(22.75, -1.18) * mm, "mid": v(24.89, -1.91) * mm, "end": v(26.29, -3.69) * mm});
            skArc(sketch, "E617.0.4", {"start": v(26.29, -3.69) * mm, "mid": v(26.94, -3.96) * mm, "end": v(27.21, -3.31) * mm});
            skLineSegment(sketch, "E618.0", {"start": v(22.74, -0.42) * mm, "end": v(18.74, -0.25) * mm});
            skArc(sketch, "E618.1", {"start": v(26.98, -3.4) * mm, "mid": v(25.3, -1.29) * mm, "end": v(22.74, -0.42) * mm});
            skLineSegment(sketch, "E619", {"start": v(26.98, -3.4) * mm, "end": v(27.21, -3.31) * mm});
            skPoint(sketch, "E617.0.0.end.orphan", {"position": v(18.75, 0) * mm});
            skPoint(sketch, "E617.0.5.end.orphan", {"position": v(22.75, -0.17) * mm});
            skSolve(sketch);
        }
        {
            var Q0;
            Q0 = qSketchRegion(id + "F2", true);
            extrude(context, id + "F4", {"entities" : qUnion([Q0]), "oppositeDirection" : true, "depth" : 4 * mm});
        }
        {
            var Q0;
            Q0 = qSketchRegion(id + "F3", true);
            var Q1;
            Q1=sQuery(id+"F0.wireOp",EDGE,"E0");
            sweep(context, id + "F5", {"profiles" : qUnion([Q0]), "path" : qUnion([Q1])});
        }
        {
            var Q0;
            Q0=makeQuery(id+"F4.opExtrude","SWEPT_BODY",BODY,{"disambiguationData":[OSD([sQuery(id+"F2.wireOp",EDGE,"E25")])]});
            var Q1;
            Q1=makeQuery(id+"F4.opExtrude","SWEPT_BODY",BODY,{"disambiguationData":[OSD([sQuery(id+"F2.wireOp",EDGE,"E26")])]});
            var Q2;
            Q2=makeQuery(id+"F4.opExtrude","SWEPT_BODY",BODY,{"disambiguationData":[OSD([sQuery(id+"F2.wireOp",EDGE,"E100")])]});
            var Q3;
            Q3=makeQuery(id+"F4.opExtrude","SWEPT_BODY",BODY,{"disambiguationData":[OSD([sQuery(id+"F2.wireOp",EDGE,"E101")])]});
            var Q4;
            Q4=makeQuery(id+"F4.opExtrude","SWEPT_BODY",BODY,{"disambiguationData":[OSD([sQuery(id+"F2.wireOp",EDGE,"E102")])]});
            var Q5;
            Q5=makeQuery(id+"F4.opExtrude","SWEPT_BODY",BODY,{"disambiguationData":[OSD([sQuery(id+"F2.wireOp",EDGE,"E103")])]});
            var Q6;
            Q6=makeQuery(id+"F4.opExtrude","SWEPT_BODY",BODY,{"disambiguationData":[OSD([sQuery(id+"F2.wireOp",EDGE,"E104")])]});
            var Q7;
            Q7=makeQuery(id+"F4.opExtrude","SWEPT_BODY",BODY,{"disambiguationData":[OSD([sQuery(id+"F2.wireOp",EDGE,"E105")])]});
            var Q8;
            Q8=makeQuery(id+"F4.opExtrude","SWEPT_BODY",BODY,{"disambiguationData":[OSD([sQuery(id+"F2.wireOp",EDGE,"E106")])]});
            var Q9;
            Q9=makeQuery(id+"F4.opExtrude","SWEPT_BODY",BODY,{"disambiguationData":[OSD([sQuery(id+"F2.wireOp",EDGE,"E107")])]});
            var Q10;
            Q10=makeQuery(id+"F4.opExtrude","SWEPT_BODY",BODY,{"disambiguationData":[OSD([sQuery(id+"F2.wireOp",EDGE,"E108")])]});
            var Q11;
            Q11=makeQuery(id+"F4.opExtrude","SWEPT_BODY",BODY,{"disambiguationData":[OSD([sQuery(id+"F2.wireOp",EDGE,"E109")])]});
            var Q12;
            Q12=makeQuery(id+"F4.opExtrude","SWEPT_BODY",BODY,{"disambiguationData":[OSD([sQuery(id+"F2.wireOp",EDGE,"E110")])]});
            var Q13;
            Q13=makeQuery(id+"F4.opExtrude","SWEPT_BODY",BODY,{"disambiguationData":[OSD([sQuery(id+"F2.wireOp",EDGE,"E111")])]});
            var Q14;
            Q14=makeQuery(id+"F4.opExtrude","SWEPT_BODY",BODY,{"disambiguationData":[OSD([sQuery(id+"F2.wireOp",EDGE,"E112")])]});
            var Q15;
            Q15=makeQuery(id+"F4.opExtrude","SWEPT_BODY",BODY,{"disambiguationData":[OSD([sQuery(id+"F2.wireOp",EDGE,"E113")])]});
            var Q16;
            Q16=makeQuery(id+"F4.opExtrude","SWEPT_BODY",BODY,{"disambiguationData":[OSD([sQuery(id+"F2.wireOp",EDGE,"E117")])]});
            var Q17;
            Q17=makeQuery(id+"F4.opExtrude","SWEPT_BODY",BODY,{"disambiguationData":[OSD([sQuery(id+"F2.wireOp",EDGE,"E118")])]});
            var Q18;
            Q18=makeQuery(id+"F4.opExtrude","SWEPT_BODY",BODY,{"disambiguationData":[OSD([sQuery(id+"F2.wireOp",EDGE,"E119")])]});
            var Q19;
            Q19=makeQuery(id+"F4.opExtrude","SWEPT_BODY",BODY,{"disambiguationData":[OSD([sQuery(id+"F2.wireOp",EDGE,"E120")])]});
            var Q20;
            Q20=makeQuery(id+"F4.opExtrude","SWEPT_BODY",BODY,{"disambiguationData":[OSD([sQuery(id+"F2.wireOp",EDGE,"E121")])]});
            var Q21;
            Q21=makeQuery(id+"F4.opExtrude","SWEPT_BODY",BODY,{"disambiguationData":[OSD([sQuery(id+"F2.wireOp",EDGE,"E122")])]});
            var Q22;
            Q22=makeQuery(id+"F4.opExtrude","SWEPT_BODY",BODY,{"disambiguationData":[OSD([sQuery(id+"F2.wireOp",EDGE,"E123")])]});
            var Q23;
            Q23=makeQuery(id+"F4.opExtrude","SWEPT_BODY",BODY,{"disambiguationData":[OSD([sQuery(id+"F2.wireOp",EDGE,"E124")])]});
            var Q24;
            Q24=makeQuery(id+"F4.opExtrude","SWEPT_BODY",BODY,{"disambiguationData":[OSD([sQuery(id+"F2.wireOp",EDGE,"E125")])]});
            var Q25;
            Q25=makeQuery(id+"F4.opExtrude","SWEPT_BODY",BODY,{"disambiguationData":[OSD([sQuery(id+"F2.wireOp",EDGE,"E126")])]});
            var Q26;
            Q26=makeQuery(id+"F4.opExtrude","SWEPT_BODY",BODY,{"disambiguationData":[OSD([sQuery(id+"F2.wireOp",EDGE,"E127")])]});
            var Q27;
            Q27=makeQuery(id+"F4.opExtrude","SWEPT_BODY",BODY,{"disambiguationData":[OSD([sQuery(id+"F2.wireOp",EDGE,"E128")])]});
            var Q28;
            Q28=makeQuery(id+"F4.opExtrude","SWEPT_BODY",BODY,{"disambiguationData":[OSD([sQuery(id+"F2.wireOp",EDGE,"E129")])]});
            var Q29;
            Q29=makeQuery(id+"F4.opExtrude","SWEPT_BODY",BODY,{"disambiguationData":[OSD([sQuery(id+"F2.wireOp",EDGE,"E130")])]});
            var Q30;
            Q30=makeQuery(id+"F4.opExtrude","SWEPT_BODY",BODY,{"disambiguationData":[OSD([sQuery(id+"F2.wireOp",EDGE,"E131")])]});
            var Q31;
            Q31=makeQuery(id+"F4.opExtrude","SWEPT_BODY",BODY,{"disambiguationData":[OSD([sQuery(id+"F2.wireOp",EDGE,"E132")])]});
            var Q32;
            Q32=makeQuery(id+"F4.opExtrude","SWEPT_BODY",BODY,{"disambiguationData":[OSD([sQuery(id+"F2.wireOp",EDGE,"E133")])]});
            var Q33;
            Q33=makeQuery(id+"F4.opExtrude","SWEPT_BODY",BODY,{"disambiguationData":[OSD([sQuery(id+"F2.wireOp",EDGE,"E134")])]});
            var Q34;
            Q34=makeQuery(id+"F4.opExtrude","SWEPT_BODY",BODY,{"disambiguationData":[OSD([sQuery(id+"F2.wireOp",EDGE,"E135")])]});
            var Q35;
            Q35=makeQuery(id+"F4.opExtrude","SWEPT_BODY",BODY,{"disambiguationData":[OSD([sQuery(id+"F2.wireOp",EDGE,"E136")])]});
            var Q36;
            Q36=makeQuery(id+"F4.opExtrude","SWEPT_BODY",BODY,{"disambiguationData":[OSD([sQuery(id+"F2.wireOp",EDGE,"E137")])]});
            var Q37;
            Q37=makeQuery(id+"F4.opExtrude","SWEPT_BODY",BODY,{"disambiguationData":[OSD([sQuery(id+"F2.wireOp",EDGE,"E138")])]});
            var Q38;
            Q38=makeQuery(id+"F4.opExtrude","SWEPT_BODY",BODY,{"disambiguationData":[OSD([sQuery(id+"F2.wireOp",EDGE,"E139")])]});
            var Q39;
            Q39=makeQuery(id+"F4.opExtrude","SWEPT_BODY",BODY,{"disambiguationData":[OSD([sQuery(id+"F2.wireOp",EDGE,"E140")])]});
            var Q40;
            Q40=makeQuery(id+"F4.opExtrude","SWEPT_BODY",BODY,{"disambiguationData":[OSD([sQuery(id+"F2.wireOp",EDGE,"E141")])]});
            var Q41;
            Q41=makeQuery(id+"F4.opExtrude","SWEPT_BODY",BODY,{"disambiguationData":[OSD([sQuery(id+"F2.wireOp",EDGE,"E142")])]});
            var Q42;
            Q42=makeQuery(id+"F4.opExtrude","SWEPT_BODY",BODY,{"disambiguationData":[OSD([sQuery(id+"F2.wireOp",EDGE,"E143")])]});
            var Q43;
            Q43=makeQuery(id+"F4.opExtrude","SWEPT_BODY",BODY,{"disambiguationData":[OSD([sQuery(id+"F2.wireOp",EDGE,"E144")])]});
            var Q44;
            Q44=makeQuery(id+"F4.opExtrude","SWEPT_BODY",BODY,{"disambiguationData":[OSD([sQuery(id+"F2.wireOp",EDGE,"E145")])]});
            var Q45;
            Q45=makeQuery(id+"F4.opExtrude","SWEPT_BODY",BODY,{"disambiguationData":[OSD([sQuery(id+"F2.wireOp",EDGE,"E146")])]});
            var Q46;
            Q46=makeQuery(id+"F4.opExtrude","SWEPT_BODY",BODY,{"disambiguationData":[OSD([sQuery(id+"F2.wireOp",EDGE,"E147")])]});
            var Q47;
            Q47=makeQuery(id+"F4.opExtrude","SWEPT_BODY",BODY,{"disambiguationData":[OSD([sQuery(id+"F2.wireOp",EDGE,"E148")])]});
            var Q48;
            Q48=makeQuery(id+"F4.opExtrude","SWEPT_BODY",BODY,{"disambiguationData":[OSD([sQuery(id+"F2.wireOp",EDGE,"E149")])]});
            var Q49;
            Q49=makeQuery(id+"F4.opExtrude","SWEPT_BODY",BODY,{"disambiguationData":[OSD([sQuery(id+"F2.wireOp",EDGE,"E150")])]});
            var Q50;
            Q50=makeQuery(id+"F4.opExtrude","SWEPT_BODY",BODY,{"disambiguationData":[OSD([sQuery(id+"F2.wireOp",EDGE,"E151")])]});
            var Q51;
            Q51=makeQuery(id+"F4.opExtrude","SWEPT_BODY",BODY,{"disambiguationData":[OSD([sQuery(id+"F2.wireOp",EDGE,"E152")])]});
            var Q52;
            Q52=makeQuery(id+"F4.opExtrude","SWEPT_BODY",BODY,{"disambiguationData":[OSD([sQuery(id+"F2.wireOp",EDGE,"E153")])]});
            var Q53;
            Q53=makeQuery(id+"F4.opExtrude","SWEPT_BODY",BODY,{"disambiguationData":[OSD([sQuery(id+"F2.wireOp",EDGE,"E154")])]});
            var Q54;
            Q54=makeQuery(id+"F4.opExtrude","SWEPT_BODY",BODY,{"disambiguationData":[OSD([sQuery(id+"F2.wireOp",EDGE,"E155")])]});
            var Q55;
            Q55=makeQuery(id+"F4.opExtrude","SWEPT_BODY",BODY,{"disambiguationData":[OSD([sQuery(id+"F2.wireOp",EDGE,"E156")])]});
            var Q56;
            Q56=makeQuery(id+"F4.opExtrude","SWEPT_BODY",BODY,{"disambiguationData":[OSD([sQuery(id+"F2.wireOp",EDGE,"E157")])]});
            var Q57;
            Q57=makeQuery(id+"F4.opExtrude","SWEPT_BODY",BODY,{"disambiguationData":[OSD([sQuery(id+"F2.wireOp",EDGE,"E158")])]});
            var Q58;
            Q58=makeQuery(id+"F4.opExtrude","SWEPT_BODY",BODY,{"disambiguationData":[OSD([sQuery(id+"F2.wireOp",EDGE,"E159")])]});
            var Q59;
            Q59=makeQuery(id+"F4.opExtrude","SWEPT_BODY",BODY,{"disambiguationData":[OSD([sQuery(id+"F2.wireOp",EDGE,"E160")])]});
            var Q60;
            Q60=makeQuery(id+"F4.opExtrude","SWEPT_BODY",BODY,{"disambiguationData":[OSD([sQuery(id+"F2.wireOp",EDGE,"E161")])]});
            var Q61;
            Q61=makeQuery(id+"F4.opExtrude","SWEPT_BODY",BODY,{"disambiguationData":[OSD([sQuery(id+"F2.wireOp",EDGE,"E162")])]});
            var Q62;
            Q62=makeQuery(id+"F4.opExtrude","SWEPT_BODY",BODY,{"disambiguationData":[OSD([sQuery(id+"F2.wireOp",EDGE,"E163")])]});
            var Q63;
            Q63=makeQuery(id+"F4.opExtrude","SWEPT_BODY",BODY,{"disambiguationData":[OSD([sQuery(id+"F2.wireOp",EDGE,"E164")])]});
            var Q64;
            Q64=makeQuery(id+"F4.opExtrude","SWEPT_BODY",BODY,{"disambiguationData":[OSD([sQuery(id+"F2.wireOp",EDGE,"E165")])]});
            var Q65;
            Q65=makeQuery(id+"F4.opExtrude","SWEPT_BODY",BODY,{"disambiguationData":[OSD([sQuery(id+"F2.wireOp",EDGE,"E166")])]});
            var Q66;
            Q66=makeQuery(id+"F4.opExtrude","SWEPT_BODY",BODY,{"disambiguationData":[OSD([sQuery(id+"F2.wireOp",EDGE,"E167")])]});
            var Q67;
            Q67=makeQuery(id+"F4.opExtrude","SWEPT_BODY",BODY,{"disambiguationData":[OSD([sQuery(id+"F2.wireOp",EDGE,"E168")])]});
            var Q68;
            Q68=makeQuery(id+"F4.opExtrude","SWEPT_BODY",BODY,{"disambiguationData":[OSD([sQuery(id+"F2.wireOp",EDGE,"E169")])]});
            var Q69;
            Q69=makeQuery(id+"F4.opExtrude","SWEPT_BODY",BODY,{"disambiguationData":[OSD([sQuery(id+"F2.wireOp",EDGE,"E170")])]});
            var Q70;
            Q70=makeQuery(id+"F4.opExtrude","SWEPT_BODY",BODY,{"disambiguationData":[OSD([sQuery(id+"F2.wireOp",EDGE,"E171")])]});
            var Q71;
            Q71=makeQuery(id+"F4.opExtrude","SWEPT_BODY",BODY,{"disambiguationData":[OSD([sQuery(id+"F2.wireOp",EDGE,"E172")])]});
            var Q72;
            Q72=makeQuery(id+"F4.opExtrude","SWEPT_BODY",BODY,{"disambiguationData":[OSD([sQuery(id+"F2.wireOp",EDGE,"E173.MirrorC")])]});
            var Q73;
            Q73=makeQuery(id+"F4.opExtrude","SWEPT_BODY",BODY,{"disambiguationData":[OSD([sQuery(id+"F2.wireOp",EDGE,"E174.MirrorC")])]});
            var Q74;
            Q74=makeQuery(id+"F4.opExtrude","SWEPT_BODY",BODY,{"disambiguationData":[OSD([sQuery(id+"F2.wireOp",EDGE,"E176.MirrorC")])]});
            var Q75;
            Q75=makeQuery(id+"F4.opExtrude","SWEPT_BODY",BODY,{"disambiguationData":[OSD([sQuery(id+"F2.wireOp",EDGE,"E179.MirrorC")])]});
            var Q76;
            Q76=makeQuery(id+"F4.opExtrude","SWEPT_BODY",BODY,{"disambiguationData":[OSD([sQuery(id+"F2.wireOp",EDGE,"E180.MirrorC")])]});
            var Q77;
            Q77=makeQuery(id+"F4.opExtrude","SWEPT_BODY",BODY,{"disambiguationData":[OSD([sQuery(id+"F2.wireOp",EDGE,"E181.MirrorC")])]});
            var Q78;
            Q78=makeQuery(id+"F4.opExtrude","SWEPT_BODY",BODY,{"disambiguationData":[OSD([sQuery(id+"F2.wireOp",EDGE,"E182.MirrorC")])]});
            var Q79;
            Q79=makeQuery(id+"F4.opExtrude","SWEPT_BODY",BODY,{"disambiguationData":[OSD([sQuery(id+"F2.wireOp",EDGE,"E185.MirrorC")])]});
            var Q80;
            Q80=makeQuery(id+"F4.opExtrude","SWEPT_BODY",BODY,{"disambiguationData":[OSD([sQuery(id+"F2.wireOp",EDGE,"E17")])]});
            var Q81;
            Q81=makeQuery(id+"F4.opExtrude","SWEPT_BODY",BODY,{"disambiguationData":[OSD([sQuery(id+"F2.wireOp",EDGE,"E18")])]});
            var Q82;
            Q82=makeQuery(id+"F4.opExtrude","SWEPT_BODY",BODY,{"disambiguationData":[OSD([sQuery(id+"F2.wireOp",EDGE,"E186.MirrorC")])]});
            var Q83;
            Q83=makeQuery(id+"F4.opExtrude","SWEPT_BODY",BODY,{"disambiguationData":[OSD([sQuery(id+"F2.wireOp",EDGE,"E187.MirrorC")])]});
            var Q84;
            Q84=makeQuery(id+"F4.opExtrude","SWEPT_BODY",BODY,{"disambiguationData":[OSD([sQuery(id+"F2.wireOp",EDGE,"E190.MirrorC")])]});
            var Q85;
            Q85=makeQuery(id+"F4.opExtrude","SWEPT_BODY",BODY,{"disambiguationData":[OSD([sQuery(id+"F2.wireOp",EDGE,"E192.MirrorC")])]});
            var Q86;
            Q86=makeQuery(id+"F4.opExtrude","SWEPT_BODY",BODY,{"disambiguationData":[OSD([sQuery(id+"F2.wireOp",EDGE,"E195.MirrorC")])]});
            var Q87;
            Q87=makeQuery(id+"F4.opExtrude","SWEPT_BODY",BODY,{"disambiguationData":[OSD([sQuery(id+"F2.wireOp",EDGE,"E198.MirrorC")])]});
            var Q88;
            Q88=makeQuery(id+"F4.opExtrude","SWEPT_BODY",BODY,{"disambiguationData":[OSD([sQuery(id+"F2.wireOp",EDGE,"E199.MirrorC")])]});
            var Q89;
            Q89=makeQuery(id+"F4.opExtrude","SWEPT_BODY",BODY,{"disambiguationData":[OSD([sQuery(id+"F2.wireOp",EDGE,"E201.MirrorC")])]});
            var Q90;
            Q90=makeQuery(id+"F4.opExtrude","SWEPT_BODY",BODY,{"disambiguationData":[OSD([sQuery(id+"F2.wireOp",EDGE,"E202.MirrorC")])]});
            var Q91;
            Q91=makeQuery(id+"F4.opExtrude","SWEPT_BODY",BODY,{"disambiguationData":[OSD([sQuery(id+"F2.wireOp",EDGE,"E203.MirrorC")])]});
            var Q92;
            Q92=makeQuery(id+"F4.opExtrude","SWEPT_BODY",BODY,{"disambiguationData":[OSD([sQuery(id+"F2.wireOp",EDGE,"E204.MirrorC")])]});
            var Q93;
            Q93=makeQuery(id+"F4.opExtrude","SWEPT_BODY",BODY,{"disambiguationData":[OSD([sQuery(id+"F2.wireOp",EDGE,"E211.MirrorC")])]});
            var Q94;
            Q94=makeQuery(id+"F4.opExtrude","SWEPT_BODY",BODY,{"disambiguationData":[OSD([sQuery(id+"F2.wireOp",EDGE,"E212.MirrorC")])]});
            var Q95;
            Q95=makeQuery(id+"F4.opExtrude","SWEPT_BODY",BODY,{"disambiguationData":[OSD([sQuery(id+"F2.wireOp",EDGE,"E218.MirrorC")])]});
            var Q96;
            Q96=makeQuery(id+"F4.opExtrude","SWEPT_BODY",BODY,{"disambiguationData":[OSD([sQuery(id+"F2.wireOp",EDGE,"E224.MirrorC")])]});
            var Q97;
            Q97=makeQuery(id+"F4.opExtrude","SWEPT_BODY",BODY,{"disambiguationData":[OSD([sQuery(id+"F2.wireOp",EDGE,"E226.MirrorC")])]});
            var Q98;
            Q98=makeQuery(id+"F4.opExtrude","SWEPT_BODY",BODY,{"disambiguationData":[OSD([sQuery(id+"F2.wireOp",EDGE,"E227.MirrorC")])]});
            var Q99;
            Q99=makeQuery(id+"F4.opExtrude","SWEPT_BODY",BODY,{"disambiguationData":[OSD([sQuery(id+"F2.wireOp",EDGE,"E229.MirrorC")])]});
            var Q100;
            Q100=makeQuery(id+"F4.opExtrude","SWEPT_BODY",BODY,{"disambiguationData":[OSD([sQuery(id+"F2.wireOp",EDGE,"E230.MirrorC")])]});
            var Q101;
            Q101=makeQuery(id+"F4.opExtrude","SWEPT_BODY",BODY,{"disambiguationData":[OSD([sQuery(id+"F2.wireOp",EDGE,"E231.MirrorC")])]});
            var Q102;
            Q102=makeQuery(id+"F4.opExtrude","SWEPT_BODY",BODY,{"disambiguationData":[OSD([sQuery(id+"F2.wireOp",EDGE,"E233.MirrorC")])]});
            var Q103;
            Q103=makeQuery(id+"F4.opExtrude","SWEPT_BODY",BODY,{"disambiguationData":[OSD([sQuery(id+"F2.wireOp",EDGE,"E234.MirrorC")])]});
            var Q104;
            Q104=makeQuery(id+"F4.opExtrude","SWEPT_BODY",BODY,{"disambiguationData":[OSD([sQuery(id+"F2.wireOp",EDGE,"E235.MirrorC")])]});
            var Q105;
            Q105=makeQuery(id+"F4.opExtrude","SWEPT_BODY",BODY,{"disambiguationData":[OSD([sQuery(id+"F2.wireOp",EDGE,"E240.MirrorC")])]});
            var Q106;
            Q106=makeQuery(id+"F4.opExtrude","SWEPT_BODY",BODY,{"disambiguationData":[OSD([sQuery(id+"F2.wireOp",EDGE,"E243.MirrorC")])]});
            var Q107;
            Q107=makeQuery(id+"F4.opExtrude","SWEPT_BODY",BODY,{"disambiguationData":[OSD([sQuery(id+"F2.wireOp",EDGE,"E245.MirrorC")])]});
            var Q108;
            Q108=makeQuery(id+"F4.opExtrude","SWEPT_BODY",BODY,{"disambiguationData":[OSD([sQuery(id+"F2.wireOp",EDGE,"E246.MirrorC")])]});
            var Q109;
            Q109=makeQuery(id+"F4.opExtrude","SWEPT_BODY",BODY,{"disambiguationData":[OSD([sQuery(id+"F2.wireOp",EDGE,"E248.MirrorC")])]});
            var Q110;
            Q110=makeQuery(id+"F4.opExtrude","SWEPT_BODY",BODY,{"disambiguationData":[OSD([sQuery(id+"F2.wireOp",EDGE,"E249.MirrorC")])]});
            var Q111;
            Q111=makeQuery(id+"F4.opExtrude","SWEPT_BODY",BODY,{"disambiguationData":[OSD([sQuery(id+"F2.wireOp",EDGE,"E252.MirrorC")])]});
            var Q112;
            Q112=makeQuery(id+"F4.opExtrude","SWEPT_BODY",BODY,{"disambiguationData":[OSD([sQuery(id+"F2.wireOp",EDGE,"E254.MirrorC")])]});
            var Q113;
            Q113=makeQuery(id+"F4.opExtrude","SWEPT_BODY",BODY,{"disambiguationData":[OSD([sQuery(id+"F2.wireOp",EDGE,"E255.MirrorC")])]});
            var Q114;
            Q114=makeQuery(id+"F4.opExtrude","SWEPT_BODY",BODY,{"disambiguationData":[OSD([sQuery(id+"F2.wireOp",EDGE,"E256.MirrorC")])]});
            var Q115;
            Q115=makeQuery(id+"F4.opExtrude","SWEPT_BODY",BODY,{"disambiguationData":[OSD([sQuery(id+"F2.wireOp",EDGE,"E258.MirrorC")])]});
            var Q116;
            Q116=makeQuery(id+"F4.opExtrude","SWEPT_BODY",BODY,{"disambiguationData":[OSD([sQuery(id+"F2.wireOp",EDGE,"E265.MirrorC")])]});
            var Q117;
            Q117=makeQuery(id+"F4.opExtrude","SWEPT_BODY",BODY,{"disambiguationData":[OSD([sQuery(id+"F2.wireOp",EDGE,"E267.MirrorC")])]});
            var Q118;
            Q118=makeQuery(id+"F4.opExtrude","SWEPT_BODY",BODY,{"disambiguationData":[OSD([sQuery(id+"F2.wireOp",EDGE,"E268.MirrorC")])]});
            var Q119;
            Q119=makeQuery(id+"F4.opExtrude","SWEPT_BODY",BODY,{"disambiguationData":[OSD([sQuery(id+"F2.wireOp",EDGE,"E269.MirrorC")])]});
            var Q120;
            Q120=makeQuery(id+"F4.opExtrude","SWEPT_BODY",BODY,{"disambiguationData":[OSD([sQuery(id+"F2.wireOp",EDGE,"E270.MirrorC")])]});
            var Q121;
            Q121=makeQuery(id+"F4.opExtrude","SWEPT_BODY",BODY,{"disambiguationData":[OSD([sQuery(id+"F2.wireOp",EDGE,"E271.MirrorC")])]});
            var Q122;
            Q122=makeQuery(id+"F4.opExtrude","SWEPT_BODY",BODY,{"disambiguationData":[OSD([sQuery(id+"F2.wireOp",EDGE,"E275.MirrorC")])]});
            var Q123;
            Q123=makeQuery(id+"F4.opExtrude","SWEPT_BODY",BODY,{"disambiguationData":[OSD([sQuery(id+"F2.wireOp",EDGE,"E277.MirrorC")])]});
            var Q124;
            Q124=makeQuery(id+"F4.opExtrude","SWEPT_BODY",BODY,{"disambiguationData":[OSD([sQuery(id+"F2.wireOp",EDGE,"E280.MirrorC")])]});
            var Q125;
            Q125=makeQuery(id+"F4.opExtrude","SWEPT_BODY",BODY,{"disambiguationData":[OSD([sQuery(id+"F2.wireOp",EDGE,"E282.MirrorC")])]});
            var Q126;
            Q126=makeQuery(id+"F4.opExtrude","SWEPT_BODY",BODY,{"disambiguationData":[OSD([sQuery(id+"F2.wireOp",EDGE,"E285.MirrorC")])]});
            var Q127;
            Q127=makeQuery(id+"F4.opExtrude","SWEPT_BODY",BODY,{"disambiguationData":[OSD([sQuery(id+"F2.wireOp",EDGE,"E287.MirrorC")])]});
            var Q128;
            Q128=makeQuery(id+"F4.opExtrude","SWEPT_BODY",BODY,{"disambiguationData":[OSD([sQuery(id+"F2.wireOp",EDGE,"E288.MirrorC")])]});
            var Q129;
            Q129=makeQuery(id+"F4.opExtrude","SWEPT_BODY",BODY,{"disambiguationData":[OSD([sQuery(id+"F2.wireOp",EDGE,"E289.MirrorC")])]});
            var Q130;
            Q130=makeQuery(id+"F4.opExtrude","SWEPT_BODY",BODY,{"disambiguationData":[OSD([sQuery(id+"F2.wireOp",EDGE,"E291.MirrorC")])]});
            var Q131;
            Q131=makeQuery(id+"F4.opExtrude","SWEPT_BODY",BODY,{"disambiguationData":[OSD([sQuery(id+"F2.wireOp",EDGE,"E292.MirrorC")])]});
            var Q132;
            Q132=makeQuery(id+"F4.opExtrude","SWEPT_BODY",BODY,{"disambiguationData":[OSD([sQuery(id+"F2.wireOp",EDGE,"E295.MirrorC")])]});
            var Q133;
            Q133=makeQuery(id+"F4.opExtrude","SWEPT_BODY",BODY,{"disambiguationData":[OSD([sQuery(id+"F2.wireOp",EDGE,"E297.MirrorC")])]});
            var Q134;
            Q134=makeQuery(id+"F4.opExtrude","SWEPT_BODY",BODY,{"disambiguationData":[OSD([sQuery(id+"F2.wireOp",EDGE,"E298.MirrorC")])]});
            var Q135;
            Q135=makeQuery(id+"F4.opExtrude","SWEPT_BODY",BODY,{"disambiguationData":[OSD([sQuery(id+"F2.wireOp",EDGE,"E299.MirrorC")])]});
            var Q136;
            Q136=makeQuery(id+"F4.opExtrude","SWEPT_BODY",BODY,{"disambiguationData":[OSD([sQuery(id+"F2.wireOp",EDGE,"E301.MirrorC")])]});
            var Q137;
            Q137=makeQuery(id+"F4.opExtrude","SWEPT_BODY",BODY,{"disambiguationData":[OSD([sQuery(id+"F2.wireOp",EDGE,"E19")])]});
            var Q138;
            Q138=makeQuery(id+"F4.opExtrude","SWEPT_BODY",BODY,{"disambiguationData":[OSD([sQuery(id+"F2.wireOp",EDGE,"E303.MirrorC")])]});
            var Q139;
            Q139=makeQuery(id+"F4.opExtrude","SWEPT_BODY",BODY,{"disambiguationData":[OSD([sQuery(id+"F2.wireOp",EDGE,"E304.MirrorC")])]});
            var Q140;
            Q140=makeQuery(id+"F4.opExtrude","SWEPT_BODY",BODY,{"disambiguationData":[OSD([sQuery(id+"F2.wireOp",EDGE,"E308.MirrorC")])]});
            var Q141;
            Q141=makeQuery(id+"F4.opExtrude","SWEPT_BODY",BODY,{"disambiguationData":[OSD([sQuery(id+"F2.wireOp",EDGE,"E311.MirrorC")])]});
            var Q142;
            Q142=makeQuery(id+"F4.opExtrude","SWEPT_BODY",BODY,{"disambiguationData":[OSD([sQuery(id+"F2.wireOp",EDGE,"E312.MirrorC")])]});
            var Q143;
            Q143=makeQuery(id+"F4.opExtrude","SWEPT_BODY",BODY,{"disambiguationData":[OSD([sQuery(id+"F2.wireOp",EDGE,"E315.MirrorC")])]});
            var Q144;
            Q144=makeQuery(id+"F4.opExtrude","SWEPT_BODY",BODY,{"disambiguationData":[OSD([sQuery(id+"F2.wireOp",EDGE,"E317.MirrorC")])]});
            var Q145;
            Q145=makeQuery(id+"F4.opExtrude","SWEPT_BODY",BODY,{"disambiguationData":[OSD([sQuery(id+"F2.wireOp",EDGE,"E319.MirrorC")])]});
            var Q146;
            Q146=makeQuery(id+"F4.opExtrude","SWEPT_BODY",BODY,{"disambiguationData":[OSD([sQuery(id+"F2.wireOp",EDGE,"E320.MirrorC")])]});
            var Q147;
            Q147=makeQuery(id+"F4.opExtrude","SWEPT_BODY",BODY,{"disambiguationData":[OSD([sQuery(id+"F2.wireOp",EDGE,"E323.MirrorC")])]});
            var Q148;
            Q148=makeQuery(id+"F4.opExtrude","SWEPT_BODY",BODY,{"disambiguationData":[OSD([sQuery(id+"F2.wireOp",EDGE,"E324.MirrorC")])]});
            var Q149;
            Q149=makeQuery(id+"F4.opExtrude","SWEPT_BODY",BODY,{"disambiguationData":[OSD([sQuery(id+"F2.wireOp",EDGE,"E325.MirrorC")])]});
            var Q150;
            Q150=makeQuery(id+"F4.opExtrude","SWEPT_BODY",BODY,{"disambiguationData":[OSD([sQuery(id+"F2.wireOp",EDGE,"E247.MirrorC")])]});
            var Q151;
            Q151=makeQuery(id+"F4.opExtrude","SWEPT_BODY",BODY,{"disambiguationData":[OSD([sQuery(id+"F2.wireOp",EDGE,"E221.MirrorC")])]});
            var Q152;
            Q152=makeQuery(id+"F4.opExtrude","SWEPT_BODY",BODY,{"disambiguationData":[OSD([sQuery(id+"F2.wireOp",EDGE,"E327.MirrorC")])]});
            var Q153;
            Q153=makeQuery(id+"F4.opExtrude","SWEPT_BODY",BODY,{"disambiguationData":[OSD([sQuery(id+"F2.wireOp",EDGE,"E328.MirrorC")])]});
            var Q154;
            Q154=makeQuery(id+"F4.opExtrude","SWEPT_BODY",BODY,{"disambiguationData":[OSD([sQuery(id+"F2.wireOp",EDGE,"E329.MirrorC")])]});
            var Q155;
            Q155=makeQuery(id+"F4.opExtrude","SWEPT_BODY",BODY,{"disambiguationData":[OSD([sQuery(id+"F2.wireOp",EDGE,"E330.MirrorC")])]});
            var Q156;
            Q156=makeQuery(id+"F4.opExtrude","SWEPT_BODY",BODY,{"disambiguationData":[OSD([sQuery(id+"F2.wireOp",EDGE,"E331.MirrorC")])]});
            var Q157;
            Q157=makeQuery(id+"F4.opExtrude","SWEPT_BODY",BODY,{"disambiguationData":[OSD([sQuery(id+"F2.wireOp",EDGE,"E333.MirrorC")])]});
            var Q158;
            Q158=makeQuery(id+"F4.opExtrude","SWEPT_BODY",BODY,{"disambiguationData":[OSD([sQuery(id+"F2.wireOp",EDGE,"E305.MirrorC")])]});
            var Q159;
            Q159=makeQuery(id+"F4.opExtrude","SWEPT_BODY",BODY,{"disambiguationData":[OSD([sQuery(id+"F2.wireOp",EDGE,"E334.MirrorC")])]});
            var Q160;
            Q160=makeQuery(id+"F4.opExtrude","SWEPT_BODY",BODY,{"disambiguationData":[OSD([sQuery(id+"F2.wireOp",EDGE,"E335.MirrorC")])]});
            var Q161;
            Q161=makeQuery(id+"F4.opExtrude","SWEPT_BODY",BODY,{"disambiguationData":[OSD([sQuery(id+"F2.wireOp",EDGE,"E336.MirrorC")])]});
            var Q162;
            Q162=makeQuery(id+"F4.opExtrude","SWEPT_BODY",BODY,{"disambiguationData":[OSD([sQuery(id+"F2.wireOp",EDGE,"E337.MirrorC")])]});
            var Q163;
            Q163=makeQuery(id+"F4.opExtrude","SWEPT_BODY",BODY,{"disambiguationData":[OSD([sQuery(id+"F2.wireOp",EDGE,"E338.MirrorC")])]});
            var Q164;
            Q164=makeQuery(id+"F4.opExtrude","SWEPT_BODY",BODY,{"disambiguationData":[OSD([sQuery(id+"F2.wireOp",EDGE,"E340.MirrorC")])]});
            var Q165;
            Q165=makeQuery(id+"F4.opExtrude","SWEPT_BODY",BODY,{"disambiguationData":[OSD([sQuery(id+"F2.wireOp",EDGE,"E341.MirrorC")])]});
            var Q166;
            Q166=makeQuery(id+"F4.opExtrude","SWEPT_BODY",BODY,{"disambiguationData":[OSD([sQuery(id+"F2.wireOp",EDGE,"E344.MirrorC")])]});
            var Q167;
            Q167=makeQuery(id+"F4.opExtrude","SWEPT_BODY",BODY,{"disambiguationData":[OSD([sQuery(id+"F2.wireOp",EDGE,"E345.MirrorC")])]});
            var Q168;
            Q168=makeQuery(id+"F4.opExtrude","SWEPT_BODY",BODY,{"disambiguationData":[OSD([sQuery(id+"F2.wireOp",EDGE,"E346.MirrorC")])]});
            var Q169;
            Q169=makeQuery(id+"F4.opExtrude","SWEPT_BODY",BODY,{"disambiguationData":[OSD([sQuery(id+"F2.wireOp",EDGE,"E347.MirrorC")])]});
            var Q170;
            Q170=makeQuery(id+"F4.opExtrude","SWEPT_BODY",BODY,{"disambiguationData":[OSD([sQuery(id+"F2.wireOp",EDGE,"E349.MirrorC")])]});
            var Q171;
            Q171=makeQuery(id+"F4.opExtrude","SWEPT_BODY",BODY,{"disambiguationData":[OSD([sQuery(id+"F2.wireOp",EDGE,"E351.MirrorC")])]});
            var Q172;
            Q172=makeQuery(id+"F4.opExtrude","SWEPT_BODY",BODY,{"disambiguationData":[OSD([sQuery(id+"F2.wireOp",EDGE,"E353.MirrorC")])]});
            var Q173;
            Q173=makeQuery(id+"F4.opExtrude","SWEPT_BODY",BODY,{"disambiguationData":[OSD([sQuery(id+"F2.wireOp",EDGE,"E354.MirrorC")])]});
            var Q174;
            Q174=makeQuery(id+"F4.opExtrude","SWEPT_BODY",BODY,{"disambiguationData":[OSD([sQuery(id+"F2.wireOp",EDGE,"E356.MirrorC")])]});
            var Q175;
            Q175=makeQuery(id+"F4.opExtrude","SWEPT_BODY",BODY,{"disambiguationData":[OSD([sQuery(id+"F2.wireOp",EDGE,"E357.MirrorC")])]});
            var Q176;
            Q176=makeQuery(id+"F4.opExtrude","SWEPT_BODY",BODY,{"disambiguationData":[OSD([sQuery(id+"F2.wireOp",EDGE,"E359.MirrorC")])]});
            var Q177;
            Q177=makeQuery(id+"F4.opExtrude","SWEPT_BODY",BODY,{"disambiguationData":[OSD([sQuery(id+"F2.wireOp",EDGE,"E116")])]});
            var Q178;
            Q178=makeQuery(id+"F4.opExtrude","SWEPT_BODY",BODY,{"disambiguationData":[OSD([sQuery(id+"F2.wireOp",EDGE,"E361.MirrorC")])]});
            var Q179;
            Q179=makeQuery(id+"F4.opExtrude","SWEPT_BODY",BODY,{"disambiguationData":[OSD([sQuery(id+"F2.wireOp",EDGE,"E363.MirrorC")])]});
            var Q180;
            Q180=makeQuery(id+"F4.opExtrude","SWEPT_BODY",BODY,{"disambiguationData":[OSD([sQuery(id+"F2.wireOp",EDGE,"E364.MirrorC")])]});
            var Q181;
            Q181=makeQuery(id+"F4.opExtrude","SWEPT_BODY",BODY,{"disambiguationData":[OSD([sQuery(id+"F2.wireOp",EDGE,"E365.MirrorC")])]});
            var Q182;
            Q182=makeQuery(id+"F4.opExtrude","SWEPT_BODY",BODY,{"disambiguationData":[OSD([sQuery(id+"F2.wireOp",EDGE,"E366.MirrorC")])]});
            var Q183;
            Q183=makeQuery(id+"F4.opExtrude","SWEPT_BODY",BODY,{"disambiguationData":[OSD([sQuery(id+"F2.wireOp",EDGE,"E367.MirrorC")])]});
            var Q184;
            Q184=makeQuery(id+"F4.opExtrude","SWEPT_BODY",BODY,{"disambiguationData":[OSD([sQuery(id+"F2.wireOp",EDGE,"E369.MirrorC")])]});
            var Q185;
            Q185=makeQuery(id+"F4.opExtrude","SWEPT_BODY",BODY,{"disambiguationData":[OSD([sQuery(id+"F2.wireOp",EDGE,"E370.MirrorC")])]});
            var Q186;
            Q186=makeQuery(id+"F4.opExtrude","SWEPT_BODY",BODY,{"disambiguationData":[OSD([sQuery(id+"F2.wireOp",EDGE,"E371.MirrorC")])]});
            var Q187;
            Q187=makeQuery(id+"F4.opExtrude","SWEPT_BODY",BODY,{"disambiguationData":[OSD([sQuery(id+"F2.wireOp",EDGE,"E372.MirrorC")])]});
            var Q188;
            Q188=makeQuery(id+"F4.opExtrude","SWEPT_BODY",BODY,{"disambiguationData":[OSD([sQuery(id+"F2.wireOp",EDGE,"E374.MirrorC")])]});
            var Q189;
            Q189=makeQuery(id+"F4.opExtrude","SWEPT_BODY",BODY,{"disambiguationData":[OSD([sQuery(id+"F2.wireOp",EDGE,"E376.MirrorC")])]});
            var Q190;
            Q190=makeQuery(id+"F4.opExtrude","SWEPT_BODY",BODY,{"disambiguationData":[OSD([sQuery(id+"F2.wireOp",EDGE,"E377.MirrorC")])]});
            var Q191;
            Q191=makeQuery(id+"F4.opExtrude","SWEPT_BODY",BODY,{"disambiguationData":[OSD([sQuery(id+"F2.wireOp",EDGE,"E378.MirrorC")])]});
            var Q192;
            Q192=makeQuery(id+"F4.opExtrude","SWEPT_BODY",BODY,{"disambiguationData":[OSD([sQuery(id+"F2.wireOp",EDGE,"E379.MirrorC")])]});
            var Q193;
            Q193=makeQuery(id+"F4.opExtrude","SWEPT_BODY",BODY,{"disambiguationData":[OSD([sQuery(id+"F2.wireOp",EDGE,"E380.MirrorC")])]});
            var Q194;
            Q194=makeQuery(id+"F4.opExtrude","SWEPT_BODY",BODY,{"disambiguationData":[OSD([sQuery(id+"F2.wireOp",EDGE,"E382.MirrorC")])]});
            var Q195;
            Q195=makeQuery(id+"F4.opExtrude","SWEPT_BODY",BODY,{"disambiguationData":[OSD([sQuery(id+"F2.wireOp",EDGE,"E384.MirrorC")])]});
            var Q196;
            Q196=makeQuery(id+"F4.opExtrude","SWEPT_BODY",BODY,{"disambiguationData":[OSD([sQuery(id+"F2.wireOp",EDGE,"E385.MirrorC")])]});
            var Q197;
            Q197=makeQuery(id+"F4.opExtrude","SWEPT_BODY",BODY,{"disambiguationData":[OSD([sQuery(id+"F2.wireOp",EDGE,"E387.MirrorC")])]});
            var Q198;
            Q198=makeQuery(id+"F4.opExtrude","SWEPT_BODY",BODY,{"disambiguationData":[OSD([sQuery(id+"F2.wireOp",EDGE,"E388.MirrorC")])]});
            var Q199;
            Q199=makeQuery(id+"F4.opExtrude","SWEPT_BODY",BODY,{"disambiguationData":[OSD([sQuery(id+"F2.wireOp",EDGE,"E389.MirrorC")])]});
            var Q200;
            Q200=makeQuery(id+"F4.opExtrude","SWEPT_BODY",BODY,{"disambiguationData":[OSD([sQuery(id+"F2.wireOp",EDGE,"E390.MirrorC")])]});
            var Q201;
            Q201=makeQuery(id+"F4.opExtrude","SWEPT_BODY",BODY,{"disambiguationData":[OSD([sQuery(id+"F2.wireOp",EDGE,"E391.MirrorC")])]});
            var Q202;
            Q202=makeQuery(id+"F4.opExtrude","SWEPT_BODY",BODY,{"disambiguationData":[OSD([sQuery(id+"F2.wireOp",EDGE,"E393.MirrorC")])]});
            var Q203;
            Q203=makeQuery(id+"F4.opExtrude","SWEPT_BODY",BODY,{"disambiguationData":[OSD([sQuery(id+"F2.wireOp",EDGE,"E396.MirrorC")])]});
            var Q204;
            Q204=makeQuery(id+"F4.opExtrude","SWEPT_BODY",BODY,{"disambiguationData":[OSD([sQuery(id+"F2.wireOp",EDGE,"E399.MirrorC")])]});
            var Q205;
            Q205=makeQuery(id+"F4.opExtrude","SWEPT_BODY",BODY,{"disambiguationData":[OSD([sQuery(id+"F2.wireOp",EDGE,"E400.MirrorC")])]});
            var Q206;
            Q206=makeQuery(id+"F4.opExtrude","SWEPT_BODY",BODY,{"disambiguationData":[OSD([sQuery(id+"F2.wireOp",EDGE,"E401.MirrorC")])]});
            var Q207;
            Q207=makeQuery(id+"F4.opExtrude","SWEPT_BODY",BODY,{"disambiguationData":[OSD([sQuery(id+"F2.wireOp",EDGE,"E402.MirrorC")])]});
            var Q208;
            Q208=makeQuery(id+"F4.opExtrude","SWEPT_BODY",BODY,{"disambiguationData":[OSD([sQuery(id+"F2.wireOp",EDGE,"E403.MirrorC")])]});
            var Q209;
            Q209=makeQuery(id+"F4.opExtrude","SWEPT_BODY",BODY,{"disambiguationData":[OSD([sQuery(id+"F2.wireOp",EDGE,"E404.MirrorC")])]});
            var Q210;
            Q210=makeQuery(id+"F4.opExtrude","SWEPT_BODY",BODY,{"disambiguationData":[OSD([sQuery(id+"F2.wireOp",EDGE,"E406.MirrorC")])]});
            var Q211;
            Q211=makeQuery(id+"F4.opExtrude","SWEPT_BODY",BODY,{"disambiguationData":[OSD([sQuery(id+"F2.wireOp",EDGE,"E407.MirrorC")])]});
            var Q212;
            Q212=makeQuery(id+"F4.opExtrude","SWEPT_BODY",BODY,{"disambiguationData":[OSD([sQuery(id+"F2.wireOp",EDGE,"E408.MirrorC")])]});
            var Q213;
            Q213=makeQuery(id+"F4.opExtrude","SWEPT_BODY",BODY,{"disambiguationData":[OSD([sQuery(id+"F2.wireOp",EDGE,"E409.MirrorC")])]});
            var Q214;
            Q214=makeQuery(id+"F4.opExtrude","SWEPT_BODY",BODY,{"disambiguationData":[OSD([sQuery(id+"F2.wireOp",EDGE,"E115")])]});
            var Q215;
            Q215=makeQuery(id+"F4.opExtrude","SWEPT_BODY",BODY,{"disambiguationData":[OSD([sQuery(id+"F2.wireOp",EDGE,"E411.MirrorC")])]});
            var Q216;
            Q216=makeQuery(id+"F4.opExtrude","SWEPT_BODY",BODY,{"disambiguationData":[OSD([sQuery(id+"F2.wireOp",EDGE,"E412.MirrorC")])]});
            var Q217;
            Q217=makeQuery(id+"F4.opExtrude","SWEPT_BODY",BODY,{"disambiguationData":[OSD([sQuery(id+"F2.wireOp",EDGE,"E414.MirrorC")])]});
            var Q218;
            Q218=makeQuery(id+"F4.opExtrude","SWEPT_BODY",BODY,{"disambiguationData":[OSD([sQuery(id+"F2.wireOp",EDGE,"E415.MirrorC")])]});
            var Q219;
            Q219=makeQuery(id+"F4.opExtrude","SWEPT_BODY",BODY,{"disambiguationData":[OSD([sQuery(id+"F2.wireOp",EDGE,"E416.MirrorC")])]});
            var Q220;
            Q220=makeQuery(id+"F4.opExtrude","SWEPT_BODY",BODY,{"disambiguationData":[OSD([sQuery(id+"F2.wireOp",EDGE,"E418.MirrorC")])]});
            var Q221;
            Q221=makeQuery(id+"F4.opExtrude","SWEPT_BODY",BODY,{"disambiguationData":[OSD([sQuery(id+"F2.wireOp",EDGE,"E419.MirrorC")])]});
            var Q222;
            Q222=makeQuery(id+"F4.opExtrude","SWEPT_BODY",BODY,{"disambiguationData":[OSD([sQuery(id+"F2.wireOp",EDGE,"E420.MirrorC")])]});
            var Q223;
            Q223=makeQuery(id+"F4.opExtrude","SWEPT_BODY",BODY,{"disambiguationData":[OSD([sQuery(id+"F2.wireOp",EDGE,"E421.MirrorC")])]});
            var Q224;
            Q224=makeQuery(id+"F4.opExtrude","SWEPT_BODY",BODY,{"disambiguationData":[OSD([sQuery(id+"F2.wireOp",EDGE,"E422.MirrorC")])]});
            var Q225;
            Q225=makeQuery(id+"F4.opExtrude","SWEPT_BODY",BODY,{"disambiguationData":[OSD([sQuery(id+"F2.wireOp",EDGE,"E423.MirrorC")])]});
            var Q226;
            Q226=makeQuery(id+"F4.opExtrude","SWEPT_BODY",BODY,{"disambiguationData":[OSD([sQuery(id+"F2.wireOp",EDGE,"E424.MirrorC")])]});
            var Q227;
            Q227=makeQuery(id+"F4.opExtrude","SWEPT_BODY",BODY,{"disambiguationData":[OSD([sQuery(id+"F2.wireOp",EDGE,"E425.MirrorC")])]});
            var Q228;
            Q228=makeQuery(id+"F4.opExtrude","SWEPT_BODY",BODY,{"disambiguationData":[OSD([sQuery(id+"F2.wireOp",EDGE,"E427.MirrorC")])]});
            var Q229;
            Q229=makeQuery(id+"F4.opExtrude","SWEPT_BODY",BODY,{"disambiguationData":[OSD([sQuery(id+"F2.wireOp",EDGE,"E428.MirrorC")])]});
            var Q230;
            Q230=makeQuery(id+"F4.opExtrude","SWEPT_BODY",BODY,{"disambiguationData":[OSD([sQuery(id+"F2.wireOp",EDGE,"E429.MirrorC")])]});
            var Q231;
            Q231=makeQuery(id+"F4.opExtrude","SWEPT_BODY",BODY,{"disambiguationData":[OSD([sQuery(id+"F2.wireOp",EDGE,"E430.MirrorC")])]});
            var Q232;
            Q232=makeQuery(id+"F4.opExtrude","SWEPT_BODY",BODY,{"disambiguationData":[OSD([sQuery(id+"F2.wireOp",EDGE,"E431.MirrorC")])]});
            var Q233;
            Q233=makeQuery(id+"F4.opExtrude","SWEPT_BODY",BODY,{"disambiguationData":[OSD([sQuery(id+"F2.wireOp",EDGE,"E432.MirrorC")])]});
            var Q234;
            Q234=makeQuery(id+"F4.opExtrude","SWEPT_BODY",BODY,{"disambiguationData":[OSD([sQuery(id+"F2.wireOp",EDGE,"E433.MirrorC")])]});
            var Q235;
            Q235=makeQuery(id+"F4.opExtrude","SWEPT_BODY",BODY,{"disambiguationData":[OSD([sQuery(id+"F2.wireOp",EDGE,"E435.MirrorC")])]});
            var Q236;
            Q236=makeQuery(id+"F4.opExtrude","SWEPT_BODY",BODY,{"disambiguationData":[OSD([sQuery(id+"F2.wireOp",EDGE,"E436.MirrorC")])]});
            var Q237;
            Q237=makeQuery(id+"F4.opExtrude","SWEPT_BODY",BODY,{"disambiguationData":[OSD([sQuery(id+"F2.wireOp",EDGE,"E437.MirrorC")])]});
            var Q238;
            Q238=makeQuery(id+"F4.opExtrude","SWEPT_BODY",BODY,{"disambiguationData":[OSD([sQuery(id+"F2.wireOp",EDGE,"E438.MirrorC")])]});
            var Q239;
            Q239=makeQuery(id+"F4.opExtrude","SWEPT_BODY",BODY,{"disambiguationData":[OSD([sQuery(id+"F2.wireOp",EDGE,"E439.MirrorC")])]});
            var Q240;
            Q240=makeQuery(id+"F4.opExtrude","SWEPT_BODY",BODY,{"disambiguationData":[OSD([sQuery(id+"F2.wireOp",EDGE,"E440.MirrorC")])]});
            var Q241;
            Q241=makeQuery(id+"F4.opExtrude","SWEPT_BODY",BODY,{"disambiguationData":[OSD([sQuery(id+"F2.wireOp",EDGE,"E443.MirrorC")])]});
            var Q242;
            Q242=makeQuery(id+"F4.opExtrude","SWEPT_BODY",BODY,{"disambiguationData":[OSD([sQuery(id+"F2.wireOp",EDGE,"E444.MirrorC")])]});
            var Q243;
            Q243=makeQuery(id+"F4.opExtrude","SWEPT_BODY",BODY,{"disambiguationData":[OSD([sQuery(id+"F2.wireOp",EDGE,"E445.MirrorC")])]});
            var Q244;
            Q244=makeQuery(id+"F4.opExtrude","SWEPT_BODY",BODY,{"disambiguationData":[OSD([sQuery(id+"F2.wireOp",EDGE,"E447.MirrorC")])]});
            var Q245;
            Q245=makeQuery(id+"F4.opExtrude","SWEPT_BODY",BODY,{"disambiguationData":[OSD([sQuery(id+"F2.wireOp",EDGE,"E449.MirrorC")])]});
            var Q246;
            Q246=makeQuery(id+"F4.opExtrude","SWEPT_BODY",BODY,{"disambiguationData":[OSD([sQuery(id+"F2.wireOp",EDGE,"E452.MirrorC")])]});
            var Q247;
            Q247=makeQuery(id+"F4.opExtrude","SWEPT_BODY",BODY,{"disambiguationData":[OSD([sQuery(id+"F2.wireOp",EDGE,"E453.MirrorC")])]});
            var Q248;
            Q248=makeQuery(id+"F4.opExtrude","SWEPT_BODY",BODY,{"disambiguationData":[OSD([sQuery(id+"F2.wireOp",EDGE,"E455.MirrorC")])]});
            var Q249;
            Q249=makeQuery(id+"F4.opExtrude","SWEPT_BODY",BODY,{"disambiguationData":[OSD([sQuery(id+"F2.wireOp",EDGE,"E456.MirrorC")])]});
            var Q250;
            Q250=makeQuery(id+"F4.opExtrude","SWEPT_BODY",BODY,{"disambiguationData":[OSD([sQuery(id+"F2.wireOp",EDGE,"E460.MirrorC")])]});
            var Q251;
            Q251=makeQuery(id+"F4.opExtrude","SWEPT_BODY",BODY,{"disambiguationData":[OSD([sQuery(id+"F2.wireOp",EDGE,"E461.MirrorC")])]});
            var Q252;
            Q252=makeQuery(id+"F4.opExtrude","SWEPT_BODY",BODY,{"disambiguationData":[OSD([sQuery(id+"F2.wireOp",EDGE,"E463.MirrorC")])]});
            var Q253;
            Q253=makeQuery(id+"F4.opExtrude","SWEPT_BODY",BODY,{"disambiguationData":[OSD([sQuery(id+"F2.wireOp",EDGE,"E465.MirrorC")])]});
            var Q254;
            Q254=makeQuery(id+"F4.opExtrude","SWEPT_BODY",BODY,{"disambiguationData":[OSD([sQuery(id+"F2.wireOp",EDGE,"E466.MirrorC")])]});
            var Q255;
            Q255=makeQuery(id+"F4.opExtrude","SWEPT_BODY",BODY,{"disambiguationData":[OSD([sQuery(id+"F2.wireOp",EDGE,"E467.MirrorC")])]});
            var Q256;
            Q256=makeQuery(id+"F4.opExtrude","SWEPT_BODY",BODY,{"disambiguationData":[OSD([sQuery(id+"F2.wireOp",EDGE,"E468.MirrorC")])]});
            var Q257;
            Q257=makeQuery(id+"F4.opExtrude","SWEPT_BODY",BODY,{"disambiguationData":[OSD([sQuery(id+"F2.wireOp",EDGE,"E470.MirrorC")])]});
            var Q258;
            Q258=makeQuery(id+"F4.opExtrude","SWEPT_BODY",BODY,{"disambiguationData":[OSD([sQuery(id+"F2.wireOp",EDGE,"E471.MirrorC")])]});
            var Q259;
            Q259=makeQuery(id+"F4.opExtrude","SWEPT_BODY",BODY,{"disambiguationData":[OSD([sQuery(id+"F2.wireOp",EDGE,"E473.MirrorC")])]});
            var Q260;
            Q260=makeQuery(id+"F4.opExtrude","SWEPT_BODY",BODY,{"disambiguationData":[OSD([sQuery(id+"F2.wireOp",EDGE,"E475.MirrorC")])]});
            var Q261;
            Q261=makeQuery(id+"F4.opExtrude","SWEPT_BODY",BODY,{"disambiguationData":[OSD([sQuery(id+"F2.wireOp",EDGE,"E478.MirrorC")])]});
            var Q262;
            Q262=makeQuery(id+"F4.opExtrude","SWEPT_BODY",BODY,{"disambiguationData":[OSD([sQuery(id+"F2.wireOp",EDGE,"E480.MirrorC")])]});
            var Q263;
            Q263=makeQuery(id+"F4.opExtrude","SWEPT_BODY",BODY,{"disambiguationData":[OSD([sQuery(id+"F2.wireOp",EDGE,"E481.MirrorC")])]});
            var Q264;
            Q264=makeQuery(id+"F4.opExtrude","SWEPT_BODY",BODY,{"disambiguationData":[OSD([sQuery(id+"F2.wireOp",EDGE,"E483.MirrorC")])]});
            var Q265;
            Q265=makeQuery(id+"F4.opExtrude","SWEPT_BODY",BODY,{"disambiguationData":[OSD([sQuery(id+"F2.wireOp",EDGE,"E486.MirrorC")])]});
            var Q266;
            Q266=makeQuery(id+"F4.opExtrude","SWEPT_BODY",BODY,{"disambiguationData":[OSD([sQuery(id+"F2.wireOp",EDGE,"E489.MirrorC")])]});
            var Q267;
            Q267=makeQuery(id+"F4.opExtrude","SWEPT_BODY",BODY,{"disambiguationData":[OSD([sQuery(id+"F2.wireOp",EDGE,"E491.MirrorC")])]});
            var Q268;
            Q268=makeQuery(id+"F4.opExtrude","SWEPT_BODY",BODY,{"disambiguationData":[OSD([sQuery(id+"F2.wireOp",EDGE,"E492.MirrorC")])]});
            var Q269;
            Q269=makeQuery(id+"F4.opExtrude","SWEPT_BODY",BODY,{"disambiguationData":[OSD([sQuery(id+"F2.wireOp",EDGE,"E496.MirrorC")])]});
            var Q270;
            Q270=makeQuery(id+"F4.opExtrude","SWEPT_BODY",BODY,{"disambiguationData":[OSD([sQuery(id+"F2.wireOp",EDGE,"E497.MirrorC")])]});
            var Q271;
            Q271=makeQuery(id+"F4.opExtrude","SWEPT_BODY",BODY,{"disambiguationData":[OSD([sQuery(id+"F2.wireOp",EDGE,"E499.MirrorC")])]});
            var Q272;
            Q272=makeQuery(id+"F4.opExtrude","SWEPT_BODY",BODY,{"disambiguationData":[OSD([sQuery(id+"F2.wireOp",EDGE,"E502.MirrorC")])]});
            var Q273;
            Q273=makeQuery(id+"F4.opExtrude","SWEPT_BODY",BODY,{"disambiguationData":[OSD([sQuery(id+"F2.wireOp",EDGE,"E504.MirrorC")])]});
            var Q274;
            Q274=makeQuery(id+"F4.opExtrude","SWEPT_BODY",BODY,{"disambiguationData":[OSD([sQuery(id+"F2.wireOp",EDGE,"E506.MirrorC")])]});
            var Q275;
            Q275=makeQuery(id+"F4.opExtrude","SWEPT_BODY",BODY,{"disambiguationData":[OSD([sQuery(id+"F2.wireOp",EDGE,"E507.MirrorC")])]});
            var Q276;
            Q276=makeQuery(id+"F4.opExtrude","SWEPT_BODY",BODY,{"disambiguationData":[OSD([sQuery(id+"F2.wireOp",EDGE,"E510.MirrorC")])]});
            var Q277;
            Q277=makeQuery(id+"F4.opExtrude","SWEPT_BODY",BODY,{"disambiguationData":[OSD([sQuery(id+"F2.wireOp",EDGE,"E511.MirrorC")])]});
            var Q278;
            Q278=makeQuery(id+"F4.opExtrude","SWEPT_BODY",BODY,{"disambiguationData":[OSD([sQuery(id+"F2.wireOp",EDGE,"E513.MirrorC")])]});
            var Q279;
            Q279=makeQuery(id+"F4.opExtrude","SWEPT_BODY",BODY,{"disambiguationData":[OSD([sQuery(id+"F2.wireOp",EDGE,"E514.MirrorC")])]});
            var Q280;
            Q280=makeQuery(id+"F4.opExtrude","SWEPT_BODY",BODY,{"disambiguationData":[OSD([sQuery(id+"F2.wireOp",EDGE,"E516.MirrorC")])]});
            var Q281;
            Q281=makeQuery(id+"F4.opExtrude","SWEPT_BODY",BODY,{"disambiguationData":[OSD([sQuery(id+"F2.wireOp",EDGE,"E521.MirrorC")])]});
            var Q282;
            Q282=makeQuery(id+"F4.opExtrude","SWEPT_BODY",BODY,{"disambiguationData":[OSD([sQuery(id+"F2.wireOp",EDGE,"E522.MirrorC")])]});
            var Q283;
            Q283=makeQuery(id+"F4.opExtrude","SWEPT_BODY",BODY,{"disambiguationData":[OSD([sQuery(id+"F2.wireOp",EDGE,"E524.MirrorC")])]});
            var Q284;
            Q284=makeQuery(id+"F4.opExtrude","SWEPT_BODY",BODY,{"disambiguationData":[OSD([sQuery(id+"F2.wireOp",EDGE,"E527.MirrorC")])]});
            var Q285;
            Q285=makeQuery(id+"F4.opExtrude","SWEPT_BODY",BODY,{"disambiguationData":[OSD([sQuery(id+"F2.wireOp",EDGE,"E528.MirrorC")])]});
            var Q286;
            Q286=makeQuery(id+"F4.opExtrude","SWEPT_BODY",BODY,{"disambiguationData":[OSD([sQuery(id+"F2.wireOp",EDGE,"E529.MirrorC")])]});
            var Q287;
            Q287=makeQuery(id+"F4.opExtrude","SWEPT_BODY",BODY,{"disambiguationData":[OSD([sQuery(id+"F2.wireOp",EDGE,"E530.MirrorC")])]});
            var Q288;
            Q288=makeQuery(id+"F4.opExtrude","SWEPT_BODY",BODY,{"disambiguationData":[OSD([sQuery(id+"F2.wireOp",EDGE,"E533.MirrorC")])]});
            var Q289;
            Q289=makeQuery(id+"F4.opExtrude","SWEPT_BODY",BODY,{"disambiguationData":[OSD([sQuery(id+"F2.wireOp",EDGE,"E536.MirrorC")])]});
            var Q290;
            Q290=makeQuery(id+"F4.opExtrude","SWEPT_BODY",BODY,{"disambiguationData":[OSD([sQuery(id+"F2.wireOp",EDGE,"E538.MirrorC")])]});
            var Q291;
            Q291=makeQuery(id+"F4.opExtrude","SWEPT_BODY",BODY,{"disambiguationData":[OSD([sQuery(id+"F2.wireOp",EDGE,"E114")])]});
            var Q292;
            Q292=makeQuery(id+"F4.opExtrude","SWEPT_BODY",BODY,{"disambiguationData":[OSD([sQuery(id+"F2.wireOp",EDGE,"E539.MirrorC")])]});
            var Q293;
            Q293=makeQuery(id+"F4.opExtrude","SWEPT_BODY",BODY,{"disambiguationData":[OSD([sQuery(id+"F2.wireOp",EDGE,"E543.MirrorC")])]});
            var Q294;
            Q294=makeQuery(id+"F4.opExtrude","SWEPT_BODY",BODY,{"disambiguationData":[OSD([sQuery(id+"F2.wireOp",EDGE,"E547.MirrorC")])]});
            var Q295;
            Q295=makeQuery(id+"F4.opExtrude","SWEPT_BODY",BODY,{"disambiguationData":[OSD([sQuery(id+"F2.wireOp",EDGE,"E550.MirrorC")])]});
            var Q296;
            Q296=makeQuery(id+"F4.opExtrude","SWEPT_BODY",BODY,{"disambiguationData":[OSD([sQuery(id+"F2.wireOp",EDGE,"E551.MirrorC")])]});
            var Q297;
            Q297=makeQuery(id+"F4.opExtrude","SWEPT_BODY",BODY,{"disambiguationData":[OSD([sQuery(id+"F2.wireOp",EDGE,"E553.MirrorC")])]});
            var Q298;
            Q298=makeQuery(id+"F4.opExtrude","SWEPT_BODY",BODY,{"disambiguationData":[OSD([sQuery(id+"F2.wireOp",EDGE,"E554.MirrorC")])]});
            var Q299;
            Q299=makeQuery(id+"F4.opExtrude","SWEPT_BODY",BODY,{"disambiguationData":[OSD([sQuery(id+"F2.wireOp",EDGE,"E555.MirrorC")])]});
            var Q300;
            Q300=makeQuery(id+"F5.opSweep","SWEPT_BODY",BODY,{"disambiguationData":[OSD([sQuery(id+"F0.wireOp",EDGE,"E0"),sQuery(id+"F3.wireOp",EDGE,"E617.0.1"),sQuery(id+"F3.wireOp",EDGE,"E617.0.2"),sQuery(id+"F3.wireOp",EDGE,"E617.0.3"),sQuery(id+"F3.wireOp",EDGE,"E617.0.4"),sQuery(id+"F3.wireOp",EDGE,"E618.0"),sQuery(id+"F3.wireOp",EDGE,"E618.1"),sQuery(id+"F3.wireOp",EDGE,"E619")])]});
            booleanBodies(context, id + "F6", {"operationType" : BooleanOperationType.UNION, "tools" : qUnion([Q0, Q1, Q2, Q3, Q4, Q5, Q6, Q7, Q8, Q9, Q10, Q11, Q12, Q13, Q14, Q15, Q16, Q17, Q18, Q19, Q20, Q21, Q22, Q23, Q24, Q25, Q26, Q27, Q28, Q29, Q30, Q31, Q32, Q33, Q34, Q35, Q36, Q37, Q38, Q39, Q40, Q41, Q42, Q43, Q44, Q45, Q46, Q47, Q48, Q49, Q50, Q51, Q52, Q53, Q54, Q55, Q56, Q57, Q58, Q59, Q60, Q61, Q62, Q63, Q64, Q65, Q66, Q67, Q68, Q69, Q70, Q71, Q72, Q73, Q74, Q75, Q76, Q77, Q78, Q79, Q80, Q81, Q82, Q83, Q84, Q85, Q86, Q87, Q88, Q89, Q90, Q91, Q92, Q93, Q94, Q95, Q96, Q97, Q98, Q99, Q100, Q101, Q102, Q103, Q104, Q105, Q106, Q107, Q108, Q109, Q110, Q111, Q112, Q113, Q114, Q115, Q116, Q117, Q118, Q119, Q120, Q121, Q122, Q123, Q124, Q125, Q126, Q127, Q128, Q129, Q130, Q131, Q132, Q133, Q134, Q135, Q136, Q137, Q138, Q139, Q140, Q141, Q142, Q143, Q144, Q145, Q146, Q147, Q148, Q149, Q150, Q151, Q152, Q153, Q154, Q155, Q156, Q157, Q158, Q159, Q160, Q161, Q162, Q163, Q164, Q165, Q166, Q167, Q168, Q169, Q170, Q171, Q172, Q173, Q174, Q175, Q176, Q177, Q178, Q179, Q180, Q181, Q182, Q183, Q184, Q185, Q186, Q187, Q188, Q189, Q190, Q191, Q192, Q193, Q194, Q195, Q196, Q197, Q198, Q199, Q200, Q201, Q202, Q203, Q204, Q205, Q206, Q207, Q208, Q209, Q210, Q211, Q212, Q213, Q214, Q215, Q216, Q217, Q218, Q219, Q220, Q221, Q222, Q223, Q224, Q225, Q226, Q227, Q228, Q229, Q230, Q231, Q232, Q233, Q234, Q235, Q236, Q237, Q238, Q239, Q240, Q241, Q242, Q243, Q244, Q245, Q246, Q247, Q248, Q249, Q250, Q251, Q252, Q253, Q254, Q255, Q256, Q257, Q258, Q259, Q260, Q261, Q262, Q263, Q264, Q265, Q266, Q267, Q268, Q269, Q270, Q271, Q272, Q273, Q274, Q275, Q276, Q277, Q278, Q279, Q280, Q281, Q282, Q283, Q284, Q285, Q286, Q287, Q288, Q289, Q290, Q291, Q292, Q293, Q294, Q295, Q296, Q297, Q298, Q299, Q300])});
        }
        {
            var Q0;
            Q0=qCreatedBy(makeId("Front.planeOp"),FACE);
            var sketch = newSketch(context, id + "F7", { "sketchPlane" : qUnion([Q0])});
            skLineSegment(sketch, "E620.0", {"start": v(18.75, -0.25) * mm, "end": v(18.75, -1) * mm});
            skArc(sketch, "E620.3", {"start": v(26.75, -4) * mm, "mid": v(27.16, -3.78) * mm, "end": v(27.21, -3.31) * mm});
            skLineSegment(sketch, "E620.4", {"start": v(22.74, -0.42) * mm, "end": v(18.74, -0.25) * mm});
            skArc(sketch, "E620.5", {"start": v(26.98, -3.4) * mm, "mid": v(25.3, -1.29) * mm, "end": v(22.74, -0.42) * mm});
            skLineSegment(sketch, "E620.6", {"start": v(26.98, -3.4) * mm, "end": v(27.21, -3.31) * mm});
            skPoint(sketch, "E620.7", {"position": v(18.75, 0) * mm});
            skPoint(sketch, "E620.8", {"position": v(22.75, -0.17) * mm});
            skLineSegment(sketch, "E621", {"start": v(18.75, -1) * mm, "end": v(18.75, -4) * mm});
            skLineSegment(sketch, "E622", {"start": v(26.75, -4) * mm, "end": v(18.75, -4) * mm});
            skPoint(sketch, "E620.2.end.orphan", {"position": v(26.29, -3.69) * mm});
            skPoint(sketch, "E620.2.start.orphan", {"position": v(22.75, -1.18) * mm});
            skPoint(sketch, "E620.1.end.orphan", {"position": v(22.75, -1.18) * mm});
            skPoint(sketch, "E620.1.start.orphan", {"position": v(18.75, -1) * mm});
            skSolve(sketch);
        }
        {
            var Q0;
            Q0 = qSketchRegion(id + "F7", true);
            var Q1;
            Q1=sQuery(id+"F0.wireOp",EDGE,"E0");
            sweep(context, id + "F8", {"operationType" : NewBodyOperationType.REMOVE, "profiles" : qUnion([Q0]), "path" : qUnion([Q1])});
        }
        {
            var Q0;
            Q0=qCreatedBy(makeId("Front.planeOp"),FACE);
            var sketch = newSketch(context, id + "F9", { "sketchPlane" : qUnion([Q0])});
            skLineSegment(sketch, "E623.bottom", {"start": v(18.76, 0) * mm, "end": v(27.26, 0) * mm});
            skLineSegment(sketch, "E623.top", {"start": v(18.76, 2.85) * mm, "end": v(27.26, 2.85) * mm});
            skLineSegment(sketch, "E623.left", {"start": v(18.76, 0) * mm, "end": v(18.76, 2.85) * mm});
            skLineSegment(sketch, "E623.right", {"start": v(27.26, 0) * mm, "end": v(27.26, 2.85) * mm});
            skSolve(sketch);
        }
        {
            var Q0;
            Q0=makeQuery(id+"F9.imprint","IMPRINT",FACE,{"disambiguationData":[TD([[makeQuery(id+"F9.imprint","IMPRINT",EDGE,{"derivedFrom":sQuery(id+"F9.wireOp",EDGE,"E623.bottom")}),1.0]])]});
            var Q1;
            Q1=sQuery(id+"F0.wireOp",EDGE,"E0");
            sweep(context, id + "F10", {"operationType" : NewBodyOperationType.ADD, "profiles" : qUnion([Q0]), "path" : qUnion([Q1])});
        }
        {
            var Q0;
            Q0=makeQuery(id+"F8.boolean.opBoolean","COPY",FACE,{"disambiguationData":[TD([makeQuery(id+"F4.opExtrude","SWEPT_FACE",FACE,{"disambiguationData":[OSD([sQuery(id+"F2.wireOp",EDGE,"E181.MirrorC")])]})])],"derivedFrom":makeQuery(id+"F8.opSweep","SWEPT_FACE",FACE,{"disambiguationData":[OSD([sQuery(id+"F0.wireOp",EDGE,"E0"),sQuery(id+"F7.wireOp",EDGE,"E620.4")])]})});
            var Q1;
            Q1=makeQuery(id+"F8.boolean.opBoolean","COPY",FACE,{"disambiguationData":[TD([makeQuery(id+"F4.opExtrude","SWEPT_FACE",FACE,{"disambiguationData":[OSD([sQuery(id+"F2.wireOp",EDGE,"E240.MirrorC")])]})])],"derivedFrom":makeQuery(id+"F8.opSweep","SWEPT_FACE",FACE,{"disambiguationData":[OSD([sQuery(id+"F0.wireOp",EDGE,"E0"),sQuery(id+"F7.wireOp",EDGE,"E620.4")])]})});
            var Q2;
            Q2=makeQuery(id+"F8.boolean.opBoolean","COPY",FACE,{"disambiguationData":[TD([makeQuery(id+"F4.opExtrude","SWEPT_FACE",FACE,{"disambiguationData":[OSD([sQuery(id+"F2.wireOp",EDGE,"E320.MirrorC")])]})])],"derivedFrom":makeQuery(id+"F8.opSweep","SWEPT_FACE",FACE,{"disambiguationData":[OSD([sQuery(id+"F0.wireOp",EDGE,"E0"),sQuery(id+"F7.wireOp",EDGE,"E620.4")])]})});
            var Q3;
            Q3=makeQuery(id+"F8.boolean.opBoolean","COPY",FACE,{"disambiguationData":[TD([makeQuery(id+"F4.opExtrude","SWEPT_FACE",FACE,{"disambiguationData":[OSD([sQuery(id+"F2.wireOp",EDGE,"E308.MirrorC")])]})])],"derivedFrom":makeQuery(id+"F8.opSweep","SWEPT_FACE",FACE,{"disambiguationData":[OSD([sQuery(id+"F0.wireOp",EDGE,"E0"),sQuery(id+"F7.wireOp",EDGE,"E620.5")])]})});
            var Q4;
            Q4=makeQuery(id+"F8.boolean.opBoolean","COPY",FACE,{"disambiguationData":[TD([makeQuery(id+"F4.opExtrude","SWEPT_FACE",FACE,{"disambiguationData":[OSD([sQuery(id+"F2.wireOp",EDGE,"E202.MirrorC")])]})])],"derivedFrom":makeQuery(id+"F8.opSweep","SWEPT_FACE",FACE,{"disambiguationData":[OSD([sQuery(id+"F0.wireOp",EDGE,"E0"),sQuery(id+"F7.wireOp",EDGE,"E620.5")])]})});
            var Q5;
            Q5=makeQuery(id+"F8.boolean.opBoolean","COPY",FACE,{"disambiguationData":[TD([makeQuery(id+"F4.opExtrude","SWEPT_FACE",FACE,{"disambiguationData":[OSD([sQuery(id+"F2.wireOp",EDGE,"E227.MirrorC")])]})])],"derivedFrom":makeQuery(id+"F8.opSweep","SWEPT_FACE",FACE,{"disambiguationData":[OSD([sQuery(id+"F0.wireOp",EDGE,"E0"),sQuery(id+"F7.wireOp",EDGE,"E620.5")])]})});
            var Q6;
            Q6=makeQuery(id+"F8.boolean.opBoolean","COPY",FACE,{"disambiguationData":[TD([makeQuery(id+"F4.opExtrude","SWEPT_FACE",FACE,{"disambiguationData":[OSD([sQuery(id+"F2.wireOp",EDGE,"E305.MirrorC")])]})])],"derivedFrom":makeQuery(id+"F8.opSweep","SWEPT_FACE",FACE,{"disambiguationData":[OSD([sQuery(id+"F0.wireOp",EDGE,"E0"),sQuery(id+"F7.wireOp",EDGE,"E620.5")])]})});
            var Q7;
            Q7=makeQuery(id+"F8.boolean.opBoolean","COPY",FACE,{"disambiguationData":[TD([makeQuery(id+"F4.opExtrude","SWEPT_FACE",FACE,{"disambiguationData":[OSD([sQuery(id+"F2.wireOp",EDGE,"E443.MirrorC")])]})])],"derivedFrom":makeQuery(id+"F8.opSweep","SWEPT_FACE",FACE,{"disambiguationData":[OSD([sQuery(id+"F0.wireOp",EDGE,"E0"),sQuery(id+"F7.wireOp",EDGE,"E620.5")])]})});
            var Q8;
            Q8=makeQuery(id+"F6.opBoolean","INTERSECT",EDGE,{"derivedFrom":[makeQuery(id+"F4.opExtrude","SWEPT_FACE",FACE,{"disambiguationData":[OSD([sQuery(id+"F2.wireOp",EDGE,"E277.MirrorC")])]}),makeQuery(id+"F5.opSweep","SWEPT_FACE",FACE,{"disambiguationData":[OSD([sQuery(id+"F0.wireOp",EDGE,"E0"),sQuery(id+"F3.wireOp",EDGE,"E618.1")])]})]});
            var Q9;
            Q9=makeQuery(id+"F6.opBoolean","INTERSECT",EDGE,{"derivedFrom":[makeQuery(id+"F4.opExtrude","SWEPT_FACE",FACE,{"disambiguationData":[OSD([sQuery(id+"F2.wireOp",EDGE,"E277.MirrorC")])]}),makeQuery(id+"F5.opSweep","SWEPT_FACE",FACE,{"disambiguationData":[OSD([sQuery(id+"F0.wireOp",EDGE,"E0"),sQuery(id+"F3.wireOp",EDGE,"E618.0")])]})]});
            var Q10;
            Q10=makeQuery(id+"F6.opBoolean","INTERSECT",EDGE,{"derivedFrom":[makeQuery(id+"F4.opExtrude","SWEPT_FACE",FACE,{"disambiguationData":[OSD([sQuery(id+"F2.wireOp",EDGE,"E192.MirrorC")])]}),makeQuery(id+"F5.opSweep","SWEPT_FACE",FACE,{"disambiguationData":[OSD([sQuery(id+"F0.wireOp",EDGE,"E0"),sQuery(id+"F3.wireOp",EDGE,"E618.0")])]})]});
            var Q11;
            Q11=makeQuery(id+"F6.opBoolean","INTERSECT",EDGE,{"derivedFrom":[makeQuery(id+"F4.opExtrude","SWEPT_FACE",FACE,{"disambiguationData":[OSD([sQuery(id+"F2.wireOp",EDGE,"E192.MirrorC")])]}),makeQuery(id+"F5.opSweep","SWEPT_FACE",FACE,{"disambiguationData":[OSD([sQuery(id+"F0.wireOp",EDGE,"E0"),sQuery(id+"F3.wireOp",EDGE,"E618.1")])]})]});
            var Q12;
            Q12=makeQuery(id+"F6.opBoolean","INTERSECT",EDGE,{"derivedFrom":[makeQuery(id+"F4.opExtrude","SWEPT_FACE",FACE,{"disambiguationData":[OSD([sQuery(id+"F2.wireOp",EDGE,"E299.MirrorC")])]}),makeQuery(id+"F5.opSweep","SWEPT_FACE",FACE,{"disambiguationData":[OSD([sQuery(id+"F0.wireOp",EDGE,"E0"),sQuery(id+"F3.wireOp",EDGE,"E618.0")])]})]});
            var Q13;
            Q13=makeQuery(id+"F6.opBoolean","INTERSECT",EDGE,{"derivedFrom":[makeQuery(id+"F4.opExtrude","SWEPT_FACE",FACE,{"disambiguationData":[OSD([sQuery(id+"F2.wireOp",EDGE,"E221.MirrorC")])]}),makeQuery(id+"F5.opSweep","SWEPT_FACE",FACE,{"disambiguationData":[OSD([sQuery(id+"F0.wireOp",EDGE,"E0"),sQuery(id+"F3.wireOp",EDGE,"E618.0")])]})]});
            var Q14;
            Q14=makeQuery(id+"F6.opBoolean","INTERSECT",EDGE,{"derivedFrom":[makeQuery(id+"F4.opExtrude","SWEPT_FACE",FACE,{"disambiguationData":[OSD([sQuery(id+"F2.wireOp",EDGE,"E247.MirrorC")])]}),makeQuery(id+"F5.opSweep","SWEPT_FACE",FACE,{"disambiguationData":[OSD([sQuery(id+"F0.wireOp",EDGE,"E0"),sQuery(id+"F3.wireOp",EDGE,"E618.0")])]})]});
            var Q15;
            Q15=makeQuery(id+"F6.opBoolean","INTERSECT",EDGE,{"derivedFrom":[makeQuery(id+"F4.opExtrude","SWEPT_FACE",FACE,{"disambiguationData":[OSD([sQuery(id+"F2.wireOp",EDGE,"E247.MirrorC")])]}),makeQuery(id+"F5.opSweep","SWEPT_FACE",FACE,{"disambiguationData":[OSD([sQuery(id+"F0.wireOp",EDGE,"E0"),sQuery(id+"F3.wireOp",EDGE,"E618.1")])]})]});
            var Q16;
            Q16=makeQuery(id+"F8.boolean.opBoolean","COPY",FACE,{"disambiguationData":[TD([makeQuery(id+"F4.opExtrude","SWEPT_FACE",FACE,{"disambiguationData":[OSD([sQuery(id+"F2.wireOp",EDGE,"E319.MirrorC")])]})])],"derivedFrom":makeQuery(id+"F8.opSweep","SWEPT_FACE",FACE,{"disambiguationData":[OSD([sQuery(id+"F0.wireOp",EDGE,"E0"),sQuery(id+"F7.wireOp",EDGE,"E620.5")])]})});
            var Q17;
            Q17=makeQuery(id+"F8.boolean.opBoolean","COPY",FACE,{"disambiguationData":[TD([makeQuery(id+"F4.opExtrude","SWEPT_FACE",FACE,{"disambiguationData":[OSD([sQuery(id+"F2.wireOp",EDGE,"E466.MirrorC")])]})])],"derivedFrom":makeQuery(id+"F8.opSweep","SWEPT_FACE",FACE,{"disambiguationData":[OSD([sQuery(id+"F0.wireOp",EDGE,"E0"),sQuery(id+"F7.wireOp",EDGE,"E620.5")])]})});
            var Q18;
            Q18=makeQuery(id+"F8.boolean.opBoolean","COPY",FACE,{"disambiguationData":[TD([makeQuery(id+"F4.opExtrude","SWEPT_FACE",FACE,{"disambiguationData":[OSD([sQuery(id+"F2.wireOp",EDGE,"E475.MirrorC")])]})])],"derivedFrom":makeQuery(id+"F8.opSweep","SWEPT_FACE",FACE,{"disambiguationData":[OSD([sQuery(id+"F0.wireOp",EDGE,"E0"),sQuery(id+"F7.wireOp",EDGE,"E620.5")])]})});
            var Q19;
            Q19=makeQuery(id+"F8.boolean.opBoolean","COPY",FACE,{"disambiguationData":[TD([makeQuery(id+"F4.opExtrude","SWEPT_FACE",FACE,{"disambiguationData":[OSD([sQuery(id+"F2.wireOp",EDGE,"E486.MirrorC")])]})])],"derivedFrom":makeQuery(id+"F8.opSweep","SWEPT_FACE",FACE,{"disambiguationData":[OSD([sQuery(id+"F0.wireOp",EDGE,"E0"),sQuery(id+"F7.wireOp",EDGE,"E620.5")])]})});
            var Q20;
            Q20=makeQuery(id+"F8.boolean.opBoolean","COPY",FACE,{"disambiguationData":[TD([makeQuery(id+"F4.opExtrude","SWEPT_FACE",FACE,{"disambiguationData":[OSD([sQuery(id+"F2.wireOp",EDGE,"E524.MirrorC")])]})])],"derivedFrom":makeQuery(id+"F8.opSweep","SWEPT_FACE",FACE,{"disambiguationData":[OSD([sQuery(id+"F0.wireOp",EDGE,"E0"),sQuery(id+"F7.wireOp",EDGE,"E620.5")])]})});
            var Q21;
            Q21=makeQuery(id+"F8.boolean.opBoolean","COPY",FACE,{"disambiguationData":[TD([makeQuery(id+"F4.opExtrude","SWEPT_FACE",FACE,{"disambiguationData":[OSD([sQuery(id+"F2.wireOp",EDGE,"E522.MirrorC")])]})])],"derivedFrom":makeQuery(id+"F8.opSweep","SWEPT_FACE",FACE,{"disambiguationData":[OSD([sQuery(id+"F0.wireOp",EDGE,"E0"),sQuery(id+"F7.wireOp",EDGE,"E620.5")])]})});
            var Q22;
            Q22=makeQuery(id+"F8.boolean.opBoolean","COPY",FACE,{"disambiguationData":[TD([makeQuery(id+"F4.opExtrude","SWEPT_FACE",FACE,{"disambiguationData":[OSD([sQuery(id+"F2.wireOp",EDGE,"E499.MirrorC")])]})])],"derivedFrom":makeQuery(id+"F8.opSweep","SWEPT_FACE",FACE,{"disambiguationData":[OSD([sQuery(id+"F0.wireOp",EDGE,"E0"),sQuery(id+"F7.wireOp",EDGE,"E620.5")])]})});
            var Q23;
            Q23=makeQuery(id+"F6.opBoolean","INTERSECT",EDGE,{"derivedFrom":[makeQuery(id+"F4.opExtrude","SWEPT_FACE",FACE,{"disambiguationData":[OSD([sQuery(id+"F2.wireOp",EDGE,"E418.MirrorC")])]}),makeQuery(id+"F5.opSweep","SWEPT_FACE",FACE,{"disambiguationData":[OSD([sQuery(id+"F0.wireOp",EDGE,"E0"),sQuery(id+"F3.wireOp",EDGE,"E618.1")])]})]});
            var Q24;
            Q24=makeQuery(id+"F6.opBoolean","INTERSECT",EDGE,{"derivedFrom":[makeQuery(id+"F4.opExtrude","SWEPT_FACE",FACE,{"disambiguationData":[OSD([sQuery(id+"F2.wireOp",EDGE,"E418.MirrorC")])]}),makeQuery(id+"F5.opSweep","SWEPT_FACE",FACE,{"disambiguationData":[OSD([sQuery(id+"F0.wireOp",EDGE,"E0"),sQuery(id+"F3.wireOp",EDGE,"E618.0")])]})]});
            var Q25;
            Q25=makeQuery(id+"F6.opBoolean","INTERSECT",EDGE,{"derivedFrom":[makeQuery(id+"F4.opExtrude","SWEPT_FACE",FACE,{"disambiguationData":[OSD([sQuery(id+"F2.wireOp",EDGE,"E367.MirrorC")])]}),makeQuery(id+"F5.opSweep","SWEPT_FACE",FACE,{"disambiguationData":[OSD([sQuery(id+"F0.wireOp",EDGE,"E0"),sQuery(id+"F3.wireOp",EDGE,"E618.0")])]})]});
            var Q26;
            Q26=makeQuery(id+"F6.opBoolean","INTERSECT",EDGE,{"derivedFrom":[makeQuery(id+"F4.opExtrude","SWEPT_FACE",FACE,{"disambiguationData":[OSD([sQuery(id+"F2.wireOp",EDGE,"E367.MirrorC")])]}),makeQuery(id+"F5.opSweep","SWEPT_FACE",FACE,{"disambiguationData":[OSD([sQuery(id+"F0.wireOp",EDGE,"E0"),sQuery(id+"F3.wireOp",EDGE,"E618.1")])]})]});
            var Q27;
            Q27=makeQuery(id+"F6.opBoolean","INTERSECT",EDGE,{"derivedFrom":[makeQuery(id+"F4.opExtrude","SWEPT_FACE",FACE,{"disambiguationData":[OSD([sQuery(id+"F2.wireOp",EDGE,"E404.MirrorC")])]}),makeQuery(id+"F5.opSweep","SWEPT_FACE",FACE,{"disambiguationData":[OSD([sQuery(id+"F0.wireOp",EDGE,"E0"),sQuery(id+"F3.wireOp",EDGE,"E618.1")])]})]});
            var Q28;
            Q28=makeQuery(id+"F6.opBoolean","INTERSECT",EDGE,{"derivedFrom":[makeQuery(id+"F4.opExtrude","SWEPT_FACE",FACE,{"disambiguationData":[OSD([sQuery(id+"F2.wireOp",EDGE,"E404.MirrorC")])]}),makeQuery(id+"F5.opSweep","SWEPT_FACE",FACE,{"disambiguationData":[OSD([sQuery(id+"F0.wireOp",EDGE,"E0"),sQuery(id+"F3.wireOp",EDGE,"E618.0")])]})]});
            var Q29;
            Q29=makeQuery(id+"F6.opBoolean","INTERSECT",EDGE,{"derivedFrom":[makeQuery(id+"F4.opExtrude","SWEPT_FACE",FACE,{"disambiguationData":[OSD([sQuery(id+"F2.wireOp",EDGE,"E411.MirrorC")])]}),makeQuery(id+"F5.opSweep","SWEPT_FACE",FACE,{"disambiguationData":[OSD([sQuery(id+"F0.wireOp",EDGE,"E0"),sQuery(id+"F3.wireOp",EDGE,"E618.0")])]})]});
            var Q30;
            Q30=makeQuery(id+"F6.opBoolean","INTERSECT",EDGE,{"derivedFrom":[makeQuery(id+"F4.opExtrude","SWEPT_FACE",FACE,{"disambiguationData":[OSD([sQuery(id+"F2.wireOp",EDGE,"E411.MirrorC")])]}),makeQuery(id+"F5.opSweep","SWEPT_FACE",FACE,{"disambiguationData":[OSD([sQuery(id+"F0.wireOp",EDGE,"E0"),sQuery(id+"F3.wireOp",EDGE,"E618.1")])]})]});
            var Q31;
            Q31=makeQuery(id+"F6.opBoolean","INTERSECT",EDGE,{"derivedFrom":[makeQuery(id+"F4.opExtrude","SWEPT_FACE",FACE,{"disambiguationData":[OSD([sQuery(id+"F2.wireOp",EDGE,"E425.MirrorC")])]}),makeQuery(id+"F5.opSweep","SWEPT_FACE",FACE,{"disambiguationData":[OSD([sQuery(id+"F0.wireOp",EDGE,"E0"),sQuery(id+"F3.wireOp",EDGE,"E618.1")])]})]});
            var Q32;
            Q32=makeQuery(id+"F6.opBoolean","INTERSECT",EDGE,{"derivedFrom":[makeQuery(id+"F4.opExtrude","SWEPT_FACE",FACE,{"disambiguationData":[OSD([sQuery(id+"F2.wireOp",EDGE,"E425.MirrorC")])]}),makeQuery(id+"F5.opSweep","SWEPT_FACE",FACE,{"disambiguationData":[OSD([sQuery(id+"F0.wireOp",EDGE,"E0"),sQuery(id+"F3.wireOp",EDGE,"E618.0")])]})]});
            var Q33;
            Q33=makeQuery(id+"F6.opBoolean","INTERSECT",EDGE,{"derivedFrom":[makeQuery(id+"F4.opExtrude","SWEPT_FACE",FACE,{"disambiguationData":[OSD([sQuery(id+"F2.wireOp",EDGE,"E390.MirrorC")])]}),makeQuery(id+"F5.opSweep","SWEPT_FACE",FACE,{"disambiguationData":[OSD([sQuery(id+"F0.wireOp",EDGE,"E0"),sQuery(id+"F3.wireOp",EDGE,"E618.0")])]})]});
            var Q34;
            Q34=makeQuery(id+"F6.opBoolean","INTERSECT",EDGE,{"derivedFrom":[makeQuery(id+"F4.opExtrude","SWEPT_FACE",FACE,{"disambiguationData":[OSD([sQuery(id+"F2.wireOp",EDGE,"E390.MirrorC")])]}),makeQuery(id+"F5.opSweep","SWEPT_FACE",FACE,{"disambiguationData":[OSD([sQuery(id+"F0.wireOp",EDGE,"E0"),sQuery(id+"F3.wireOp",EDGE,"E618.1")])]})]});
            var Q35;
            Q35=makeQuery(id+"F6.opBoolean","INTERSECT",EDGE,{"derivedFrom":[makeQuery(id+"F4.opExtrude","SWEPT_FACE",FACE,{"disambiguationData":[OSD([sQuery(id+"F2.wireOp",EDGE,"E425.MirrorC")])]}),makeQuery(id+"F5.opSweep","SWEPT_FACE",FACE,{"disambiguationData":[OSD([sQuery(id+"F0.wireOp",EDGE,"E0"),sQuery(id+"F3.wireOp",EDGE,"E618.1")])]})]});
            var Q36;
            Q36=makeQuery(id+"F6.opBoolean","INTERSECT",EDGE,{"derivedFrom":[makeQuery(id+"F4.opExtrude","SWEPT_FACE",FACE,{"disambiguationData":[OSD([sQuery(id+"F2.wireOp",EDGE,"E380.MirrorC")])]}),makeQuery(id+"F5.opSweep","SWEPT_FACE",FACE,{"disambiguationData":[OSD([sQuery(id+"F0.wireOp",EDGE,"E0"),sQuery(id+"F3.wireOp",EDGE,"E618.0")])]})]});
            var Q37;
            Q37=makeQuery(id+"F6.opBoolean","INTERSECT",EDGE,{"derivedFrom":[makeQuery(id+"F4.opExtrude","SWEPT_FACE",FACE,{"disambiguationData":[OSD([sQuery(id+"F2.wireOp",EDGE,"E380.MirrorC")])]}),makeQuery(id+"F5.opSweep","SWEPT_FACE",FACE,{"disambiguationData":[OSD([sQuery(id+"F0.wireOp",EDGE,"E0"),sQuery(id+"F3.wireOp",EDGE,"E618.1")])]})]});
            var Q38;
            Q38=makeQuery(id+"F6.opBoolean","INTERSECT",EDGE,{"derivedFrom":[makeQuery(id+"F4.opExtrude","SWEPT_FACE",FACE,{"disambiguationData":[OSD([sQuery(id+"F2.wireOp",EDGE,"E334.MirrorC")])]}),makeQuery(id+"F5.opSweep","SWEPT_FACE",FACE,{"disambiguationData":[OSD([sQuery(id+"F0.wireOp",EDGE,"E0"),sQuery(id+"F3.wireOp",EDGE,"E618.1")])]})]});
            var Q39;
            Q39=makeQuery(id+"F6.opBoolean","INTERSECT",EDGE,{"derivedFrom":[makeQuery(id+"F4.opExtrude","SWEPT_FACE",FACE,{"disambiguationData":[OSD([sQuery(id+"F2.wireOp",EDGE,"E334.MirrorC")])]}),makeQuery(id+"F5.opSweep","SWEPT_FACE",FACE,{"disambiguationData":[OSD([sQuery(id+"F0.wireOp",EDGE,"E0"),sQuery(id+"F3.wireOp",EDGE,"E618.0")])]})]});
            var Q40;
            Q40=makeQuery(id+"F6.opBoolean","INTERSECT",EDGE,{"derivedFrom":[makeQuery(id+"F4.opExtrude","SWEPT_FACE",FACE,{"disambiguationData":[OSD([sQuery(id+"F2.wireOp",EDGE,"E437.MirrorC")])]}),makeQuery(id+"F5.opSweep","SWEPT_FACE",FACE,{"disambiguationData":[OSD([sQuery(id+"F0.wireOp",EDGE,"E0"),sQuery(id+"F3.wireOp",EDGE,"E618.0")])]})]});
            var Q41;
            Q41=makeQuery(id+"F6.opBoolean","INTERSECT",EDGE,{"derivedFrom":[makeQuery(id+"F4.opExtrude","SWEPT_FACE",FACE,{"disambiguationData":[OSD([sQuery(id+"F2.wireOp",EDGE,"E437.MirrorC")])]}),makeQuery(id+"F5.opSweep","SWEPT_FACE",FACE,{"disambiguationData":[OSD([sQuery(id+"F0.wireOp",EDGE,"E0"),sQuery(id+"F3.wireOp",EDGE,"E618.1")])]})]});
            var Q42;
            Q42=makeQuery(id+"F6.opBoolean","INTERSECT",EDGE,{"derivedFrom":[makeQuery(id+"F4.opExtrude","SWEPT_FACE",FACE,{"disambiguationData":[OSD([sQuery(id+"F2.wireOp",EDGE,"E385.MirrorC")])]}),makeQuery(id+"F5.opSweep","SWEPT_FACE",FACE,{"disambiguationData":[OSD([sQuery(id+"F0.wireOp",EDGE,"E0"),sQuery(id+"F3.wireOp",EDGE,"E618.1")])]})]});
            var Q43;
            Q43=makeQuery(id+"F6.opBoolean","INTERSECT",EDGE,{"derivedFrom":[makeQuery(id+"F4.opExtrude","SWEPT_FACE",FACE,{"disambiguationData":[OSD([sQuery(id+"F2.wireOp",EDGE,"E385.MirrorC")])]}),makeQuery(id+"F5.opSweep","SWEPT_FACE",FACE,{"disambiguationData":[OSD([sQuery(id+"F0.wireOp",EDGE,"E0"),sQuery(id+"F3.wireOp",EDGE,"E618.0")])]})]});
            var Q44;
            Q44=makeQuery(id+"F6.opBoolean","INTERSECT",EDGE,{"derivedFrom":[makeQuery(id+"F4.opExtrude","SWEPT_FACE",FACE,{"disambiguationData":[OSD([sQuery(id+"F2.wireOp",EDGE,"E412.MirrorC")])]}),makeQuery(id+"F5.opSweep","SWEPT_FACE",FACE,{"disambiguationData":[OSD([sQuery(id+"F0.wireOp",EDGE,"E0"),sQuery(id+"F3.wireOp",EDGE,"E618.1")])]})]});
            var Q45;
            Q45=makeQuery(id+"F6.opBoolean","INTERSECT",EDGE,{"derivedFrom":[makeQuery(id+"F4.opExtrude","SWEPT_FACE",FACE,{"disambiguationData":[OSD([sQuery(id+"F2.wireOp",EDGE,"E412.MirrorC")])]}),makeQuery(id+"F5.opSweep","SWEPT_FACE",FACE,{"disambiguationData":[OSD([sQuery(id+"F0.wireOp",EDGE,"E0"),sQuery(id+"F3.wireOp",EDGE,"E618.0")])]})]});
            var Q46;
            Q46=makeQuery(id+"F6.opBoolean","INTERSECT",EDGE,{"derivedFrom":[makeQuery(id+"F4.opExtrude","SWEPT_FACE",FACE,{"disambiguationData":[OSD([sQuery(id+"F2.wireOp",EDGE,"E419.MirrorC")])]}),makeQuery(id+"F5.opSweep","SWEPT_FACE",FACE,{"disambiguationData":[OSD([sQuery(id+"F0.wireOp",EDGE,"E0"),sQuery(id+"F3.wireOp",EDGE,"E618.0")])]})]});
            var Q47;
            Q47=makeQuery(id+"F6.opBoolean","INTERSECT",EDGE,{"derivedFrom":[makeQuery(id+"F4.opExtrude","SWEPT_FACE",FACE,{"disambiguationData":[OSD([sQuery(id+"F2.wireOp",EDGE,"E419.MirrorC")])]}),makeQuery(id+"F5.opSweep","SWEPT_FACE",FACE,{"disambiguationData":[OSD([sQuery(id+"F0.wireOp",EDGE,"E0"),sQuery(id+"F3.wireOp",EDGE,"E618.1")])]})]});
            var Q48;
            Q48=makeQuery(id+"F6.opBoolean","INTERSECT",EDGE,{"derivedFrom":[makeQuery(id+"F4.opExtrude","SWEPT_FACE",FACE,{"disambiguationData":[OSD([sQuery(id+"F2.wireOp",EDGE,"E349.MirrorC")])]}),makeQuery(id+"F5.opSweep","SWEPT_FACE",FACE,{"disambiguationData":[OSD([sQuery(id+"F0.wireOp",EDGE,"E0"),sQuery(id+"F3.wireOp",EDGE,"E618.1")])]})]});
            var Q49;
            Q49=makeQuery(id+"F6.opBoolean","INTERSECT",EDGE,{"derivedFrom":[makeQuery(id+"F4.opExtrude","SWEPT_FACE",FACE,{"disambiguationData":[OSD([sQuery(id+"F2.wireOp",EDGE,"E419.MirrorC")])]}),makeQuery(id+"F5.opSweep","SWEPT_FACE",FACE,{"disambiguationData":[OSD([sQuery(id+"F0.wireOp",EDGE,"E0"),sQuery(id+"F3.wireOp",EDGE,"E618.0")])]})]});
            var Q50;
            Q50=makeQuery(id+"F6.opBoolean","INTERSECT",EDGE,{"derivedFrom":[makeQuery(id+"F4.opExtrude","SWEPT_FACE",FACE,{"disambiguationData":[OSD([sQuery(id+"F2.wireOp",EDGE,"E349.MirrorC")])]}),makeQuery(id+"F5.opSweep","SWEPT_FACE",FACE,{"disambiguationData":[OSD([sQuery(id+"F0.wireOp",EDGE,"E0"),sQuery(id+"F3.wireOp",EDGE,"E618.0")])]})]});
            var Q51;
            Q51=makeQuery(id+"F6.opBoolean","INTERSECT",EDGE,{"derivedFrom":[makeQuery(id+"F4.opExtrude","SWEPT_FACE",FACE,{"disambiguationData":[OSD([sQuery(id+"F2.wireOp",EDGE,"E351.MirrorC")])]}),makeQuery(id+"F5.opSweep","SWEPT_FACE",FACE,{"disambiguationData":[OSD([sQuery(id+"F0.wireOp",EDGE,"E0"),sQuery(id+"F3.wireOp",EDGE,"E618.0")])]})]});
            var Q52;
            Q52=makeQuery(id+"F6.opBoolean","INTERSECT",EDGE,{"derivedFrom":[makeQuery(id+"F4.opExtrude","SWEPT_FACE",FACE,{"disambiguationData":[OSD([sQuery(id+"F2.wireOp",EDGE,"E351.MirrorC")])]}),makeQuery(id+"F5.opSweep","SWEPT_FACE",FACE,{"disambiguationData":[OSD([sQuery(id+"F0.wireOp",EDGE,"E0"),sQuery(id+"F3.wireOp",EDGE,"E618.1")])]})]});
            var Q53;
            Q53=makeQuery(id+"F6.opBoolean","INTERSECT",EDGE,{"derivedFrom":[makeQuery(id+"F4.opExtrude","SWEPT_FACE",FACE,{"disambiguationData":[OSD([sQuery(id+"F2.wireOp",EDGE,"E323.MirrorC")])]}),makeQuery(id+"F5.opSweep","SWEPT_FACE",FACE,{"disambiguationData":[OSD([sQuery(id+"F0.wireOp",EDGE,"E0"),sQuery(id+"F3.wireOp",EDGE,"E618.1")])]})]});
            var Q54;
            Q54=makeQuery(id+"F6.opBoolean","INTERSECT",EDGE,{"derivedFrom":[makeQuery(id+"F4.opExtrude","SWEPT_FACE",FACE,{"disambiguationData":[OSD([sQuery(id+"F2.wireOp",EDGE,"E323.MirrorC")])]}),makeQuery(id+"F5.opSweep","SWEPT_FACE",FACE,{"disambiguationData":[OSD([sQuery(id+"F0.wireOp",EDGE,"E0"),sQuery(id+"F3.wireOp",EDGE,"E618.0")])]})]});
            var Q55;
            Q55=makeQuery(id+"F6.opBoolean","INTERSECT",EDGE,{"derivedFrom":[makeQuery(id+"F4.opExtrude","SWEPT_FACE",FACE,{"disambiguationData":[OSD([sQuery(id+"F2.wireOp",EDGE,"E401.MirrorC")])]}),makeQuery(id+"F5.opSweep","SWEPT_FACE",FACE,{"disambiguationData":[OSD([sQuery(id+"F0.wireOp",EDGE,"E0"),sQuery(id+"F3.wireOp",EDGE,"E618.0")])]})]});
            var Q56;
            Q56=makeQuery(id+"F6.opBoolean","INTERSECT",EDGE,{"derivedFrom":[makeQuery(id+"F4.opExtrude","SWEPT_FACE",FACE,{"disambiguationData":[OSD([sQuery(id+"F2.wireOp",EDGE,"E401.MirrorC")])]}),makeQuery(id+"F5.opSweep","SWEPT_FACE",FACE,{"disambiguationData":[OSD([sQuery(id+"F0.wireOp",EDGE,"E0"),sQuery(id+"F3.wireOp",EDGE,"E618.1")])]})]});
            var Q57;
            Q57=makeQuery(id+"F6.opBoolean","INTERSECT",EDGE,{"derivedFrom":[makeQuery(id+"F4.opExtrude","SWEPT_FACE",FACE,{"disambiguationData":[OSD([sQuery(id+"F2.wireOp",EDGE,"E406.MirrorC")])]}),makeQuery(id+"F5.opSweep","SWEPT_FACE",FACE,{"disambiguationData":[OSD([sQuery(id+"F0.wireOp",EDGE,"E0"),sQuery(id+"F3.wireOp",EDGE,"E618.1")])]})]});
            var Q58;
            Q58=makeQuery(id+"F6.opBoolean","INTERSECT",EDGE,{"derivedFrom":[makeQuery(id+"F4.opExtrude","SWEPT_FACE",FACE,{"disambiguationData":[OSD([sQuery(id+"F2.wireOp",EDGE,"E406.MirrorC")])]}),makeQuery(id+"F5.opSweep","SWEPT_FACE",FACE,{"disambiguationData":[OSD([sQuery(id+"F0.wireOp",EDGE,"E0"),sQuery(id+"F3.wireOp",EDGE,"E618.0")])]})]});
            var Q59;
            Q59=makeQuery(id+"F6.opBoolean","INTERSECT",EDGE,{"derivedFrom":[makeQuery(id+"F4.opExtrude","SWEPT_FACE",FACE,{"disambiguationData":[OSD([sQuery(id+"F2.wireOp",EDGE,"E357.MirrorC")])]}),makeQuery(id+"F5.opSweep","SWEPT_FACE",FACE,{"disambiguationData":[OSD([sQuery(id+"F0.wireOp",EDGE,"E0"),sQuery(id+"F3.wireOp",EDGE,"E618.0")])]})]});
            var Q60;
            Q60=makeQuery(id+"F6.opBoolean","INTERSECT",EDGE,{"derivedFrom":[makeQuery(id+"F4.opExtrude","SWEPT_FACE",FACE,{"disambiguationData":[OSD([sQuery(id+"F2.wireOp",EDGE,"E357.MirrorC")])]}),makeQuery(id+"F5.opSweep","SWEPT_FACE",FACE,{"disambiguationData":[OSD([sQuery(id+"F0.wireOp",EDGE,"E0"),sQuery(id+"F3.wireOp",EDGE,"E618.1")])]})]});
            var Q61;
            Q61=makeQuery(id+"F6.opBoolean","INTERSECT",EDGE,{"derivedFrom":[makeQuery(id+"F4.opExtrude","SWEPT_FACE",FACE,{"disambiguationData":[OSD([sQuery(id+"F2.wireOp",EDGE,"E407.MirrorC")])]}),makeQuery(id+"F5.opSweep","SWEPT_FACE",FACE,{"disambiguationData":[OSD([sQuery(id+"F0.wireOp",EDGE,"E0"),sQuery(id+"F3.wireOp",EDGE,"E618.0")])]})]});
            var Q62;
            Q62=makeQuery(id+"F6.opBoolean","INTERSECT",EDGE,{"derivedFrom":[makeQuery(id+"F4.opExtrude","SWEPT_FACE",FACE,{"disambiguationData":[OSD([sQuery(id+"F2.wireOp",EDGE,"E407.MirrorC")])]}),makeQuery(id+"F5.opSweep","SWEPT_FACE",FACE,{"disambiguationData":[OSD([sQuery(id+"F0.wireOp",EDGE,"E0"),sQuery(id+"F3.wireOp",EDGE,"E618.1")])]})]});
            var Q63;
            Q63=makeQuery(id+"F6.opBoolean","INTERSECT",EDGE,{"derivedFrom":[makeQuery(id+"F4.opExtrude","SWEPT_FACE",FACE,{"disambiguationData":[OSD([sQuery(id+"F2.wireOp",EDGE,"E330.MirrorC")])]}),makeQuery(id+"F5.opSweep","SWEPT_FACE",FACE,{"disambiguationData":[OSD([sQuery(id+"F0.wireOp",EDGE,"E0"),sQuery(id+"F3.wireOp",EDGE,"E618.1")])]})]});
            var Q64;
            Q64=makeQuery(id+"F6.opBoolean","INTERSECT",EDGE,{"derivedFrom":[makeQuery(id+"F4.opExtrude","SWEPT_FACE",FACE,{"disambiguationData":[OSD([sQuery(id+"F2.wireOp",EDGE,"E330.MirrorC")])]}),makeQuery(id+"F5.opSweep","SWEPT_FACE",FACE,{"disambiguationData":[OSD([sQuery(id+"F0.wireOp",EDGE,"E0"),sQuery(id+"F3.wireOp",EDGE,"E618.0")])]})]});
            var Q65;
            Q65=makeQuery(id+"F6.opBoolean","INTERSECT",EDGE,{"derivedFrom":[makeQuery(id+"F4.opExtrude","SWEPT_FACE",FACE,{"disambiguationData":[OSD([sQuery(id+"F2.wireOp",EDGE,"E335.MirrorC")])]}),makeQuery(id+"F5.opSweep","SWEPT_FACE",FACE,{"disambiguationData":[OSD([sQuery(id+"F0.wireOp",EDGE,"E0"),sQuery(id+"F3.wireOp",EDGE,"E618.0")])]})]});
            var Q66;
            Q66=makeQuery(id+"F6.opBoolean","INTERSECT",EDGE,{"derivedFrom":[makeQuery(id+"F4.opExtrude","SWEPT_FACE",FACE,{"disambiguationData":[OSD([sQuery(id+"F2.wireOp",EDGE,"E335.MirrorC")])]}),makeQuery(id+"F5.opSweep","SWEPT_FACE",FACE,{"disambiguationData":[OSD([sQuery(id+"F0.wireOp",EDGE,"E0"),sQuery(id+"F3.wireOp",EDGE,"E618.1")])]})]});
            var Q67;
            Q67=makeQuery(id+"F6.opBoolean","INTERSECT",EDGE,{"derivedFrom":[makeQuery(id+"F4.opExtrude","SWEPT_FACE",FACE,{"disambiguationData":[OSD([sQuery(id+"F2.wireOp",EDGE,"E393.MirrorC")])]}),makeQuery(id+"F5.opSweep","SWEPT_FACE",FACE,{"disambiguationData":[OSD([sQuery(id+"F0.wireOp",EDGE,"E0"),sQuery(id+"F3.wireOp",EDGE,"E618.1")])]})]});
            var Q68;
            Q68=makeQuery(id+"F6.opBoolean","INTERSECT",EDGE,{"derivedFrom":[makeQuery(id+"F4.opExtrude","SWEPT_FACE",FACE,{"disambiguationData":[OSD([sQuery(id+"F2.wireOp",EDGE,"E393.MirrorC")])]}),makeQuery(id+"F5.opSweep","SWEPT_FACE",FACE,{"disambiguationData":[OSD([sQuery(id+"F0.wireOp",EDGE,"E0"),sQuery(id+"F3.wireOp",EDGE,"E618.0")])]})]});
            var Q69;
            Q69=makeQuery(id+"F6.opBoolean","INTERSECT",EDGE,{"derivedFrom":[makeQuery(id+"F4.opExtrude","SWEPT_FACE",FACE,{"disambiguationData":[OSD([sQuery(id+"F2.wireOp",EDGE,"E400.MirrorC")])]}),makeQuery(id+"F5.opSweep","SWEPT_FACE",FACE,{"disambiguationData":[OSD([sQuery(id+"F0.wireOp",EDGE,"E0"),sQuery(id+"F3.wireOp",EDGE,"E618.0")])]})]});
            var Q70;
            Q70=makeQuery(id+"F6.opBoolean","INTERSECT",EDGE,{"derivedFrom":[makeQuery(id+"F4.opExtrude","SWEPT_FACE",FACE,{"disambiguationData":[OSD([sQuery(id+"F2.wireOp",EDGE,"E400.MirrorC")])]}),makeQuery(id+"F5.opSweep","SWEPT_FACE",FACE,{"disambiguationData":[OSD([sQuery(id+"F0.wireOp",EDGE,"E0"),sQuery(id+"F3.wireOp",EDGE,"E618.1")])]})]});
            var Q71;
            Q71=makeQuery(id+"F6.opBoolean","INTERSECT",EDGE,{"derivedFrom":[makeQuery(id+"F4.opExtrude","SWEPT_FACE",FACE,{"disambiguationData":[OSD([sQuery(id+"F2.wireOp",EDGE,"E366.MirrorC")])]}),makeQuery(id+"F5.opSweep","SWEPT_FACE",FACE,{"disambiguationData":[OSD([sQuery(id+"F0.wireOp",EDGE,"E0"),sQuery(id+"F3.wireOp",EDGE,"E618.1")])]})]});
            var Q72;
            Q72=makeQuery(id+"F6.opBoolean","INTERSECT",EDGE,{"derivedFrom":[makeQuery(id+"F4.opExtrude","SWEPT_FACE",FACE,{"disambiguationData":[OSD([sQuery(id+"F2.wireOp",EDGE,"E366.MirrorC")])]}),makeQuery(id+"F5.opSweep","SWEPT_FACE",FACE,{"disambiguationData":[OSD([sQuery(id+"F0.wireOp",EDGE,"E0"),sQuery(id+"F3.wireOp",EDGE,"E618.0")])]})]});
            var Q73;
            Q73=makeQuery(id+"F6.opBoolean","INTERSECT",EDGE,{"derivedFrom":[makeQuery(id+"F4.opExtrude","SWEPT_FACE",FACE,{"disambiguationData":[OSD([sQuery(id+"F2.wireOp",EDGE,"E371.MirrorC")])]}),makeQuery(id+"F5.opSweep","SWEPT_FACE",FACE,{"disambiguationData":[OSD([sQuery(id+"F0.wireOp",EDGE,"E0"),sQuery(id+"F3.wireOp",EDGE,"E618.0")])]})]});
            var Q74;
            Q74=makeQuery(id+"F6.opBoolean","INTERSECT",EDGE,{"derivedFrom":[makeQuery(id+"F4.opExtrude","SWEPT_FACE",FACE,{"disambiguationData":[OSD([sQuery(id+"F2.wireOp",EDGE,"E371.MirrorC")])]}),makeQuery(id+"F5.opSweep","SWEPT_FACE",FACE,{"disambiguationData":[OSD([sQuery(id+"F0.wireOp",EDGE,"E0"),sQuery(id+"F3.wireOp",EDGE,"E618.1")])]})]});
            var Q75;
            Q75=makeQuery(id+"F6.opBoolean","INTERSECT",EDGE,{"derivedFrom":[makeQuery(id+"F4.opExtrude","SWEPT_FACE",FACE,{"disambiguationData":[OSD([sQuery(id+"F2.wireOp",EDGE,"E431.MirrorC")])]}),makeQuery(id+"F5.opSweep","SWEPT_FACE",FACE,{"disambiguationData":[OSD([sQuery(id+"F0.wireOp",EDGE,"E0"),sQuery(id+"F3.wireOp",EDGE,"E618.0")])]})]});
            var Q76;
            Q76=makeQuery(id+"F6.opBoolean","INTERSECT",EDGE,{"derivedFrom":[makeQuery(id+"F4.opExtrude","SWEPT_FACE",FACE,{"disambiguationData":[OSD([sQuery(id+"F2.wireOp",EDGE,"E431.MirrorC")])]}),makeQuery(id+"F5.opSweep","SWEPT_FACE",FACE,{"disambiguationData":[OSD([sQuery(id+"F0.wireOp",EDGE,"E0"),sQuery(id+"F3.wireOp",EDGE,"E618.1")])]})]});
            var Q77;
            Q77=makeQuery(id+"F6.opBoolean","INTERSECT",EDGE,{"derivedFrom":[makeQuery(id+"F4.opExtrude","SWEPT_FACE",FACE,{"disambiguationData":[OSD([sQuery(id+"F2.wireOp",EDGE,"E415.MirrorC")])]}),makeQuery(id+"F5.opSweep","SWEPT_FACE",FACE,{"disambiguationData":[OSD([sQuery(id+"F0.wireOp",EDGE,"E0"),sQuery(id+"F3.wireOp",EDGE,"E618.0")])]})]});
            var Q78;
            Q78=makeQuery(id+"F6.opBoolean","INTERSECT",EDGE,{"derivedFrom":[makeQuery(id+"F4.opExtrude","SWEPT_FACE",FACE,{"disambiguationData":[OSD([sQuery(id+"F2.wireOp",EDGE,"E415.MirrorC")])]}),makeQuery(id+"F5.opSweep","SWEPT_FACE",FACE,{"disambiguationData":[OSD([sQuery(id+"F0.wireOp",EDGE,"E0"),sQuery(id+"F3.wireOp",EDGE,"E618.1")])]})]});
            var Q79;
            Q79=makeQuery(id+"F6.opBoolean","INTERSECT",EDGE,{"derivedFrom":[makeQuery(id+"F4.opExtrude","SWEPT_FACE",FACE,{"disambiguationData":[OSD([sQuery(id+"F2.wireOp",EDGE,"E414.MirrorC")])]}),makeQuery(id+"F5.opSweep","SWEPT_FACE",FACE,{"disambiguationData":[OSD([sQuery(id+"F0.wireOp",EDGE,"E0"),sQuery(id+"F3.wireOp",EDGE,"E618.0")])]})]});
            var Q80;
            Q80=makeQuery(id+"F6.opBoolean","INTERSECT",EDGE,{"derivedFrom":[makeQuery(id+"F4.opExtrude","SWEPT_FACE",FACE,{"disambiguationData":[OSD([sQuery(id+"F2.wireOp",EDGE,"E414.MirrorC")])]}),makeQuery(id+"F5.opSweep","SWEPT_FACE",FACE,{"disambiguationData":[OSD([sQuery(id+"F0.wireOp",EDGE,"E0"),sQuery(id+"F3.wireOp",EDGE,"E618.1")])]})]});
            var Q81;
            Q81=makeQuery(id+"F6.opBoolean","INTERSECT",EDGE,{"derivedFrom":[makeQuery(id+"F4.opExtrude","SWEPT_FACE",FACE,{"disambiguationData":[OSD([sQuery(id+"F2.wireOp",EDGE,"E347.MirrorC")])]}),makeQuery(id+"F5.opSweep","SWEPT_FACE",FACE,{"disambiguationData":[OSD([sQuery(id+"F0.wireOp",EDGE,"E0"),sQuery(id+"F3.wireOp",EDGE,"E618.0")])]})]});
            var Q82;
            Q82=makeQuery(id+"F6.opBoolean","INTERSECT",EDGE,{"derivedFrom":[makeQuery(id+"F4.opExtrude","SWEPT_FACE",FACE,{"disambiguationData":[OSD([sQuery(id+"F2.wireOp",EDGE,"E347.MirrorC")])]}),makeQuery(id+"F5.opSweep","SWEPT_FACE",FACE,{"disambiguationData":[OSD([sQuery(id+"F0.wireOp",EDGE,"E0"),sQuery(id+"F3.wireOp",EDGE,"E618.1")])]})]});
            var Q83;
            Q83=makeQuery(id+"F6.opBoolean","INTERSECT",EDGE,{"derivedFrom":[makeQuery(id+"F4.opExtrude","SWEPT_FACE",FACE,{"disambiguationData":[OSD([sQuery(id+"F2.wireOp",EDGE,"E115")])]}),makeQuery(id+"F5.opSweep","SWEPT_FACE",FACE,{"disambiguationData":[OSD([sQuery(id+"F0.wireOp",EDGE,"E0"),sQuery(id+"F3.wireOp",EDGE,"E618.1")])]})]});
            var Q84;
            Q84=makeQuery(id+"F6.opBoolean","INTERSECT",EDGE,{"derivedFrom":[makeQuery(id+"F4.opExtrude","SWEPT_FACE",FACE,{"disambiguationData":[OSD([sQuery(id+"F2.wireOp",EDGE,"E115")])]}),makeQuery(id+"F5.opSweep","SWEPT_FACE",FACE,{"disambiguationData":[OSD([sQuery(id+"F0.wireOp",EDGE,"E0"),sQuery(id+"F3.wireOp",EDGE,"E618.0")])]})]});
            var Q85;
            Q85=makeQuery(id+"F6.opBoolean","INTERSECT",EDGE,{"derivedFrom":[makeQuery(id+"F4.opExtrude","SWEPT_FACE",FACE,{"disambiguationData":[OSD([sQuery(id+"F2.wireOp",EDGE,"E117")])]}),makeQuery(id+"F5.opSweep","SWEPT_FACE",FACE,{"disambiguationData":[OSD([sQuery(id+"F0.wireOp",EDGE,"E0"),sQuery(id+"F3.wireOp",EDGE,"E618.1")])]})]});
            var Q86;
            Q86=makeQuery(id+"F6.opBoolean","INTERSECT",EDGE,{"derivedFrom":[makeQuery(id+"F4.opExtrude","SWEPT_FACE",FACE,{"disambiguationData":[OSD([sQuery(id+"F2.wireOp",EDGE,"E117")])]}),makeQuery(id+"F5.opSweep","SWEPT_FACE",FACE,{"disambiguationData":[OSD([sQuery(id+"F0.wireOp",EDGE,"E0"),sQuery(id+"F3.wireOp",EDGE,"E618.0")])]})]});
            var Q87;
            Q87=makeQuery(id+"F6.opBoolean","INTERSECT",EDGE,{"derivedFrom":[makeQuery(id+"F4.opExtrude","SWEPT_FACE",FACE,{"disambiguationData":[OSD([sQuery(id+"F2.wireOp",EDGE,"E120")])]}),makeQuery(id+"F5.opSweep","SWEPT_FACE",FACE,{"disambiguationData":[OSD([sQuery(id+"F0.wireOp",EDGE,"E0"),sQuery(id+"F3.wireOp",EDGE,"E618.1")])]})]});
            var Q88;
            Q88=makeQuery(id+"F6.opBoolean","INTERSECT",EDGE,{"derivedFrom":[makeQuery(id+"F4.opExtrude","SWEPT_FACE",FACE,{"disambiguationData":[OSD([sQuery(id+"F2.wireOp",EDGE,"E120")])]}),makeQuery(id+"F5.opSweep","SWEPT_FACE",FACE,{"disambiguationData":[OSD([sQuery(id+"F0.wireOp",EDGE,"E0"),sQuery(id+"F3.wireOp",EDGE,"E618.0")])]})]});
            var Q89;
            Q89=makeQuery(id+"F6.opBoolean","INTERSECT",EDGE,{"derivedFrom":[makeQuery(id+"F4.opExtrude","SWEPT_FACE",FACE,{"disambiguationData":[OSD([sQuery(id+"F2.wireOp",EDGE,"E121")])]}),makeQuery(id+"F5.opSweep","SWEPT_FACE",FACE,{"disambiguationData":[OSD([sQuery(id+"F0.wireOp",EDGE,"E0"),sQuery(id+"F3.wireOp",EDGE,"E618.1")])]})]});
            var Q90;
            Q90=makeQuery(id+"F6.opBoolean","INTERSECT",EDGE,{"derivedFrom":[makeQuery(id+"F4.opExtrude","SWEPT_FACE",FACE,{"disambiguationData":[OSD([sQuery(id+"F2.wireOp",EDGE,"E121")])]}),makeQuery(id+"F5.opSweep","SWEPT_FACE",FACE,{"disambiguationData":[OSD([sQuery(id+"F0.wireOp",EDGE,"E0"),sQuery(id+"F3.wireOp",EDGE,"E618.0")])]})]});
            var Q91;
            Q91=makeQuery(id+"F6.opBoolean","INTERSECT",EDGE,{"derivedFrom":[makeQuery(id+"F4.opExtrude","SWEPT_FACE",FACE,{"disambiguationData":[OSD([sQuery(id+"F2.wireOp",EDGE,"E123")])]}),makeQuery(id+"F5.opSweep","SWEPT_FACE",FACE,{"disambiguationData":[OSD([sQuery(id+"F0.wireOp",EDGE,"E0"),sQuery(id+"F3.wireOp",EDGE,"E618.0")])]})]});
            var Q92;
            Q92=makeQuery(id+"F6.opBoolean","INTERSECT",EDGE,{"derivedFrom":[makeQuery(id+"F4.opExtrude","SWEPT_FACE",FACE,{"disambiguationData":[OSD([sQuery(id+"F2.wireOp",EDGE,"E123")])]}),makeQuery(id+"F5.opSweep","SWEPT_FACE",FACE,{"disambiguationData":[OSD([sQuery(id+"F0.wireOp",EDGE,"E0"),sQuery(id+"F3.wireOp",EDGE,"E618.1")])]})]});
            var Q93;
            Q93=makeQuery(id+"F6.opBoolean","INTERSECT",EDGE,{"derivedFrom":[makeQuery(id+"F4.opExtrude","SWEPT_FACE",FACE,{"disambiguationData":[OSD([sQuery(id+"F2.wireOp",EDGE,"E125")])]}),makeQuery(id+"F5.opSweep","SWEPT_FACE",FACE,{"disambiguationData":[OSD([sQuery(id+"F0.wireOp",EDGE,"E0"),sQuery(id+"F3.wireOp",EDGE,"E618.1")])]})]});
            var Q94;
            Q94=makeQuery(id+"F6.opBoolean","INTERSECT",EDGE,{"derivedFrom":[makeQuery(id+"F4.opExtrude","SWEPT_FACE",FACE,{"disambiguationData":[OSD([sQuery(id+"F2.wireOp",EDGE,"E125")])]}),makeQuery(id+"F5.opSweep","SWEPT_FACE",FACE,{"disambiguationData":[OSD([sQuery(id+"F0.wireOp",EDGE,"E0"),sQuery(id+"F3.wireOp",EDGE,"E618.0")])]})]});
            var Q95;
            Q95=makeQuery(id+"F6.opBoolean","INTERSECT",EDGE,{"derivedFrom":[makeQuery(id+"F4.opExtrude","SWEPT_FACE",FACE,{"disambiguationData":[OSD([sQuery(id+"F2.wireOp",EDGE,"E127")])]}),makeQuery(id+"F5.opSweep","SWEPT_FACE",FACE,{"disambiguationData":[OSD([sQuery(id+"F0.wireOp",EDGE,"E0"),sQuery(id+"F3.wireOp",EDGE,"E618.0")])]})]});
            var Q96;
            Q96=makeQuery(id+"F6.opBoolean","INTERSECT",EDGE,{"derivedFrom":[makeQuery(id+"F4.opExtrude","SWEPT_FACE",FACE,{"disambiguationData":[OSD([sQuery(id+"F2.wireOp",EDGE,"E127")])]}),makeQuery(id+"F5.opSweep","SWEPT_FACE",FACE,{"disambiguationData":[OSD([sQuery(id+"F0.wireOp",EDGE,"E0"),sQuery(id+"F3.wireOp",EDGE,"E618.1")])]})]});
            var Q97;
            Q97=makeQuery(id+"F6.opBoolean","INTERSECT",EDGE,{"derivedFrom":[makeQuery(id+"F4.opExtrude","SWEPT_FACE",FACE,{"disambiguationData":[OSD([sQuery(id+"F2.wireOp",EDGE,"E129")])]}),makeQuery(id+"F5.opSweep","SWEPT_FACE",FACE,{"disambiguationData":[OSD([sQuery(id+"F0.wireOp",EDGE,"E0"),sQuery(id+"F3.wireOp",EDGE,"E618.1")])]})]});
            var Q98;
            Q98=makeQuery(id+"F6.opBoolean","INTERSECT",EDGE,{"derivedFrom":[makeQuery(id+"F4.opExtrude","SWEPT_FACE",FACE,{"disambiguationData":[OSD([sQuery(id+"F2.wireOp",EDGE,"E129")])]}),makeQuery(id+"F5.opSweep","SWEPT_FACE",FACE,{"disambiguationData":[OSD([sQuery(id+"F0.wireOp",EDGE,"E0"),sQuery(id+"F3.wireOp",EDGE,"E618.0")])]})]});
            var Q99;
            Q99=makeQuery(id+"F6.opBoolean","INTERSECT",EDGE,{"derivedFrom":[makeQuery(id+"F4.opExtrude","SWEPT_FACE",FACE,{"disambiguationData":[OSD([sQuery(id+"F2.wireOp",EDGE,"E131")])]}),makeQuery(id+"F5.opSweep","SWEPT_FACE",FACE,{"disambiguationData":[OSD([sQuery(id+"F0.wireOp",EDGE,"E0"),sQuery(id+"F3.wireOp",EDGE,"E618.0")])]})]});
            var Q100;
            Q100=makeQuery(id+"F6.opBoolean","INTERSECT",EDGE,{"derivedFrom":[makeQuery(id+"F4.opExtrude","SWEPT_FACE",FACE,{"disambiguationData":[OSD([sQuery(id+"F2.wireOp",EDGE,"E131")])]}),makeQuery(id+"F5.opSweep","SWEPT_FACE",FACE,{"disambiguationData":[OSD([sQuery(id+"F0.wireOp",EDGE,"E0"),sQuery(id+"F3.wireOp",EDGE,"E618.1")])]})]});
            var Q101;
            Q101=makeQuery(id+"F6.opBoolean","INTERSECT",EDGE,{"derivedFrom":[makeQuery(id+"F4.opExtrude","SWEPT_FACE",FACE,{"disambiguationData":[OSD([sQuery(id+"F2.wireOp",EDGE,"E134")])]}),makeQuery(id+"F5.opSweep","SWEPT_FACE",FACE,{"disambiguationData":[OSD([sQuery(id+"F0.wireOp",EDGE,"E0"),sQuery(id+"F3.wireOp",EDGE,"E618.1")])]})]});
            var Q102;
            Q102=makeQuery(id+"F6.opBoolean","INTERSECT",EDGE,{"derivedFrom":[makeQuery(id+"F4.opExtrude","SWEPT_FACE",FACE,{"disambiguationData":[OSD([sQuery(id+"F2.wireOp",EDGE,"E134")])]}),makeQuery(id+"F5.opSweep","SWEPT_FACE",FACE,{"disambiguationData":[OSD([sQuery(id+"F0.wireOp",EDGE,"E0"),sQuery(id+"F3.wireOp",EDGE,"E618.0")])]})]});
            var Q103;
            Q103=makeQuery(id+"F6.opBoolean","INTERSECT",EDGE,{"derivedFrom":[makeQuery(id+"F4.opExtrude","SWEPT_FACE",FACE,{"disambiguationData":[OSD([sQuery(id+"F2.wireOp",EDGE,"E135")])]}),makeQuery(id+"F5.opSweep","SWEPT_FACE",FACE,{"disambiguationData":[OSD([sQuery(id+"F0.wireOp",EDGE,"E0"),sQuery(id+"F3.wireOp",EDGE,"E618.0")])]})]});
            var Q104;
            Q104=makeQuery(id+"F6.opBoolean","INTERSECT",EDGE,{"derivedFrom":[makeQuery(id+"F4.opExtrude","SWEPT_FACE",FACE,{"disambiguationData":[OSD([sQuery(id+"F2.wireOp",EDGE,"E135")])]}),makeQuery(id+"F5.opSweep","SWEPT_FACE",FACE,{"disambiguationData":[OSD([sQuery(id+"F0.wireOp",EDGE,"E0"),sQuery(id+"F3.wireOp",EDGE,"E618.1")])]})]});
            var Q105;
            Q105=makeQuery(id+"F6.opBoolean","INTERSECT",EDGE,{"derivedFrom":[makeQuery(id+"F4.opExtrude","SWEPT_FACE",FACE,{"disambiguationData":[OSD([sQuery(id+"F2.wireOp",EDGE,"E136")])]}),makeQuery(id+"F5.opSweep","SWEPT_FACE",FACE,{"disambiguationData":[OSD([sQuery(id+"F0.wireOp",EDGE,"E0"),sQuery(id+"F3.wireOp",EDGE,"E618.1")])]})]});
            var Q106;
            Q106=makeQuery(id+"F6.opBoolean","INTERSECT",EDGE,{"derivedFrom":[makeQuery(id+"F4.opExtrude","SWEPT_FACE",FACE,{"disambiguationData":[OSD([sQuery(id+"F2.wireOp",EDGE,"E136")])]}),makeQuery(id+"F5.opSweep","SWEPT_FACE",FACE,{"disambiguationData":[OSD([sQuery(id+"F0.wireOp",EDGE,"E0"),sQuery(id+"F3.wireOp",EDGE,"E618.0")])]})]});
            var Q107;
            Q107=makeQuery(id+"F6.opBoolean","INTERSECT",EDGE,{"derivedFrom":[makeQuery(id+"F4.opExtrude","SWEPT_FACE",FACE,{"disambiguationData":[OSD([sQuery(id+"F2.wireOp",EDGE,"E144")])]}),makeQuery(id+"F5.opSweep","SWEPT_FACE",FACE,{"disambiguationData":[OSD([sQuery(id+"F0.wireOp",EDGE,"E0"),sQuery(id+"F3.wireOp",EDGE,"E618.0")])]})]});
            var Q108;
            Q108=makeQuery(id+"F6.opBoolean","INTERSECT",EDGE,{"derivedFrom":[makeQuery(id+"F4.opExtrude","SWEPT_FACE",FACE,{"disambiguationData":[OSD([sQuery(id+"F2.wireOp",EDGE,"E144")])]}),makeQuery(id+"F5.opSweep","SWEPT_FACE",FACE,{"disambiguationData":[OSD([sQuery(id+"F0.wireOp",EDGE,"E0"),sQuery(id+"F3.wireOp",EDGE,"E618.1")])]})]});
            var Q109;
            Q109=makeQuery(id+"F6.opBoolean","INTERSECT",EDGE,{"derivedFrom":[makeQuery(id+"F4.opExtrude","SWEPT_FACE",FACE,{"disambiguationData":[OSD([sQuery(id+"F2.wireOp",EDGE,"E143")])]}),makeQuery(id+"F5.opSweep","SWEPT_FACE",FACE,{"disambiguationData":[OSD([sQuery(id+"F0.wireOp",EDGE,"E0"),sQuery(id+"F3.wireOp",EDGE,"E618.1")])]})]});
            var Q110;
            Q110=makeQuery(id+"F6.opBoolean","INTERSECT",EDGE,{"derivedFrom":[makeQuery(id+"F4.opExtrude","SWEPT_FACE",FACE,{"disambiguationData":[OSD([sQuery(id+"F2.wireOp",EDGE,"E143")])]}),makeQuery(id+"F5.opSweep","SWEPT_FACE",FACE,{"disambiguationData":[OSD([sQuery(id+"F0.wireOp",EDGE,"E0"),sQuery(id+"F3.wireOp",EDGE,"E618.0")])]})]});
            var Q111;
            Q111=makeQuery(id+"F6.opBoolean","INTERSECT",EDGE,{"derivedFrom":[makeQuery(id+"F4.opExtrude","SWEPT_FACE",FACE,{"disambiguationData":[OSD([sQuery(id+"F2.wireOp",EDGE,"E142")])]}),makeQuery(id+"F5.opSweep","SWEPT_FACE",FACE,{"disambiguationData":[OSD([sQuery(id+"F0.wireOp",EDGE,"E0"),sQuery(id+"F3.wireOp",EDGE,"E618.1")])]})]});
            var Q112;
            Q112=makeQuery(id+"F6.opBoolean","INTERSECT",EDGE,{"derivedFrom":[makeQuery(id+"F4.opExtrude","SWEPT_FACE",FACE,{"disambiguationData":[OSD([sQuery(id+"F2.wireOp",EDGE,"E142")])]}),makeQuery(id+"F5.opSweep","SWEPT_FACE",FACE,{"disambiguationData":[OSD([sQuery(id+"F0.wireOp",EDGE,"E0"),sQuery(id+"F3.wireOp",EDGE,"E618.0")])]})]});
            var Q113;
            Q113=makeQuery(id+"F6.opBoolean","INTERSECT",EDGE,{"derivedFrom":[makeQuery(id+"F4.opExtrude","SWEPT_FACE",FACE,{"disambiguationData":[OSD([sQuery(id+"F2.wireOp",EDGE,"E18")])]}),makeQuery(id+"F5.opSweep","SWEPT_FACE",FACE,{"disambiguationData":[OSD([sQuery(id+"F0.wireOp",EDGE,"E0"),sQuery(id+"F3.wireOp",EDGE,"E618.1")])]})]});
            var Q114;
            Q114=makeQuery(id+"F6.opBoolean","INTERSECT",EDGE,{"derivedFrom":[makeQuery(id+"F4.opExtrude","SWEPT_FACE",FACE,{"disambiguationData":[OSD([sQuery(id+"F2.wireOp",EDGE,"E18")])]}),makeQuery(id+"F5.opSweep","SWEPT_FACE",FACE,{"disambiguationData":[OSD([sQuery(id+"F0.wireOp",EDGE,"E0"),sQuery(id+"F3.wireOp",EDGE,"E618.0")])]})]});
            var Q115;
            Q115=makeQuery(id+"F6.opBoolean","INTERSECT",EDGE,{"derivedFrom":[makeQuery(id+"F4.opExtrude","SWEPT_FACE",FACE,{"disambiguationData":[OSD([sQuery(id+"F2.wireOp",EDGE,"E288.MirrorC")])]}),makeQuery(id+"F5.opSweep","SWEPT_FACE",FACE,{"disambiguationData":[OSD([sQuery(id+"F0.wireOp",EDGE,"E0"),sQuery(id+"F3.wireOp",EDGE,"E618.1")])]})]});
            var Q116;
            Q116=makeQuery(id+"F6.opBoolean","INTERSECT",EDGE,{"derivedFrom":[makeQuery(id+"F4.opExtrude","SWEPT_FACE",FACE,{"disambiguationData":[OSD([sQuery(id+"F2.wireOp",EDGE,"E288.MirrorC")])]}),makeQuery(id+"F5.opSweep","SWEPT_FACE",FACE,{"disambiguationData":[OSD([sQuery(id+"F0.wireOp",EDGE,"E0"),sQuery(id+"F3.wireOp",EDGE,"E618.0")])]})]});
            var Q117;
            Q117=makeQuery(id+"F6.opBoolean","INTERSECT",EDGE,{"derivedFrom":[makeQuery(id+"F4.opExtrude","SWEPT_FACE",FACE,{"disambiguationData":[OSD([sQuery(id+"F2.wireOp",EDGE,"E256.MirrorC")])]}),makeQuery(id+"F5.opSweep","SWEPT_FACE",FACE,{"disambiguationData":[OSD([sQuery(id+"F0.wireOp",EDGE,"E0"),sQuery(id+"F3.wireOp",EDGE,"E618.1")])]})]});
            var Q118;
            Q118=makeQuery(id+"F6.opBoolean","INTERSECT",EDGE,{"derivedFrom":[makeQuery(id+"F4.opExtrude","SWEPT_FACE",FACE,{"disambiguationData":[OSD([sQuery(id+"F2.wireOp",EDGE,"E256.MirrorC")])]}),makeQuery(id+"F5.opSweep","SWEPT_FACE",FACE,{"disambiguationData":[OSD([sQuery(id+"F0.wireOp",EDGE,"E0"),sQuery(id+"F3.wireOp",EDGE,"E618.0")])]})]});
            var Q119;
            Q119=makeQuery(id+"F6.opBoolean","INTERSECT",EDGE,{"derivedFrom":[makeQuery(id+"F4.opExtrude","SWEPT_FACE",FACE,{"disambiguationData":[OSD([sQuery(id+"F2.wireOp",EDGE,"E204.MirrorC")])]}),makeQuery(id+"F5.opSweep","SWEPT_FACE",FACE,{"disambiguationData":[OSD([sQuery(id+"F0.wireOp",EDGE,"E0"),sQuery(id+"F3.wireOp",EDGE,"E618.0")])]})]});
            var Q120;
            Q120=makeQuery(id+"F6.opBoolean","INTERSECT",EDGE,{"derivedFrom":[makeQuery(id+"F4.opExtrude","SWEPT_FACE",FACE,{"disambiguationData":[OSD([sQuery(id+"F2.wireOp",EDGE,"E204.MirrorC")])]}),makeQuery(id+"F5.opSweep","SWEPT_FACE",FACE,{"disambiguationData":[OSD([sQuery(id+"F0.wireOp",EDGE,"E0"),sQuery(id+"F3.wireOp",EDGE,"E618.1")])]})]});
            var Q121;
            Q121=makeQuery(id+"F6.opBoolean","INTERSECT",EDGE,{"derivedFrom":[makeQuery(id+"F4.opExtrude","SWEPT_FACE",FACE,{"disambiguationData":[OSD([sQuery(id+"F2.wireOp",EDGE,"E218.MirrorC")])]}),makeQuery(id+"F5.opSweep","SWEPT_FACE",FACE,{"disambiguationData":[OSD([sQuery(id+"F0.wireOp",EDGE,"E0"),sQuery(id+"F3.wireOp",EDGE,"E618.1")])]})]});
            var Q122;
            Q122=makeQuery(id+"F6.opBoolean","INTERSECT",EDGE,{"derivedFrom":[makeQuery(id+"F4.opExtrude","SWEPT_FACE",FACE,{"disambiguationData":[OSD([sQuery(id+"F2.wireOp",EDGE,"E218.MirrorC")])]}),makeQuery(id+"F5.opSweep","SWEPT_FACE",FACE,{"disambiguationData":[OSD([sQuery(id+"F0.wireOp",EDGE,"E0"),sQuery(id+"F3.wireOp",EDGE,"E618.0")])]})]});
            var Q123;
            Q123=makeQuery(id+"F6.opBoolean","INTERSECT",EDGE,{"derivedFrom":[makeQuery(id+"F4.opExtrude","SWEPT_FACE",FACE,{"disambiguationData":[OSD([sQuery(id+"F2.wireOp",EDGE,"E268.MirrorC")])]}),makeQuery(id+"F5.opSweep","SWEPT_FACE",FACE,{"disambiguationData":[OSD([sQuery(id+"F0.wireOp",EDGE,"E0"),sQuery(id+"F3.wireOp",EDGE,"E618.0")])]})]});
            var Q124;
            Q124=makeQuery(id+"F6.opBoolean","INTERSECT",EDGE,{"derivedFrom":[makeQuery(id+"F4.opExtrude","SWEPT_FACE",FACE,{"disambiguationData":[OSD([sQuery(id+"F2.wireOp",EDGE,"E268.MirrorC")])]}),makeQuery(id+"F5.opSweep","SWEPT_FACE",FACE,{"disambiguationData":[OSD([sQuery(id+"F0.wireOp",EDGE,"E0"),sQuery(id+"F3.wireOp",EDGE,"E618.1")])]})]});
            var Q125;
            Q125=makeQuery(id+"F6.opBoolean","INTERSECT",EDGE,{"derivedFrom":[makeQuery(id+"F4.opExtrude","SWEPT_FACE",FACE,{"disambiguationData":[OSD([sQuery(id+"F2.wireOp",EDGE,"E173.MirrorC")])]}),makeQuery(id+"F5.opSweep","SWEPT_FACE",FACE,{"disambiguationData":[OSD([sQuery(id+"F0.wireOp",EDGE,"E0"),sQuery(id+"F3.wireOp",EDGE,"E618.1")])]})]});
            var Q126;
            Q126=makeQuery(id+"F6.opBoolean","INTERSECT",EDGE,{"derivedFrom":[makeQuery(id+"F4.opExtrude","SWEPT_FACE",FACE,{"disambiguationData":[OSD([sQuery(id+"F2.wireOp",EDGE,"E173.MirrorC")])]}),makeQuery(id+"F5.opSweep","SWEPT_FACE",FACE,{"disambiguationData":[OSD([sQuery(id+"F0.wireOp",EDGE,"E0"),sQuery(id+"F3.wireOp",EDGE,"E618.0")])]})]});
            var Q127;
            Q127=makeQuery(id+"F6.opBoolean","INTERSECT",EDGE,{"derivedFrom":[makeQuery(id+"F4.opExtrude","SWEPT_FACE",FACE,{"disambiguationData":[OSD([sQuery(id+"F2.wireOp",EDGE,"E226.MirrorC")])]}),makeQuery(id+"F5.opSweep","SWEPT_FACE",FACE,{"disambiguationData":[OSD([sQuery(id+"F0.wireOp",EDGE,"E0"),sQuery(id+"F3.wireOp",EDGE,"E618.1")])]})]});
            var Q128;
            Q128=makeQuery(id+"F6.opBoolean","INTERSECT",EDGE,{"derivedFrom":[makeQuery(id+"F4.opExtrude","SWEPT_FACE",FACE,{"disambiguationData":[OSD([sQuery(id+"F2.wireOp",EDGE,"E226.MirrorC")])]}),makeQuery(id+"F5.opSweep","SWEPT_FACE",FACE,{"disambiguationData":[OSD([sQuery(id+"F0.wireOp",EDGE,"E0"),sQuery(id+"F3.wireOp",EDGE,"E618.0")])]})]});
            var Q129;
            Q129=makeQuery(id+"F6.opBoolean","INTERSECT",EDGE,{"derivedFrom":[makeQuery(id+"F4.opExtrude","SWEPT_FACE",FACE,{"disambiguationData":[OSD([sQuery(id+"F2.wireOp",EDGE,"E229.MirrorC")])]}),makeQuery(id+"F5.opSweep","SWEPT_FACE",FACE,{"disambiguationData":[OSD([sQuery(id+"F0.wireOp",EDGE,"E0"),sQuery(id+"F3.wireOp",EDGE,"E618.1")])]})]});
            var Q130;
            Q130=makeQuery(id+"F6.opBoolean","INTERSECT",EDGE,{"derivedFrom":[makeQuery(id+"F4.opExtrude","SWEPT_FACE",FACE,{"disambiguationData":[OSD([sQuery(id+"F2.wireOp",EDGE,"E229.MirrorC")])]}),makeQuery(id+"F5.opSweep","SWEPT_FACE",FACE,{"disambiguationData":[OSD([sQuery(id+"F0.wireOp",EDGE,"E0"),sQuery(id+"F3.wireOp",EDGE,"E618.0")])]})]});
            var Q131;
            Q131=makeQuery(id+"F6.opBoolean","INTERSECT",EDGE,{"derivedFrom":[makeQuery(id+"F4.opExtrude","SWEPT_FACE",FACE,{"disambiguationData":[OSD([sQuery(id+"F2.wireOp",EDGE,"E255.MirrorC")])]}),makeQuery(id+"F5.opSweep","SWEPT_FACE",FACE,{"disambiguationData":[OSD([sQuery(id+"F0.wireOp",EDGE,"E0"),sQuery(id+"F3.wireOp",EDGE,"E618.1")])]})]});
            var Q132;
            Q132=makeQuery(id+"F6.opBoolean","INTERSECT",EDGE,{"derivedFrom":[makeQuery(id+"F4.opExtrude","SWEPT_FACE",FACE,{"disambiguationData":[OSD([sQuery(id+"F2.wireOp",EDGE,"E255.MirrorC")])]}),makeQuery(id+"F5.opSweep","SWEPT_FACE",FACE,{"disambiguationData":[OSD([sQuery(id+"F0.wireOp",EDGE,"E0"),sQuery(id+"F3.wireOp",EDGE,"E618.0")])]})]});
            var Q133;
            Q133=makeQuery(id+"F6.opBoolean","INTERSECT",EDGE,{"derivedFrom":[makeQuery(id+"F4.opExtrude","SWEPT_FACE",FACE,{"disambiguationData":[OSD([sQuery(id+"F2.wireOp",EDGE,"E317.MirrorC")])]}),makeQuery(id+"F5.opSweep","SWEPT_FACE",FACE,{"disambiguationData":[OSD([sQuery(id+"F0.wireOp",EDGE,"E0"),sQuery(id+"F3.wireOp",EDGE,"E618.0")])]})]});
            var Q134;
            Q134=makeQuery(id+"F6.opBoolean","INTERSECT",EDGE,{"derivedFrom":[makeQuery(id+"F4.opExtrude","SWEPT_FACE",FACE,{"disambiguationData":[OSD([sQuery(id+"F2.wireOp",EDGE,"E317.MirrorC")])]}),makeQuery(id+"F5.opSweep","SWEPT_FACE",FACE,{"disambiguationData":[OSD([sQuery(id+"F0.wireOp",EDGE,"E0"),sQuery(id+"F3.wireOp",EDGE,"E618.1")])]})]});
            var Q135;
            Q135=makeQuery(id+"F6.opBoolean","INTERSECT",EDGE,{"derivedFrom":[makeQuery(id+"F4.opExtrude","SWEPT_FACE",FACE,{"disambiguationData":[OSD([sQuery(id+"F2.wireOp",EDGE,"E297.MirrorC")])]}),makeQuery(id+"F5.opSweep","SWEPT_FACE",FACE,{"disambiguationData":[OSD([sQuery(id+"F0.wireOp",EDGE,"E0"),sQuery(id+"F3.wireOp",EDGE,"E618.1")])]})]});
            var Q136;
            Q136=makeQuery(id+"F6.opBoolean","INTERSECT",EDGE,{"derivedFrom":[makeQuery(id+"F4.opExtrude","SWEPT_FACE",FACE,{"disambiguationData":[OSD([sQuery(id+"F2.wireOp",EDGE,"E297.MirrorC")])]}),makeQuery(id+"F5.opSweep","SWEPT_FACE",FACE,{"disambiguationData":[OSD([sQuery(id+"F0.wireOp",EDGE,"E0"),sQuery(id+"F3.wireOp",EDGE,"E618.0")])]})]});
            var Q137;
            Q137=makeQuery(id+"F6.opBoolean","INTERSECT",EDGE,{"derivedFrom":[makeQuery(id+"F4.opExtrude","SWEPT_FACE",FACE,{"disambiguationData":[OSD([sQuery(id+"F2.wireOp",EDGE,"E252.MirrorC")])]}),makeQuery(id+"F5.opSweep","SWEPT_FACE",FACE,{"disambiguationData":[OSD([sQuery(id+"F0.wireOp",EDGE,"E0"),sQuery(id+"F3.wireOp",EDGE,"E618.1")])]})]});
            var Q138;
            Q138=makeQuery(id+"F6.opBoolean","INTERSECT",EDGE,{"derivedFrom":[makeQuery(id+"F4.opExtrude","SWEPT_FACE",FACE,{"disambiguationData":[OSD([sQuery(id+"F2.wireOp",EDGE,"E252.MirrorC")])]}),makeQuery(id+"F5.opSweep","SWEPT_FACE",FACE,{"disambiguationData":[OSD([sQuery(id+"F0.wireOp",EDGE,"E0"),sQuery(id+"F3.wireOp",EDGE,"E618.0")])]})]});
            var Q139;
            Q139=makeQuery(id+"F8.boolean.opBoolean","COPY",FACE,{"disambiguationData":[TD([makeQuery(id+"F4.opExtrude","SWEPT_FACE",FACE,{"disambiguationData":[OSD([sQuery(id+"F2.wireOp",EDGE,"E235.MirrorC")])]})])],"derivedFrom":makeQuery(id+"F8.opSweep","SWEPT_FACE",FACE,{"disambiguationData":[OSD([sQuery(id+"F0.wireOp",EDGE,"E0"),sQuery(id+"F7.wireOp",EDGE,"E620.4")])]})});
            var Q140;
            Q140=makeQuery(id+"F8.boolean.opBoolean","COPY",FACE,{"disambiguationData":[TD([makeQuery(id+"F4.opExtrude","SWEPT_FACE",FACE,{"disambiguationData":[OSD([sQuery(id+"F2.wireOp",EDGE,"E269.MirrorC")])]})])],"derivedFrom":makeQuery(id+"F8.opSweep","SWEPT_FACE",FACE,{"disambiguationData":[OSD([sQuery(id+"F0.wireOp",EDGE,"E0"),sQuery(id+"F7.wireOp",EDGE,"E620.4")])]})});
            var Q141;
            Q141=makeQuery(id+"F8.boolean.opBoolean","COPY",FACE,{"disambiguationData":[TD([makeQuery(id+"F4.opExtrude","SWEPT_FACE",FACE,{"disambiguationData":[OSD([sQuery(id+"F2.wireOp",EDGE,"E265.MirrorC")])]})])],"derivedFrom":makeQuery(id+"F8.opSweep","SWEPT_FACE",FACE,{"disambiguationData":[OSD([sQuery(id+"F0.wireOp",EDGE,"E0"),sQuery(id+"F7.wireOp",EDGE,"E620.4")])]})});
            var Q142;
            Q142=makeQuery(id+"F8.boolean.opBoolean","COPY",FACE,{"disambiguationData":[TD([makeQuery(id+"F4.opExtrude","SWEPT_FACE",FACE,{"disambiguationData":[OSD([sQuery(id+"F2.wireOp",EDGE,"E287.MirrorC")])]})])],"derivedFrom":makeQuery(id+"F8.opSweep","SWEPT_FACE",FACE,{"disambiguationData":[OSD([sQuery(id+"F0.wireOp",EDGE,"E0"),sQuery(id+"F7.wireOp",EDGE,"E620.4")])]})});
            var Q143;
            Q143=makeQuery(id+"F8.boolean.opBoolean","COPY",FACE,{"disambiguationData":[TD([makeQuery(id+"F4.opExtrude","SWEPT_FACE",FACE,{"disambiguationData":[OSD([sQuery(id+"F2.wireOp",EDGE,"E292.MirrorC")])]})])],"derivedFrom":makeQuery(id+"F8.opSweep","SWEPT_FACE",FACE,{"disambiguationData":[OSD([sQuery(id+"F0.wireOp",EDGE,"E0"),sQuery(id+"F7.wireOp",EDGE,"E620.4")])]})});
            var Q144;
            Q144=makeQuery(id+"F8.boolean.opBoolean","COPY",FACE,{"disambiguationData":[TD([makeQuery(id+"F4.opExtrude","SWEPT_FACE",FACE,{"disambiguationData":[OSD([sQuery(id+"F2.wireOp",EDGE,"E275.MirrorC")])]})])],"derivedFrom":makeQuery(id+"F8.opSweep","SWEPT_FACE",FACE,{"disambiguationData":[OSD([sQuery(id+"F0.wireOp",EDGE,"E0"),sQuery(id+"F7.wireOp",EDGE,"E620.4")])]})});
            var Q145;
            Q145=makeQuery(id+"F8.boolean.opBoolean","COPY",FACE,{"disambiguationData":[TD([makeQuery(id+"F4.opExtrude","SWEPT_FACE",FACE,{"disambiguationData":[OSD([sQuery(id+"F2.wireOp",EDGE,"E282.MirrorC")])]})])],"derivedFrom":makeQuery(id+"F8.opSweep","SWEPT_FACE",FACE,{"disambiguationData":[OSD([sQuery(id+"F0.wireOp",EDGE,"E0"),sQuery(id+"F7.wireOp",EDGE,"E620.4")])]})});
            var Q146;
            Q146=makeQuery(id+"F8.boolean.opBoolean","COPY",FACE,{"disambiguationData":[TD([makeQuery(id+"F4.opExtrude","SWEPT_FACE",FACE,{"disambiguationData":[OSD([sQuery(id+"F2.wireOp",EDGE,"E176.MirrorC")])]})])],"derivedFrom":makeQuery(id+"F8.opSweep","SWEPT_FACE",FACE,{"disambiguationData":[OSD([sQuery(id+"F0.wireOp",EDGE,"E0"),sQuery(id+"F7.wireOp",EDGE,"E620.4")])]})});
            var Q147;
            Q147=makeQuery(id+"F6.opBoolean","INTERSECT",EDGE,{"derivedFrom":[makeQuery(id+"F4.opExtrude","SWEPT_FACE",FACE,{"disambiguationData":[OSD([sQuery(id+"F2.wireOp",EDGE,"E203.MirrorC")])]}),makeQuery(id+"F5.opSweep","SWEPT_FACE",FACE,{"disambiguationData":[OSD([sQuery(id+"F0.wireOp",EDGE,"E0"),sQuery(id+"F3.wireOp",EDGE,"E618.0")])]})]});
            var Q148;
            Q148=makeQuery(id+"F8.boolean.opBoolean","COPY",FACE,{"disambiguationData":[TD([makeQuery(id+"F4.opExtrude","SWEPT_FACE",FACE,{"disambiguationData":[OSD([sQuery(id+"F2.wireOp",EDGE,"E187.MirrorC")])]})])],"derivedFrom":makeQuery(id+"F8.opSweep","SWEPT_FACE",FACE,{"disambiguationData":[OSD([sQuery(id+"F0.wireOp",EDGE,"E0"),sQuery(id+"F7.wireOp",EDGE,"E620.4")])]})});
            var Q149;
            Q149=makeQuery(id+"F8.boolean.opBoolean","COPY",FACE,{"disambiguationData":[TD([makeQuery(id+"F4.opExtrude","SWEPT_FACE",FACE,{"disambiguationData":[OSD([sQuery(id+"F2.wireOp",EDGE,"E304.MirrorC")])]})])],"derivedFrom":makeQuery(id+"F8.opSweep","SWEPT_FACE",FACE,{"disambiguationData":[OSD([sQuery(id+"F0.wireOp",EDGE,"E0"),sQuery(id+"F7.wireOp",EDGE,"E620.4")])]})});
            var Q150;
            Q150=makeQuery(id+"F8.boolean.opBoolean","COPY",FACE,{"disambiguationData":[TD([makeQuery(id+"F4.opExtrude","SWEPT_FACE",FACE,{"disambiguationData":[OSD([sQuery(id+"F2.wireOp",EDGE,"E211.MirrorC")])]})])],"derivedFrom":makeQuery(id+"F8.opSweep","SWEPT_FACE",FACE,{"disambiguationData":[OSD([sQuery(id+"F0.wireOp",EDGE,"E0"),sQuery(id+"F7.wireOp",EDGE,"E620.4")])]})});
            var Q151;
            Q151=makeQuery(id+"F8.boolean.opBoolean","COPY",FACE,{"disambiguationData":[TD([makeQuery(id+"F4.opExtrude","SWEPT_FACE",FACE,{"disambiguationData":[OSD([sQuery(id+"F2.wireOp",EDGE,"E199.MirrorC")])]})])],"derivedFrom":makeQuery(id+"F8.opSweep","SWEPT_FACE",FACE,{"disambiguationData":[OSD([sQuery(id+"F0.wireOp",EDGE,"E0"),sQuery(id+"F7.wireOp",EDGE,"E620.4")])]})});
            var Q152;
            Q152=makeQuery(id+"F8.boolean.opBoolean","COPY",FACE,{"disambiguationData":[TD([makeQuery(id+"F4.opExtrude","SWEPT_FACE",FACE,{"disambiguationData":[OSD([sQuery(id+"F2.wireOp",EDGE,"E231.MirrorC")])]})])],"derivedFrom":makeQuery(id+"F8.opSweep","SWEPT_FACE",FACE,{"disambiguationData":[OSD([sQuery(id+"F0.wireOp",EDGE,"E0"),sQuery(id+"F7.wireOp",EDGE,"E620.4")])]})});
            var Q153;
            Q153=makeQuery(id+"F8.boolean.opBoolean","COPY",FACE,{"disambiguationData":[TD([makeQuery(id+"F4.opExtrude","SWEPT_FACE",FACE,{"disambiguationData":[OSD([sQuery(id+"F2.wireOp",EDGE,"E185.MirrorC")])]})])],"derivedFrom":makeQuery(id+"F8.opSweep","SWEPT_FACE",FACE,{"disambiguationData":[OSD([sQuery(id+"F0.wireOp",EDGE,"E0"),sQuery(id+"F7.wireOp",EDGE,"E620.4")])]})});
            var Q154;
            Q154=makeQuery(id+"F8.boolean.opBoolean","COPY",FACE,{"disambiguationData":[TD([makeQuery(id+"F4.opExtrude","SWEPT_FACE",FACE,{"disambiguationData":[OSD([sQuery(id+"F2.wireOp",EDGE,"E312.MirrorC")])]})])],"derivedFrom":makeQuery(id+"F8.opSweep","SWEPT_FACE",FACE,{"disambiguationData":[OSD([sQuery(id+"F0.wireOp",EDGE,"E0"),sQuery(id+"F7.wireOp",EDGE,"E620.4")])]})});
            var Q155;
            Q155=makeQuery(id+"F8.boolean.opBoolean","COPY",FACE,{"disambiguationData":[TD([makeQuery(id+"F4.opExtrude","SWEPT_FACE",FACE,{"disambiguationData":[OSD([sQuery(id+"F2.wireOp",EDGE,"E249.MirrorC")])]})])],"derivedFrom":makeQuery(id+"F8.opSweep","SWEPT_FACE",FACE,{"disambiguationData":[OSD([sQuery(id+"F0.wireOp",EDGE,"E0"),sQuery(id+"F7.wireOp",EDGE,"E620.4")])]})});
            var Q156;
            Q156=makeQuery(id+"F8.boolean.opBoolean","COPY",FACE,{"disambiguationData":[TD([makeQuery(id+"F4.opExtrude","SWEPT_FACE",FACE,{"disambiguationData":[OSD([sQuery(id+"F2.wireOp",EDGE,"E233.MirrorC")])]})])],"derivedFrom":makeQuery(id+"F8.opSweep","SWEPT_FACE",FACE,{"disambiguationData":[OSD([sQuery(id+"F0.wireOp",EDGE,"E0"),sQuery(id+"F7.wireOp",EDGE,"E620.4")])]})});
            var Q157;
            Q157=makeQuery(id+"F8.boolean.opBoolean","COPY",FACE,{"disambiguationData":[TD([makeQuery(id+"F4.opExtrude","SWEPT_FACE",FACE,{"disambiguationData":[OSD([sQuery(id+"F2.wireOp",EDGE,"E198.MirrorC")])]})])],"derivedFrom":makeQuery(id+"F8.opSweep","SWEPT_FACE",FACE,{"disambiguationData":[OSD([sQuery(id+"F0.wireOp",EDGE,"E0"),sQuery(id+"F7.wireOp",EDGE,"E620.4")])]})});
            var Q158;
            Q158=makeQuery(id+"F8.boolean.opBoolean","COPY",FACE,{"disambiguationData":[TD([makeQuery(id+"F4.opExtrude","SWEPT_FACE",FACE,{"disambiguationData":[OSD([sQuery(id+"F2.wireOp",EDGE,"E201.MirrorC")])]})])],"derivedFrom":makeQuery(id+"F8.opSweep","SWEPT_FACE",FACE,{"disambiguationData":[OSD([sQuery(id+"F0.wireOp",EDGE,"E0"),sQuery(id+"F7.wireOp",EDGE,"E620.4")])]})});
            var Q159;
            Q159=makeQuery(id+"F8.boolean.opBoolean","COPY",FACE,{"disambiguationData":[TD([makeQuery(id+"F4.opExtrude","SWEPT_FACE",FACE,{"disambiguationData":[OSD([sQuery(id+"F2.wireOp",EDGE,"E311.MirrorC")])]})])],"derivedFrom":makeQuery(id+"F8.opSweep","SWEPT_FACE",FACE,{"disambiguationData":[OSD([sQuery(id+"F0.wireOp",EDGE,"E0"),sQuery(id+"F7.wireOp",EDGE,"E620.4")])]})});
            var Q160;
            Q160=makeQuery(id+"F8.boolean.opBoolean","COPY",FACE,{"disambiguationData":[TD([makeQuery(id+"F4.opExtrude","SWEPT_FACE",FACE,{"disambiguationData":[OSD([sQuery(id+"F2.wireOp",EDGE,"E248.MirrorC")])]})])],"derivedFrom":makeQuery(id+"F8.opSweep","SWEPT_FACE",FACE,{"disambiguationData":[OSD([sQuery(id+"F0.wireOp",EDGE,"E0"),sQuery(id+"F7.wireOp",EDGE,"E620.4")])]})});
            var Q161;
            Q161=makeQuery(id+"F8.boolean.opBoolean","COPY",FACE,{"disambiguationData":[TD([makeQuery(id+"F4.opExtrude","SWEPT_FACE",FACE,{"disambiguationData":[OSD([sQuery(id+"F2.wireOp",EDGE,"E291.MirrorC")])]})])],"derivedFrom":makeQuery(id+"F8.opSweep","SWEPT_FACE",FACE,{"disambiguationData":[OSD([sQuery(id+"F0.wireOp",EDGE,"E0"),sQuery(id+"F7.wireOp",EDGE,"E620.4")])]})});
            var Q162;
            Q162=makeQuery(id+"F8.boolean.opBoolean","COPY",FACE,{"disambiguationData":[TD([makeQuery(id+"F4.opExtrude","SWEPT_FACE",FACE,{"disambiguationData":[OSD([sQuery(id+"F2.wireOp",EDGE,"E298.MirrorC")])]})])],"derivedFrom":makeQuery(id+"F8.opSweep","SWEPT_FACE",FACE,{"disambiguationData":[OSD([sQuery(id+"F0.wireOp",EDGE,"E0"),sQuery(id+"F7.wireOp",EDGE,"E620.4")])]})});
            var Q163;
            Q163=makeQuery(id+"F8.boolean.opBoolean","COPY",FACE,{"disambiguationData":[TD([makeQuery(id+"F4.opExtrude","SWEPT_FACE",FACE,{"disambiguationData":[OSD([sQuery(id+"F2.wireOp",EDGE,"E179.MirrorC")])]})])],"derivedFrom":makeQuery(id+"F8.opSweep","SWEPT_FACE",FACE,{"disambiguationData":[OSD([sQuery(id+"F0.wireOp",EDGE,"E0"),sQuery(id+"F7.wireOp",EDGE,"E620.4")])]})});
            var Q164;
            Q164=makeQuery(id+"F8.boolean.opBoolean","COPY",FACE,{"disambiguationData":[TD([makeQuery(id+"F4.opExtrude","SWEPT_FACE",FACE,{"disambiguationData":[OSD([sQuery(id+"F2.wireOp",EDGE,"E26")])]})])],"derivedFrom":makeQuery(id+"F8.opSweep","SWEPT_FACE",FACE,{"disambiguationData":[OSD([sQuery(id+"F0.wireOp",EDGE,"E0"),sQuery(id+"F7.wireOp",EDGE,"E620.4")])]})});
            var Q165;
            Q165=makeQuery(id+"F8.boolean.opBoolean","COPY",FACE,{"disambiguationData":[TD([makeQuery(id+"F4.opExtrude","SWEPT_FACE",FACE,{"disambiguationData":[OSD([sQuery(id+"F2.wireOp",EDGE,"E17")])]})])],"derivedFrom":makeQuery(id+"F8.opSweep","SWEPT_FACE",FACE,{"disambiguationData":[OSD([sQuery(id+"F0.wireOp",EDGE,"E0"),sQuery(id+"F7.wireOp",EDGE,"E620.4")])]})});
            var Q166;
            Q166=makeQuery(id+"F8.boolean.opBoolean","COPY",FACE,{"disambiguationData":[TD([makeQuery(id+"F4.opExtrude","SWEPT_FACE",FACE,{"disambiguationData":[OSD([sQuery(id+"F2.wireOp",EDGE,"E141")])]})])],"derivedFrom":makeQuery(id+"F8.opSweep","SWEPT_FACE",FACE,{"disambiguationData":[OSD([sQuery(id+"F0.wireOp",EDGE,"E0"),sQuery(id+"F7.wireOp",EDGE,"E620.4")])]})});
            var Q167;
            Q167=makeQuery(id+"F8.boolean.opBoolean","COPY",FACE,{"disambiguationData":[TD([makeQuery(id+"F4.opExtrude","SWEPT_FACE",FACE,{"disambiguationData":[OSD([sQuery(id+"F2.wireOp",EDGE,"E159")])]})])],"derivedFrom":makeQuery(id+"F8.opSweep","SWEPT_FACE",FACE,{"disambiguationData":[OSD([sQuery(id+"F0.wireOp",EDGE,"E0"),sQuery(id+"F7.wireOp",EDGE,"E620.4")])]})});
            var Q168;
            Q168=makeQuery(id+"F8.boolean.opBoolean","COPY",FACE,{"disambiguationData":[TD([makeQuery(id+"F4.opExtrude","SWEPT_FACE",FACE,{"disambiguationData":[OSD([sQuery(id+"F2.wireOp",EDGE,"E160")])]})])],"derivedFrom":makeQuery(id+"F8.opSweep","SWEPT_FACE",FACE,{"disambiguationData":[OSD([sQuery(id+"F0.wireOp",EDGE,"E0"),sQuery(id+"F7.wireOp",EDGE,"E620.4")])]})});
            var Q169;
            Q169=makeQuery(id+"F8.boolean.opBoolean","COPY",FACE,{"disambiguationData":[TD([makeQuery(id+"F4.opExtrude","SWEPT_FACE",FACE,{"disambiguationData":[OSD([sQuery(id+"F2.wireOp",EDGE,"E140")])]})])],"derivedFrom":makeQuery(id+"F8.opSweep","SWEPT_FACE",FACE,{"disambiguationData":[OSD([sQuery(id+"F0.wireOp",EDGE,"E0"),sQuery(id+"F7.wireOp",EDGE,"E620.4")])]})});
            var Q170;
            Q170=makeQuery(id+"F8.boolean.opBoolean","COPY",FACE,{"disambiguationData":[TD([makeQuery(id+"F4.opExtrude","SWEPT_FACE",FACE,{"disambiguationData":[OSD([sQuery(id+"F2.wireOp",EDGE,"E161")])]})])],"derivedFrom":makeQuery(id+"F8.opSweep","SWEPT_FACE",FACE,{"disambiguationData":[OSD([sQuery(id+"F0.wireOp",EDGE,"E0"),sQuery(id+"F7.wireOp",EDGE,"E620.4")])]})});
            var Q171;
            Q171=makeQuery(id+"F8.boolean.opBoolean","COPY",FACE,{"disambiguationData":[TD([makeQuery(id+"F4.opExtrude","SWEPT_FACE",FACE,{"disambiguationData":[OSD([sQuery(id+"F2.wireOp",EDGE,"E139")])]})])],"derivedFrom":makeQuery(id+"F8.opSweep","SWEPT_FACE",FACE,{"disambiguationData":[OSD([sQuery(id+"F0.wireOp",EDGE,"E0"),sQuery(id+"F7.wireOp",EDGE,"E620.4")])]})});
            var Q172;
            Q172=makeQuery(id+"F8.boolean.opBoolean","COPY",FACE,{"disambiguationData":[TD([makeQuery(id+"F4.opExtrude","SWEPT_FACE",FACE,{"disambiguationData":[OSD([sQuery(id+"F2.wireOp",EDGE,"E162")])]})])],"derivedFrom":makeQuery(id+"F8.opSweep","SWEPT_FACE",FACE,{"disambiguationData":[OSD([sQuery(id+"F0.wireOp",EDGE,"E0"),sQuery(id+"F7.wireOp",EDGE,"E620.4")])]})});
            var Q173;
            Q173=makeQuery(id+"F8.boolean.opBoolean","COPY",FACE,{"disambiguationData":[TD([makeQuery(id+"F4.opExtrude","SWEPT_FACE",FACE,{"disambiguationData":[OSD([sQuery(id+"F2.wireOp",EDGE,"E138")])]})])],"derivedFrom":makeQuery(id+"F8.opSweep","SWEPT_FACE",FACE,{"disambiguationData":[OSD([sQuery(id+"F0.wireOp",EDGE,"E0"),sQuery(id+"F7.wireOp",EDGE,"E620.4")])]})});
            var Q174;
            Q174=makeQuery(id+"F8.boolean.opBoolean","COPY",FACE,{"disambiguationData":[TD([makeQuery(id+"F4.opExtrude","SWEPT_FACE",FACE,{"disambiguationData":[OSD([sQuery(id+"F2.wireOp",EDGE,"E137")])]})])],"derivedFrom":makeQuery(id+"F8.opSweep","SWEPT_FACE",FACE,{"disambiguationData":[OSD([sQuery(id+"F0.wireOp",EDGE,"E0"),sQuery(id+"F7.wireOp",EDGE,"E620.4")])]})});
            var Q175;
            Q175=makeQuery(id+"F8.boolean.opBoolean","COPY",FACE,{"disambiguationData":[TD([makeQuery(id+"F4.opExtrude","SWEPT_FACE",FACE,{"disambiguationData":[OSD([sQuery(id+"F2.wireOp",EDGE,"E145")])]})])],"derivedFrom":makeQuery(id+"F8.opSweep","SWEPT_FACE",FACE,{"disambiguationData":[OSD([sQuery(id+"F0.wireOp",EDGE,"E0"),sQuery(id+"F7.wireOp",EDGE,"E620.5")])]})});
            var Q176;
            Q176=makeQuery(id+"F8.boolean.opBoolean","COPY",FACE,{"disambiguationData":[TD([makeQuery(id+"F4.opExtrude","SWEPT_FACE",FACE,{"disambiguationData":[OSD([sQuery(id+"F2.wireOp",EDGE,"E25")])]})])],"derivedFrom":makeQuery(id+"F8.opSweep","SWEPT_FACE",FACE,{"disambiguationData":[OSD([sQuery(id+"F0.wireOp",EDGE,"E0"),sQuery(id+"F7.wireOp",EDGE,"E620.5")])]})});
            var Q177;
            Q177=makeQuery(id+"F8.boolean.opBoolean","COPY",FACE,{"disambiguationData":[TD([makeQuery(id+"F4.opExtrude","SWEPT_FACE",FACE,{"disambiguationData":[OSD([sQuery(id+"F2.wireOp",EDGE,"E19")])]})])],"derivedFrom":makeQuery(id+"F8.opSweep","SWEPT_FACE",FACE,{"disambiguationData":[OSD([sQuery(id+"F0.wireOp",EDGE,"E0"),sQuery(id+"F7.wireOp",EDGE,"E620.5")])]})});
            var Q178;
            Q178=makeQuery(id+"F8.boolean.opBoolean","COPY",FACE,{"disambiguationData":[TD([makeQuery(id+"F4.opExtrude","SWEPT_FACE",FACE,{"disambiguationData":[OSD([sQuery(id+"F2.wireOp",EDGE,"E182.MirrorC")])]})])],"derivedFrom":makeQuery(id+"F8.opSweep","SWEPT_FACE",FACE,{"disambiguationData":[OSD([sQuery(id+"F0.wireOp",EDGE,"E0"),sQuery(id+"F7.wireOp",EDGE,"E620.5")])]})});
            var Q179;
            Q179=makeQuery(id+"F8.boolean.opBoolean","COPY",FACE,{"disambiguationData":[TD([makeQuery(id+"F4.opExtrude","SWEPT_FACE",FACE,{"disambiguationData":[OSD([sQuery(id+"F2.wireOp",EDGE,"E195.MirrorC")])]})])],"derivedFrom":makeQuery(id+"F8.opSweep","SWEPT_FACE",FACE,{"disambiguationData":[OSD([sQuery(id+"F0.wireOp",EDGE,"E0"),sQuery(id+"F7.wireOp",EDGE,"E620.5")])]})});
            var Q180;
            Q180=makeQuery(id+"F8.boolean.opBoolean","COPY",FACE,{"disambiguationData":[TD([makeQuery(id+"F4.opExtrude","SWEPT_FACE",FACE,{"disambiguationData":[OSD([sQuery(id+"F2.wireOp",EDGE,"E224.MirrorC")])]})])],"derivedFrom":makeQuery(id+"F8.opSweep","SWEPT_FACE",FACE,{"disambiguationData":[OSD([sQuery(id+"F0.wireOp",EDGE,"E0"),sQuery(id+"F7.wireOp",EDGE,"E620.5")])]})});
            var Q181;
            Q181=makeQuery(id+"F8.boolean.opBoolean","COPY",FACE,{"disambiguationData":[TD([makeQuery(id+"F4.opExtrude","SWEPT_FACE",FACE,{"disambiguationData":[OSD([sQuery(id+"F2.wireOp",EDGE,"E190.MirrorC")])]})])],"derivedFrom":makeQuery(id+"F8.opSweep","SWEPT_FACE",FACE,{"disambiguationData":[OSD([sQuery(id+"F0.wireOp",EDGE,"E0"),sQuery(id+"F7.wireOp",EDGE,"E620.5")])]})});
            var Q182;
            Q182=makeQuery(id+"F8.boolean.opBoolean","COPY",FACE,{"disambiguationData":[TD([makeQuery(id+"F4.opExtrude","SWEPT_FACE",FACE,{"disambiguationData":[OSD([sQuery(id+"F2.wireOp",EDGE,"E303.MirrorC")])]})])],"derivedFrom":makeQuery(id+"F8.opSweep","SWEPT_FACE",FACE,{"disambiguationData":[OSD([sQuery(id+"F0.wireOp",EDGE,"E0"),sQuery(id+"F7.wireOp",EDGE,"E620.5")])]})});
            var Q183;
            Q183=makeQuery(id+"F8.boolean.opBoolean","COPY",FACE,{"disambiguationData":[TD([makeQuery(id+"F4.opExtrude","SWEPT_FACE",FACE,{"disambiguationData":[OSD([sQuery(id+"F2.wireOp",EDGE,"E180.MirrorC")])]})])],"derivedFrom":makeQuery(id+"F8.opSweep","SWEPT_FACE",FACE,{"disambiguationData":[OSD([sQuery(id+"F0.wireOp",EDGE,"E0"),sQuery(id+"F7.wireOp",EDGE,"E620.5")])]})});
            var Q184;
            Q184=makeQuery(id+"F8.boolean.opBoolean","COPY",FACE,{"disambiguationData":[TD([makeQuery(id+"F4.opExtrude","SWEPT_FACE",FACE,{"disambiguationData":[OSD([sQuery(id+"F2.wireOp",EDGE,"E230.MirrorC")])]})])],"derivedFrom":makeQuery(id+"F8.opSweep","SWEPT_FACE",FACE,{"disambiguationData":[OSD([sQuery(id+"F0.wireOp",EDGE,"E0"),sQuery(id+"F7.wireOp",EDGE,"E620.5")])]})});
            var Q185;
            Q185=makeQuery(id+"F8.boolean.opBoolean","COPY",FACE,{"disambiguationData":[TD([makeQuery(id+"F4.opExtrude","SWEPT_FACE",FACE,{"disambiguationData":[OSD([sQuery(id+"F2.wireOp",EDGE,"E315.MirrorC")])]})])],"derivedFrom":makeQuery(id+"F8.opSweep","SWEPT_FACE",FACE,{"disambiguationData":[OSD([sQuery(id+"F0.wireOp",EDGE,"E0"),sQuery(id+"F7.wireOp",EDGE,"E620.5")])]})});
            var Q186;
            Q186=makeQuery(id+"F8.boolean.opBoolean","COPY",FACE,{"disambiguationData":[TD([makeQuery(id+"F4.opExtrude","SWEPT_FACE",FACE,{"disambiguationData":[OSD([sQuery(id+"F2.wireOp",EDGE,"E212.MirrorC")])]})])],"derivedFrom":makeQuery(id+"F8.opSweep","SWEPT_FACE",FACE,{"disambiguationData":[OSD([sQuery(id+"F0.wireOp",EDGE,"E0"),sQuery(id+"F7.wireOp",EDGE,"E620.5")])]})});
            var Q187;
            Q187=makeQuery(id+"F8.boolean.opBoolean","COPY",FACE,{"disambiguationData":[TD([makeQuery(id+"F4.opExtrude","SWEPT_FACE",FACE,{"disambiguationData":[OSD([sQuery(id+"F2.wireOp",EDGE,"E234.MirrorC")])]})])],"derivedFrom":makeQuery(id+"F8.opSweep","SWEPT_FACE",FACE,{"disambiguationData":[OSD([sQuery(id+"F0.wireOp",EDGE,"E0"),sQuery(id+"F7.wireOp",EDGE,"E620.5")])]})});
            var Q188;
            Q188=makeQuery(id+"F8.boolean.opBoolean","COPY",FACE,{"disambiguationData":[TD([makeQuery(id+"F4.opExtrude","SWEPT_FACE",FACE,{"disambiguationData":[OSD([sQuery(id+"F2.wireOp",EDGE,"E186.MirrorC")])]})])],"derivedFrom":makeQuery(id+"F8.opSweep","SWEPT_FACE",FACE,{"disambiguationData":[OSD([sQuery(id+"F0.wireOp",EDGE,"E0"),sQuery(id+"F7.wireOp",EDGE,"E620.5")])]})});
            var Q189;
            Q189=makeQuery(id+"F8.boolean.opBoolean","COPY",FACE,{"disambiguationData":[TD([makeQuery(id+"F4.opExtrude","SWEPT_FACE",FACE,{"disambiguationData":[OSD([sQuery(id+"F2.wireOp",EDGE,"E258.MirrorC")])]})])],"derivedFrom":makeQuery(id+"F8.opSweep","SWEPT_FACE",FACE,{"disambiguationData":[OSD([sQuery(id+"F0.wireOp",EDGE,"E0"),sQuery(id+"F7.wireOp",EDGE,"E620.5")])]})});
            var Q190;
            Q190=makeQuery(id+"F8.boolean.opBoolean","COPY",FACE,{"disambiguationData":[TD([makeQuery(id+"F4.opExtrude","SWEPT_FACE",FACE,{"disambiguationData":[OSD([sQuery(id+"F2.wireOp",EDGE,"E174.MirrorC")])]})])],"derivedFrom":makeQuery(id+"F8.opSweep","SWEPT_FACE",FACE,{"disambiguationData":[OSD([sQuery(id+"F0.wireOp",EDGE,"E0"),sQuery(id+"F7.wireOp",EDGE,"E620.5")])]})});
            var Q191;
            Q191=makeQuery(id+"F8.boolean.opBoolean","COPY",FACE,{"disambiguationData":[TD([makeQuery(id+"F4.opExtrude","SWEPT_FACE",FACE,{"disambiguationData":[OSD([sQuery(id+"F2.wireOp",EDGE,"E245.MirrorC")])]})])],"derivedFrom":makeQuery(id+"F8.opSweep","SWEPT_FACE",FACE,{"disambiguationData":[OSD([sQuery(id+"F0.wireOp",EDGE,"E0"),sQuery(id+"F7.wireOp",EDGE,"E620.5")])]})});
            var Q192;
            Q192=makeQuery(id+"F8.boolean.opBoolean","COPY",FACE,{"disambiguationData":[TD([makeQuery(id+"F4.opExtrude","SWEPT_FACE",FACE,{"disambiguationData":[OSD([sQuery(id+"F2.wireOp",EDGE,"E243.MirrorC")])]})])],"derivedFrom":makeQuery(id+"F8.opSweep","SWEPT_FACE",FACE,{"disambiguationData":[OSD([sQuery(id+"F0.wireOp",EDGE,"E0"),sQuery(id+"F7.wireOp",EDGE,"E620.5")])]})});
            var Q193;
            Q193=makeQuery(id+"F8.boolean.opBoolean","COPY",FACE,{"disambiguationData":[TD([makeQuery(id+"F4.opExtrude","SWEPT_FACE",FACE,{"disambiguationData":[OSD([sQuery(id+"F2.wireOp",EDGE,"E271.MirrorC")])]})])],"derivedFrom":makeQuery(id+"F8.opSweep","SWEPT_FACE",FACE,{"disambiguationData":[OSD([sQuery(id+"F0.wireOp",EDGE,"E0"),sQuery(id+"F7.wireOp",EDGE,"E620.5")])]})});
            var Q194;
            Q194=makeQuery(id+"F8.boolean.opBoolean","COPY",FACE,{"disambiguationData":[TD([makeQuery(id+"F4.opExtrude","SWEPT_FACE",FACE,{"disambiguationData":[OSD([sQuery(id+"F2.wireOp",EDGE,"E246.MirrorC")])]})])],"derivedFrom":makeQuery(id+"F8.opSweep","SWEPT_FACE",FACE,{"disambiguationData":[OSD([sQuery(id+"F0.wireOp",EDGE,"E0"),sQuery(id+"F7.wireOp",EDGE,"E620.5")])]})});
            var Q195;
            Q195=makeQuery(id+"F8.boolean.opBoolean","COPY",FACE,{"disambiguationData":[TD([makeQuery(id+"F4.opExtrude","SWEPT_FACE",FACE,{"disambiguationData":[OSD([sQuery(id+"F2.wireOp",EDGE,"E289.MirrorC")])]})])],"derivedFrom":makeQuery(id+"F8.opSweep","SWEPT_FACE",FACE,{"disambiguationData":[OSD([sQuery(id+"F0.wireOp",EDGE,"E0"),sQuery(id+"F7.wireOp",EDGE,"E620.5")])]})});
            var Q196;
            Q196=makeQuery(id+"F8.boolean.opBoolean","COPY",FACE,{"disambiguationData":[TD([makeQuery(id+"F4.opExtrude","SWEPT_FACE",FACE,{"disambiguationData":[OSD([sQuery(id+"F2.wireOp",EDGE,"E267.MirrorC")])]})])],"derivedFrom":makeQuery(id+"F8.opSweep","SWEPT_FACE",FACE,{"disambiguationData":[OSD([sQuery(id+"F0.wireOp",EDGE,"E0"),sQuery(id+"F7.wireOp",EDGE,"E620.5")])]})});
            var Q197;
            Q197=makeQuery(id+"F8.boolean.opBoolean","COPY",FACE,{"disambiguationData":[TD([makeQuery(id+"F4.opExtrude","SWEPT_FACE",FACE,{"disambiguationData":[OSD([sQuery(id+"F2.wireOp",EDGE,"E285.MirrorC")])]})])],"derivedFrom":makeQuery(id+"F8.opSweep","SWEPT_FACE",FACE,{"disambiguationData":[OSD([sQuery(id+"F0.wireOp",EDGE,"E0"),sQuery(id+"F7.wireOp",EDGE,"E620.5")])]})});
            var Q198;
            Q198=makeQuery(id+"F8.boolean.opBoolean","COPY",FACE,{"disambiguationData":[TD([makeQuery(id+"F4.opExtrude","SWEPT_FACE",FACE,{"disambiguationData":[OSD([sQuery(id+"F2.wireOp",EDGE,"E301.MirrorC")])]})])],"derivedFrom":makeQuery(id+"F8.opSweep","SWEPT_FACE",FACE,{"disambiguationData":[OSD([sQuery(id+"F0.wireOp",EDGE,"E0"),sQuery(id+"F7.wireOp",EDGE,"E620.5")])]})});
            var Q199;
            Q199=makeQuery(id+"F8.boolean.opBoolean","COPY",FACE,{"disambiguationData":[TD([makeQuery(id+"F4.opExtrude","SWEPT_FACE",FACE,{"disambiguationData":[OSD([sQuery(id+"F2.wireOp",EDGE,"E280.MirrorC")])]})])],"derivedFrom":makeQuery(id+"F8.opSweep","SWEPT_FACE",FACE,{"disambiguationData":[OSD([sQuery(id+"F0.wireOp",EDGE,"E0"),sQuery(id+"F7.wireOp",EDGE,"E620.5")])]})});
            var Q200;
            Q200=makeQuery(id+"F8.boolean.opBoolean","COPY",FACE,{"disambiguationData":[TD([makeQuery(id+"F4.opExtrude","SWEPT_FACE",FACE,{"disambiguationData":[OSD([sQuery(id+"F2.wireOp",EDGE,"E270.MirrorC")])]})])],"derivedFrom":makeQuery(id+"F8.opSweep","SWEPT_FACE",FACE,{"disambiguationData":[OSD([sQuery(id+"F0.wireOp",EDGE,"E0"),sQuery(id+"F7.wireOp",EDGE,"E620.5")])]})});
            var Q201;
            Q201=makeQuery(id+"F8.boolean.opBoolean","COPY",FACE,{"disambiguationData":[TD([makeQuery(id+"F4.opExtrude","SWEPT_FACE",FACE,{"disambiguationData":[OSD([sQuery(id+"F2.wireOp",EDGE,"E254.MirrorC")])]})])],"derivedFrom":makeQuery(id+"F8.opSweep","SWEPT_FACE",FACE,{"disambiguationData":[OSD([sQuery(id+"F0.wireOp",EDGE,"E0"),sQuery(id+"F7.wireOp",EDGE,"E620.5")])]})});
            var Q202;
            Q202=makeQuery(id+"F8.boolean.opBoolean","COPY",FACE,{"disambiguationData":[TD([makeQuery(id+"F4.opExtrude","SWEPT_FACE",FACE,{"disambiguationData":[OSD([sQuery(id+"F2.wireOp",EDGE,"E295.MirrorC")])]})])],"derivedFrom":makeQuery(id+"F8.opSweep","SWEPT_FACE",FACE,{"disambiguationData":[OSD([sQuery(id+"F0.wireOp",EDGE,"E0"),sQuery(id+"F7.wireOp",EDGE,"E620.5")])]})});
            var Q203;
            Q203=makeQuery(id+"F8.boolean.opBoolean","COPY",FACE,{"disambiguationData":[TD([makeQuery(id+"F4.opExtrude","SWEPT_FACE",FACE,{"disambiguationData":[OSD([sQuery(id+"F2.wireOp",EDGE,"E100")])]})])],"derivedFrom":makeQuery(id+"F8.opSweep","SWEPT_FACE",FACE,{"disambiguationData":[OSD([sQuery(id+"F0.wireOp",EDGE,"E0"),sQuery(id+"F7.wireOp",EDGE,"E620.5")])]})});
            var Q204;
            Q204=makeQuery(id+"F8.boolean.opBoolean","COPY",FACE,{"disambiguationData":[TD([makeQuery(id+"F4.opExtrude","SWEPT_FACE",FACE,{"disambiguationData":[OSD([sQuery(id+"F2.wireOp",EDGE,"E101")])]})])],"derivedFrom":makeQuery(id+"F8.opSweep","SWEPT_FACE",FACE,{"disambiguationData":[OSD([sQuery(id+"F0.wireOp",EDGE,"E0"),sQuery(id+"F7.wireOp",EDGE,"E620.5")])]})});
            var Q205;
            Q205=makeQuery(id+"F8.boolean.opBoolean","COPY",FACE,{"disambiguationData":[TD([makeQuery(id+"F4.opExtrude","SWEPT_FACE",FACE,{"disambiguationData":[OSD([sQuery(id+"F2.wireOp",EDGE,"E146")])]})])],"derivedFrom":makeQuery(id+"F8.opSweep","SWEPT_FACE",FACE,{"disambiguationData":[OSD([sQuery(id+"F0.wireOp",EDGE,"E0"),sQuery(id+"F7.wireOp",EDGE,"E620.5")])]})});
            var Q206;
            Q206=makeQuery(id+"F8.boolean.opBoolean","COPY",FACE,{"disambiguationData":[TD([makeQuery(id+"F4.opExtrude","SWEPT_FACE",FACE,{"disambiguationData":[OSD([sQuery(id+"F2.wireOp",EDGE,"E102")])]})])],"derivedFrom":makeQuery(id+"F8.opSweep","SWEPT_FACE",FACE,{"disambiguationData":[OSD([sQuery(id+"F0.wireOp",EDGE,"E0"),sQuery(id+"F7.wireOp",EDGE,"E620.5")])]})});
            var Q207;
            Q207=makeQuery(id+"F8.boolean.opBoolean","COPY",FACE,{"disambiguationData":[TD([makeQuery(id+"F4.opExtrude","SWEPT_FACE",FACE,{"disambiguationData":[OSD([sQuery(id+"F2.wireOp",EDGE,"E147")])]})])],"derivedFrom":makeQuery(id+"F8.opSweep","SWEPT_FACE",FACE,{"disambiguationData":[OSD([sQuery(id+"F0.wireOp",EDGE,"E0"),sQuery(id+"F7.wireOp",EDGE,"E620.5")])]})});
            var Q208;
            Q208=makeQuery(id+"F8.boolean.opBoolean","COPY",FACE,{"disambiguationData":[TD([makeQuery(id+"F4.opExtrude","SWEPT_FACE",FACE,{"disambiguationData":[OSD([sQuery(id+"F2.wireOp",EDGE,"E103")])]})])],"derivedFrom":makeQuery(id+"F8.opSweep","SWEPT_FACE",FACE,{"disambiguationData":[OSD([sQuery(id+"F0.wireOp",EDGE,"E0"),sQuery(id+"F7.wireOp",EDGE,"E620.5")])]})});
            var Q209;
            Q209=makeQuery(id+"F8.boolean.opBoolean","COPY",FACE,{"disambiguationData":[TD([makeQuery(id+"F4.opExtrude","SWEPT_FACE",FACE,{"disambiguationData":[OSD([sQuery(id+"F2.wireOp",EDGE,"E148")])]})])],"derivedFrom":makeQuery(id+"F8.opSweep","SWEPT_FACE",FACE,{"disambiguationData":[OSD([sQuery(id+"F0.wireOp",EDGE,"E0"),sQuery(id+"F7.wireOp",EDGE,"E620.5")])]})});
            var Q210;
            Q210=makeQuery(id+"F8.boolean.opBoolean","COPY",FACE,{"disambiguationData":[TD([makeQuery(id+"F4.opExtrude","SWEPT_FACE",FACE,{"disambiguationData":[OSD([sQuery(id+"F2.wireOp",EDGE,"E104")])]})])],"derivedFrom":makeQuery(id+"F8.opSweep","SWEPT_FACE",FACE,{"disambiguationData":[OSD([sQuery(id+"F0.wireOp",EDGE,"E0"),sQuery(id+"F7.wireOp",EDGE,"E620.5")])]})});
            var Q211;
            Q211=makeQuery(id+"F8.boolean.opBoolean","COPY",FACE,{"disambiguationData":[TD([makeQuery(id+"F4.opExtrude","SWEPT_FACE",FACE,{"disambiguationData":[OSD([sQuery(id+"F2.wireOp",EDGE,"E149")])]})])],"derivedFrom":makeQuery(id+"F8.opSweep","SWEPT_FACE",FACE,{"disambiguationData":[OSD([sQuery(id+"F0.wireOp",EDGE,"E0"),sQuery(id+"F7.wireOp",EDGE,"E620.5")])]})});
            var Q212;
            Q212=makeQuery(id+"F8.boolean.opBoolean","COPY",FACE,{"disambiguationData":[TD([makeQuery(id+"F4.opExtrude","SWEPT_FACE",FACE,{"disambiguationData":[OSD([sQuery(id+"F2.wireOp",EDGE,"E105")])]})])],"derivedFrom":makeQuery(id+"F8.opSweep","SWEPT_FACE",FACE,{"disambiguationData":[OSD([sQuery(id+"F0.wireOp",EDGE,"E0"),sQuery(id+"F7.wireOp",EDGE,"E620.5")])]})});
            var Q213;
            Q213=makeQuery(id+"F8.boolean.opBoolean","COPY",FACE,{"disambiguationData":[TD([makeQuery(id+"F4.opExtrude","SWEPT_FACE",FACE,{"disambiguationData":[OSD([sQuery(id+"F2.wireOp",EDGE,"E150")])]})])],"derivedFrom":makeQuery(id+"F8.opSweep","SWEPT_FACE",FACE,{"disambiguationData":[OSD([sQuery(id+"F0.wireOp",EDGE,"E0"),sQuery(id+"F7.wireOp",EDGE,"E620.5")])]})});
            var Q214;
            Q214=makeQuery(id+"F8.boolean.opBoolean","COPY",FACE,{"disambiguationData":[TD([makeQuery(id+"F4.opExtrude","SWEPT_FACE",FACE,{"disambiguationData":[OSD([sQuery(id+"F2.wireOp",EDGE,"E133")])]})])],"derivedFrom":makeQuery(id+"F8.opSweep","SWEPT_FACE",FACE,{"disambiguationData":[OSD([sQuery(id+"F0.wireOp",EDGE,"E0"),sQuery(id+"F7.wireOp",EDGE,"E620.4")])]})});
            var Q215;
            Q215=makeQuery(id+"F8.boolean.opBoolean","COPY",FACE,{"disambiguationData":[TD([makeQuery(id+"F4.opExtrude","SWEPT_FACE",FACE,{"disambiguationData":[OSD([sQuery(id+"F2.wireOp",EDGE,"E163")])]})])],"derivedFrom":makeQuery(id+"F8.opSweep","SWEPT_FACE",FACE,{"disambiguationData":[OSD([sQuery(id+"F0.wireOp",EDGE,"E0"),sQuery(id+"F7.wireOp",EDGE,"E620.4")])]})});
            var Q216;
            Q216=makeQuery(id+"F8.boolean.opBoolean","COPY",FACE,{"disambiguationData":[TD([makeQuery(id+"F4.opExtrude","SWEPT_FACE",FACE,{"disambiguationData":[OSD([sQuery(id+"F2.wireOp",EDGE,"E164")])]})])],"derivedFrom":makeQuery(id+"F8.opSweep","SWEPT_FACE",FACE,{"disambiguationData":[OSD([sQuery(id+"F0.wireOp",EDGE,"E0"),sQuery(id+"F7.wireOp",EDGE,"E620.4")])]})});
            var Q217;
            Q217=makeQuery(id+"F8.boolean.opBoolean","COPY",FACE,{"disambiguationData":[TD([makeQuery(id+"F4.opExtrude","SWEPT_FACE",FACE,{"disambiguationData":[OSD([sQuery(id+"F2.wireOp",EDGE,"E132")])]})])],"derivedFrom":makeQuery(id+"F8.opSweep","SWEPT_FACE",FACE,{"disambiguationData":[OSD([sQuery(id+"F0.wireOp",EDGE,"E0"),sQuery(id+"F7.wireOp",EDGE,"E620.4")])]})});
            var Q218;
            Q218=makeQuery(id+"F8.boolean.opBoolean","COPY",FACE,{"disambiguationData":[TD([makeQuery(id+"F4.opExtrude","SWEPT_FACE",FACE,{"disambiguationData":[OSD([sQuery(id+"F2.wireOp",EDGE,"E130")])]})])],"derivedFrom":makeQuery(id+"F8.opSweep","SWEPT_FACE",FACE,{"disambiguationData":[OSD([sQuery(id+"F0.wireOp",EDGE,"E0"),sQuery(id+"F7.wireOp",EDGE,"E620.4")])]})});
            var Q219;
            Q219=makeQuery(id+"F8.boolean.opBoolean","COPY",FACE,{"disambiguationData":[TD([makeQuery(id+"F4.opExtrude","SWEPT_FACE",FACE,{"disambiguationData":[OSD([sQuery(id+"F2.wireOp",EDGE,"E165")])]})])],"derivedFrom":makeQuery(id+"F8.opSweep","SWEPT_FACE",FACE,{"disambiguationData":[OSD([sQuery(id+"F0.wireOp",EDGE,"E0"),sQuery(id+"F7.wireOp",EDGE,"E620.4")])]})});
            var Q220;
            Q220=makeQuery(id+"F8.boolean.opBoolean","COPY",FACE,{"disambiguationData":[TD([makeQuery(id+"F4.opExtrude","SWEPT_FACE",FACE,{"disambiguationData":[OSD([sQuery(id+"F2.wireOp",EDGE,"E106")])]})])],"derivedFrom":makeQuery(id+"F8.opSweep","SWEPT_FACE",FACE,{"disambiguationData":[OSD([sQuery(id+"F0.wireOp",EDGE,"E0"),sQuery(id+"F7.wireOp",EDGE,"E620.5")])]})});
            var Q221;
            Q221=makeQuery(id+"F8.boolean.opBoolean","COPY",FACE,{"disambiguationData":[TD([makeQuery(id+"F4.opExtrude","SWEPT_FACE",FACE,{"disambiguationData":[OSD([sQuery(id+"F2.wireOp",EDGE,"E151")])]})])],"derivedFrom":makeQuery(id+"F8.opSweep","SWEPT_FACE",FACE,{"disambiguationData":[OSD([sQuery(id+"F0.wireOp",EDGE,"E0"),sQuery(id+"F7.wireOp",EDGE,"E620.5")])]})});
            var Q222;
            Q222=makeQuery(id+"F8.boolean.opBoolean","COPY",FACE,{"disambiguationData":[TD([makeQuery(id+"F4.opExtrude","SWEPT_FACE",FACE,{"disambiguationData":[OSD([sQuery(id+"F2.wireOp",EDGE,"E107")])]})])],"derivedFrom":makeQuery(id+"F8.opSweep","SWEPT_FACE",FACE,{"disambiguationData":[OSD([sQuery(id+"F0.wireOp",EDGE,"E0"),sQuery(id+"F7.wireOp",EDGE,"E620.5")])]})});
            var Q223;
            Q223=makeQuery(id+"F8.boolean.opBoolean","COPY",FACE,{"disambiguationData":[TD([makeQuery(id+"F4.opExtrude","SWEPT_FACE",FACE,{"disambiguationData":[OSD([sQuery(id+"F2.wireOp",EDGE,"E152")])]})])],"derivedFrom":makeQuery(id+"F8.opSweep","SWEPT_FACE",FACE,{"disambiguationData":[OSD([sQuery(id+"F0.wireOp",EDGE,"E0"),sQuery(id+"F7.wireOp",EDGE,"E620.5")])]})});
            var Q224;
            Q224=makeQuery(id+"F8.boolean.opBoolean","COPY",FACE,{"disambiguationData":[TD([makeQuery(id+"F4.opExtrude","SWEPT_FACE",FACE,{"disambiguationData":[OSD([sQuery(id+"F2.wireOp",EDGE,"E108")])]})])],"derivedFrom":makeQuery(id+"F8.opSweep","SWEPT_FACE",FACE,{"disambiguationData":[OSD([sQuery(id+"F0.wireOp",EDGE,"E0"),sQuery(id+"F7.wireOp",EDGE,"E620.5")])]})});
            var Q225;
            Q225=makeQuery(id+"F8.boolean.opBoolean","COPY",FACE,{"disambiguationData":[TD([makeQuery(id+"F4.opExtrude","SWEPT_FACE",FACE,{"disambiguationData":[OSD([sQuery(id+"F2.wireOp",EDGE,"E153")])]})])],"derivedFrom":makeQuery(id+"F8.opSweep","SWEPT_FACE",FACE,{"disambiguationData":[OSD([sQuery(id+"F0.wireOp",EDGE,"E0"),sQuery(id+"F7.wireOp",EDGE,"E620.5")])]})});
            var Q226;
            Q226=makeQuery(id+"F8.boolean.opBoolean","COPY",FACE,{"disambiguationData":[TD([makeQuery(id+"F4.opExtrude","SWEPT_FACE",FACE,{"disambiguationData":[OSD([sQuery(id+"F2.wireOp",EDGE,"E109")])]})])],"derivedFrom":makeQuery(id+"F8.opSweep","SWEPT_FACE",FACE,{"disambiguationData":[OSD([sQuery(id+"F0.wireOp",EDGE,"E0"),sQuery(id+"F7.wireOp",EDGE,"E620.5")])]})});
            var Q227;
            Q227=makeQuery(id+"F8.boolean.opBoolean","COPY",FACE,{"disambiguationData":[TD([makeQuery(id+"F4.opExtrude","SWEPT_FACE",FACE,{"disambiguationData":[OSD([sQuery(id+"F2.wireOp",EDGE,"E154")])]})])],"derivedFrom":makeQuery(id+"F8.opSweep","SWEPT_FACE",FACE,{"disambiguationData":[OSD([sQuery(id+"F0.wireOp",EDGE,"E0"),sQuery(id+"F7.wireOp",EDGE,"E620.5")])]})});
            var Q228;
            Q228=makeQuery(id+"F8.boolean.opBoolean","COPY",FACE,{"disambiguationData":[TD([makeQuery(id+"F4.opExtrude","SWEPT_FACE",FACE,{"disambiguationData":[OSD([sQuery(id+"F2.wireOp",EDGE,"E110")])]})])],"derivedFrom":makeQuery(id+"F8.opSweep","SWEPT_FACE",FACE,{"disambiguationData":[OSD([sQuery(id+"F0.wireOp",EDGE,"E0"),sQuery(id+"F7.wireOp",EDGE,"E620.5")])]})});
            var Q229;
            Q229=makeQuery(id+"F8.boolean.opBoolean","COPY",FACE,{"disambiguationData":[TD([makeQuery(id+"F4.opExtrude","SWEPT_FACE",FACE,{"disambiguationData":[OSD([sQuery(id+"F2.wireOp",EDGE,"E155")])]})])],"derivedFrom":makeQuery(id+"F8.opSweep","SWEPT_FACE",FACE,{"disambiguationData":[OSD([sQuery(id+"F0.wireOp",EDGE,"E0"),sQuery(id+"F7.wireOp",EDGE,"E620.5")])]})});
            var Q230;
            Q230=makeQuery(id+"F8.boolean.opBoolean","COPY",FACE,{"disambiguationData":[TD([makeQuery(id+"F4.opExtrude","SWEPT_FACE",FACE,{"disambiguationData":[OSD([sQuery(id+"F2.wireOp",EDGE,"E111")])]})])],"derivedFrom":makeQuery(id+"F8.opSweep","SWEPT_FACE",FACE,{"disambiguationData":[OSD([sQuery(id+"F0.wireOp",EDGE,"E0"),sQuery(id+"F7.wireOp",EDGE,"E620.5")])]})});
            var Q231;
            Q231=makeQuery(id+"F8.boolean.opBoolean","COPY",FACE,{"disambiguationData":[TD([makeQuery(id+"F4.opExtrude","SWEPT_FACE",FACE,{"disambiguationData":[OSD([sQuery(id+"F2.wireOp",EDGE,"E156")])]})])],"derivedFrom":makeQuery(id+"F8.opSweep","SWEPT_FACE",FACE,{"disambiguationData":[OSD([sQuery(id+"F0.wireOp",EDGE,"E0"),sQuery(id+"F7.wireOp",EDGE,"E620.5")])]})});
            var Q232;
            Q232=makeQuery(id+"F8.boolean.opBoolean","COPY",FACE,{"disambiguationData":[TD([makeQuery(id+"F4.opExtrude","SWEPT_FACE",FACE,{"disambiguationData":[OSD([sQuery(id+"F2.wireOp",EDGE,"E112")])]})])],"derivedFrom":makeQuery(id+"F8.opSweep","SWEPT_FACE",FACE,{"disambiguationData":[OSD([sQuery(id+"F0.wireOp",EDGE,"E0"),sQuery(id+"F7.wireOp",EDGE,"E620.5")])]})});
            var Q233;
            Q233=makeQuery(id+"F8.boolean.opBoolean","COPY",FACE,{"disambiguationData":[TD([makeQuery(id+"F4.opExtrude","SWEPT_FACE",FACE,{"disambiguationData":[OSD([sQuery(id+"F2.wireOp",EDGE,"E157")])]})])],"derivedFrom":makeQuery(id+"F8.opSweep","SWEPT_FACE",FACE,{"disambiguationData":[OSD([sQuery(id+"F0.wireOp",EDGE,"E0"),sQuery(id+"F7.wireOp",EDGE,"E620.5")])]})});
            var Q234;
            Q234=makeQuery(id+"F8.boolean.opBoolean","COPY",FACE,{"disambiguationData":[TD([makeQuery(id+"F4.opExtrude","SWEPT_FACE",FACE,{"disambiguationData":[OSD([sQuery(id+"F2.wireOp",EDGE,"E113")])]})])],"derivedFrom":makeQuery(id+"F8.opSweep","SWEPT_FACE",FACE,{"disambiguationData":[OSD([sQuery(id+"F0.wireOp",EDGE,"E0"),sQuery(id+"F7.wireOp",EDGE,"E620.5")])]})});
            var Q235;
            Q235=makeQuery(id+"F8.boolean.opBoolean","COPY",FACE,{"disambiguationData":[TD([makeQuery(id+"F4.opExtrude","SWEPT_FACE",FACE,{"disambiguationData":[OSD([sQuery(id+"F2.wireOp",EDGE,"E158")])]})])],"derivedFrom":makeQuery(id+"F8.opSweep","SWEPT_FACE",FACE,{"disambiguationData":[OSD([sQuery(id+"F0.wireOp",EDGE,"E0"),sQuery(id+"F7.wireOp",EDGE,"E620.5")])]})});
            var Q236;
            Q236=makeQuery(id+"F8.boolean.opBoolean","COPY",FACE,{"disambiguationData":[TD([makeQuery(id+"F4.opExtrude","SWEPT_FACE",FACE,{"disambiguationData":[OSD([sQuery(id+"F2.wireOp",EDGE,"E114")])]})])],"derivedFrom":makeQuery(id+"F8.opSweep","SWEPT_FACE",FACE,{"disambiguationData":[OSD([sQuery(id+"F0.wireOp",EDGE,"E0"),sQuery(id+"F7.wireOp",EDGE,"E620.5")])]})});
            var Q237;
            Q237=makeQuery(id+"F8.boolean.opBoolean","COPY",FACE,{"disambiguationData":[TD([makeQuery(id+"F4.opExtrude","SWEPT_FACE",FACE,{"disambiguationData":[OSD([sQuery(id+"F2.wireOp",EDGE,"E529.MirrorC")])]})])],"derivedFrom":makeQuery(id+"F8.opSweep","SWEPT_FACE",FACE,{"disambiguationData":[OSD([sQuery(id+"F0.wireOp",EDGE,"E0"),sQuery(id+"F7.wireOp",EDGE,"E620.5")])]})});
            var Q238;
            Q238=makeQuery(id+"F8.boolean.opBoolean","COPY",FACE,{"disambiguationData":[TD([makeQuery(id+"F4.opExtrude","SWEPT_FACE",FACE,{"disambiguationData":[OSD([sQuery(id+"F2.wireOp",EDGE,"E533.MirrorC")])]})])],"derivedFrom":makeQuery(id+"F8.opSweep","SWEPT_FACE",FACE,{"disambiguationData":[OSD([sQuery(id+"F0.wireOp",EDGE,"E0"),sQuery(id+"F7.wireOp",EDGE,"E620.5")])]})});
            var Q239;
            Q239=makeQuery(id+"F8.boolean.opBoolean","COPY",FACE,{"disambiguationData":[TD([makeQuery(id+"F4.opExtrude","SWEPT_FACE",FACE,{"disambiguationData":[OSD([sQuery(id+"F2.wireOp",EDGE,"E172")])]})])],"derivedFrom":makeQuery(id+"F8.opSweep","SWEPT_FACE",FACE,{"disambiguationData":[OSD([sQuery(id+"F0.wireOp",EDGE,"E0"),sQuery(id+"F7.wireOp",EDGE,"E620.4")])]})});
            var Q240;
            Q240=makeQuery(id+"F8.boolean.opBoolean","COPY",FACE,{"disambiguationData":[TD([makeQuery(id+"F4.opExtrude","SWEPT_FACE",FACE,{"disambiguationData":[OSD([sQuery(id+"F2.wireOp",EDGE,"E171")])]})])],"derivedFrom":makeQuery(id+"F8.opSweep","SWEPT_FACE",FACE,{"disambiguationData":[OSD([sQuery(id+"F0.wireOp",EDGE,"E0"),sQuery(id+"F7.wireOp",EDGE,"E620.4")])]})});
            var Q241;
            Q241=makeQuery(id+"F8.boolean.opBoolean","COPY",FACE,{"disambiguationData":[TD([makeQuery(id+"F4.opExtrude","SWEPT_FACE",FACE,{"disambiguationData":[OSD([sQuery(id+"F2.wireOp",EDGE,"E170")])]})])],"derivedFrom":makeQuery(id+"F8.opSweep","SWEPT_FACE",FACE,{"disambiguationData":[OSD([sQuery(id+"F0.wireOp",EDGE,"E0"),sQuery(id+"F7.wireOp",EDGE,"E620.4")])]})});
            var Q242;
            Q242=makeQuery(id+"F8.boolean.opBoolean","COPY",FACE,{"disambiguationData":[TD([makeQuery(id+"F4.opExtrude","SWEPT_FACE",FACE,{"disambiguationData":[OSD([sQuery(id+"F2.wireOp",EDGE,"E169")])]})])],"derivedFrom":makeQuery(id+"F8.opSweep","SWEPT_FACE",FACE,{"disambiguationData":[OSD([sQuery(id+"F0.wireOp",EDGE,"E0"),sQuery(id+"F7.wireOp",EDGE,"E620.4")])]})});
            var Q243;
            Q243=makeQuery(id+"F8.boolean.opBoolean","COPY",FACE,{"disambiguationData":[TD([makeQuery(id+"F4.opExtrude","SWEPT_FACE",FACE,{"disambiguationData":[OSD([sQuery(id+"F2.wireOp",EDGE,"E168")])]})])],"derivedFrom":makeQuery(id+"F8.opSweep","SWEPT_FACE",FACE,{"disambiguationData":[OSD([sQuery(id+"F0.wireOp",EDGE,"E0"),sQuery(id+"F7.wireOp",EDGE,"E620.4")])]})});
            var Q244;
            Q244=makeQuery(id+"F8.boolean.opBoolean","COPY",FACE,{"disambiguationData":[TD([makeQuery(id+"F4.opExtrude","SWEPT_FACE",FACE,{"disambiguationData":[OSD([sQuery(id+"F2.wireOp",EDGE,"E167")])]})])],"derivedFrom":makeQuery(id+"F8.opSweep","SWEPT_FACE",FACE,{"disambiguationData":[OSD([sQuery(id+"F0.wireOp",EDGE,"E0"),sQuery(id+"F7.wireOp",EDGE,"E620.4")])]})});
            var Q245;
            Q245=makeQuery(id+"F8.boolean.opBoolean","COPY",FACE,{"disambiguationData":[TD([makeQuery(id+"F4.opExtrude","SWEPT_FACE",FACE,{"disambiguationData":[OSD([sQuery(id+"F2.wireOp",EDGE,"E166")])]})])],"derivedFrom":makeQuery(id+"F8.opSweep","SWEPT_FACE",FACE,{"disambiguationData":[OSD([sQuery(id+"F0.wireOp",EDGE,"E0"),sQuery(id+"F7.wireOp",EDGE,"E620.4")])]})});
            var Q246;
            Q246=makeQuery(id+"F8.boolean.opBoolean","COPY",FACE,{"disambiguationData":[TD([makeQuery(id+"F4.opExtrude","SWEPT_FACE",FACE,{"disambiguationData":[OSD([sQuery(id+"F2.wireOp",EDGE,"E128")])]})])],"derivedFrom":makeQuery(id+"F8.opSweep","SWEPT_FACE",FACE,{"disambiguationData":[OSD([sQuery(id+"F0.wireOp",EDGE,"E0"),sQuery(id+"F7.wireOp",EDGE,"E620.4")])]})});
            var Q247;
            Q247=makeQuery(id+"F8.boolean.opBoolean","COPY",FACE,{"disambiguationData":[TD([makeQuery(id+"F4.opExtrude","SWEPT_FACE",FACE,{"disambiguationData":[OSD([sQuery(id+"F2.wireOp",EDGE,"E126")])]})])],"derivedFrom":makeQuery(id+"F8.opSweep","SWEPT_FACE",FACE,{"disambiguationData":[OSD([sQuery(id+"F0.wireOp",EDGE,"E0"),sQuery(id+"F7.wireOp",EDGE,"E620.4")])]})});
            var Q248;
            Q248=makeQuery(id+"F8.boolean.opBoolean","COPY",FACE,{"disambiguationData":[TD([makeQuery(id+"F4.opExtrude","SWEPT_FACE",FACE,{"disambiguationData":[OSD([sQuery(id+"F2.wireOp",EDGE,"E124")])]})])],"derivedFrom":makeQuery(id+"F8.opSweep","SWEPT_FACE",FACE,{"disambiguationData":[OSD([sQuery(id+"F0.wireOp",EDGE,"E0"),sQuery(id+"F7.wireOp",EDGE,"E620.4")])]})});
            var Q249;
            Q249=makeQuery(id+"F8.boolean.opBoolean","COPY",FACE,{"disambiguationData":[TD([makeQuery(id+"F4.opExtrude","SWEPT_FACE",FACE,{"disambiguationData":[OSD([sQuery(id+"F2.wireOp",EDGE,"E122")])]})])],"derivedFrom":makeQuery(id+"F8.opSweep","SWEPT_FACE",FACE,{"disambiguationData":[OSD([sQuery(id+"F0.wireOp",EDGE,"E0"),sQuery(id+"F7.wireOp",EDGE,"E620.4")])]})});
            var Q250;
            Q250=makeQuery(id+"F8.boolean.opBoolean","COPY",FACE,{"disambiguationData":[TD([makeQuery(id+"F4.opExtrude","SWEPT_FACE",FACE,{"disambiguationData":[OSD([sQuery(id+"F2.wireOp",EDGE,"E119")])]})])],"derivedFrom":makeQuery(id+"F8.opSweep","SWEPT_FACE",FACE,{"disambiguationData":[OSD([sQuery(id+"F0.wireOp",EDGE,"E0"),sQuery(id+"F7.wireOp",EDGE,"E620.4")])]})});
            var Q251;
            Q251=makeQuery(id+"F8.boolean.opBoolean","COPY",FACE,{"disambiguationData":[TD([makeQuery(id+"F4.opExtrude","SWEPT_FACE",FACE,{"disambiguationData":[OSD([sQuery(id+"F2.wireOp",EDGE,"E118")])]})])],"derivedFrom":makeQuery(id+"F8.opSweep","SWEPT_FACE",FACE,{"disambiguationData":[OSD([sQuery(id+"F0.wireOp",EDGE,"E0"),sQuery(id+"F7.wireOp",EDGE,"E620.4")])]})});
            var Q252;
            Q252=makeQuery(id+"F8.boolean.opBoolean","COPY",FACE,{"disambiguationData":[TD([makeQuery(id+"F4.opExtrude","SWEPT_FACE",FACE,{"disambiguationData":[OSD([sQuery(id+"F2.wireOp",EDGE,"E116")])]})])],"derivedFrom":makeQuery(id+"F8.opSweep","SWEPT_FACE",FACE,{"disambiguationData":[OSD([sQuery(id+"F0.wireOp",EDGE,"E0"),sQuery(id+"F7.wireOp",EDGE,"E620.4")])]})});
            var Q253;
            Q253=makeQuery(id+"F8.boolean.opBoolean","COPY",FACE,{"disambiguationData":[TD([makeQuery(id+"F4.opExtrude","SWEPT_FACE",FACE,{"disambiguationData":[OSD([sQuery(id+"F2.wireOp",EDGE,"E338.MirrorC")])]})])],"derivedFrom":makeQuery(id+"F8.opSweep","SWEPT_FACE",FACE,{"disambiguationData":[OSD([sQuery(id+"F0.wireOp",EDGE,"E0"),sQuery(id+"F7.wireOp",EDGE,"E620.4")])]})});
            var Q254;
            Q254=makeQuery(id+"F8.boolean.opBoolean","COPY",FACE,{"disambiguationData":[TD([makeQuery(id+"F4.opExtrude","SWEPT_FACE",FACE,{"disambiguationData":[OSD([sQuery(id+"F2.wireOp",EDGE,"E170")])]})])],"derivedFrom":makeQuery(id+"F8.opSweep","SWEPT_FACE",FACE,{"disambiguationData":[OSD([sQuery(id+"F0.wireOp",EDGE,"E0"),sQuery(id+"F7.wireOp",EDGE,"E620.4")])]})});
            var Q255;
            Q255=makeQuery(id+"F8.boolean.opBoolean","COPY",FACE,{"disambiguationData":[TD([makeQuery(id+"F4.opExtrude","SWEPT_FACE",FACE,{"disambiguationData":[OSD([sQuery(id+"F2.wireOp",EDGE,"E391.MirrorC")])]})])],"derivedFrom":makeQuery(id+"F8.opSweep","SWEPT_FACE",FACE,{"disambiguationData":[OSD([sQuery(id+"F0.wireOp",EDGE,"E0"),sQuery(id+"F7.wireOp",EDGE,"E620.4")])]})});
            var Q256;
            Q256=makeQuery(id+"F8.boolean.opBoolean","COPY",FACE,{"disambiguationData":[TD([makeQuery(id+"F4.opExtrude","SWEPT_FACE",FACE,{"disambiguationData":[OSD([sQuery(id+"F2.wireOp",EDGE,"E372.MirrorC")])]})])],"derivedFrom":makeQuery(id+"F8.opSweep","SWEPT_FACE",FACE,{"disambiguationData":[OSD([sQuery(id+"F0.wireOp",EDGE,"E0"),sQuery(id+"F7.wireOp",EDGE,"E620.4")])]})});
            var Q257;
            Q257=makeQuery(id+"F8.boolean.opBoolean","COPY",FACE,{"disambiguationData":[TD([makeQuery(id+"F4.opExtrude","SWEPT_FACE",FACE,{"disambiguationData":[OSD([sQuery(id+"F2.wireOp",EDGE,"E333.MirrorC")])]})])],"derivedFrom":makeQuery(id+"F8.opSweep","SWEPT_FACE",FACE,{"disambiguationData":[OSD([sQuery(id+"F0.wireOp",EDGE,"E0"),sQuery(id+"F7.wireOp",EDGE,"E620.4")])]})});
            var Q258;
            Q258=makeQuery(id+"F8.boolean.opBoolean","COPY",FACE,{"disambiguationData":[TD([makeQuery(id+"F4.opExtrude","SWEPT_FACE",FACE,{"disambiguationData":[OSD([sQuery(id+"F2.wireOp",EDGE,"E422.MirrorC")])]})])],"derivedFrom":makeQuery(id+"F8.opSweep","SWEPT_FACE",FACE,{"disambiguationData":[OSD([sQuery(id+"F0.wireOp",EDGE,"E0"),sQuery(id+"F7.wireOp",EDGE,"E620.4")])]})});
            var Q259;
            Q259=makeQuery(id+"F8.boolean.opBoolean","COPY",FACE,{"disambiguationData":[TD([makeQuery(id+"F4.opExtrude","SWEPT_FACE",FACE,{"disambiguationData":[OSD([sQuery(id+"F2.wireOp",EDGE,"E439.MirrorC")])]})])],"derivedFrom":makeQuery(id+"F8.opSweep","SWEPT_FACE",FACE,{"disambiguationData":[OSD([sQuery(id+"F0.wireOp",EDGE,"E0"),sQuery(id+"F7.wireOp",EDGE,"E620.4")])]})});
            var Q260;
            Q260=makeQuery(id+"F8.boolean.opBoolean","COPY",FACE,{"disambiguationData":[TD([makeQuery(id+"F4.opExtrude","SWEPT_FACE",FACE,{"disambiguationData":[OSD([sQuery(id+"F2.wireOp",EDGE,"E379.MirrorC")])]})])],"derivedFrom":makeQuery(id+"F8.opSweep","SWEPT_FACE",FACE,{"disambiguationData":[OSD([sQuery(id+"F0.wireOp",EDGE,"E0"),sQuery(id+"F7.wireOp",EDGE,"E620.4")])]})});
            var Q261;
            Q261=makeQuery(id+"F8.boolean.opBoolean","COPY",FACE,{"disambiguationData":[TD([makeQuery(id+"F4.opExtrude","SWEPT_FACE",FACE,{"disambiguationData":[OSD([sQuery(id+"F2.wireOp",EDGE,"E387.MirrorC")])]})])],"derivedFrom":makeQuery(id+"F8.opSweep","SWEPT_FACE",FACE,{"disambiguationData":[OSD([sQuery(id+"F0.wireOp",EDGE,"E0"),sQuery(id+"F7.wireOp",EDGE,"E620.4")])]})});
            var Q262;
            Q262=makeQuery(id+"F8.boolean.opBoolean","COPY",FACE,{"disambiguationData":[TD([makeQuery(id+"F4.opExtrude","SWEPT_FACE",FACE,{"disambiguationData":[OSD([sQuery(id+"F2.wireOp",EDGE,"E363.MirrorC")])]})])],"derivedFrom":makeQuery(id+"F8.opSweep","SWEPT_FACE",FACE,{"disambiguationData":[OSD([sQuery(id+"F0.wireOp",EDGE,"E0"),sQuery(id+"F7.wireOp",EDGE,"E620.4")])]})});
            var Q263;
            Q263=makeQuery(id+"F8.boolean.opBoolean","COPY",FACE,{"disambiguationData":[TD([makeQuery(id+"F4.opExtrude","SWEPT_FACE",FACE,{"disambiguationData":[OSD([sQuery(id+"F2.wireOp",EDGE,"E361.MirrorC")])]})])],"derivedFrom":makeQuery(id+"F8.opSweep","SWEPT_FACE",FACE,{"disambiguationData":[OSD([sQuery(id+"F0.wireOp",EDGE,"E0"),sQuery(id+"F7.wireOp",EDGE,"E620.4")])]})});
            var Q264;
            Q264=makeQuery(id+"F8.boolean.opBoolean","COPY",FACE,{"disambiguationData":[TD([makeQuery(id+"F4.opExtrude","SWEPT_FACE",FACE,{"disambiguationData":[OSD([sQuery(id+"F2.wireOp",EDGE,"E331.MirrorC")])]})])],"derivedFrom":makeQuery(id+"F8.opSweep","SWEPT_FACE",FACE,{"disambiguationData":[OSD([sQuery(id+"F0.wireOp",EDGE,"E0"),sQuery(id+"F7.wireOp",EDGE,"E620.4")])]})});
            var Q265;
            Q265=makeQuery(id+"F8.boolean.opBoolean","COPY",FACE,{"disambiguationData":[TD([makeQuery(id+"F4.opExtrude","SWEPT_FACE",FACE,{"disambiguationData":[OSD([sQuery(id+"F2.wireOp",EDGE,"E356.MirrorC")])]})])],"derivedFrom":makeQuery(id+"F8.opSweep","SWEPT_FACE",FACE,{"disambiguationData":[OSD([sQuery(id+"F0.wireOp",EDGE,"E0"),sQuery(id+"F7.wireOp",EDGE,"E620.4")])]})});
            var Q266;
            Q266=makeQuery(id+"F8.boolean.opBoolean","COPY",FACE,{"disambiguationData":[TD([makeQuery(id+"F4.opExtrude","SWEPT_FACE",FACE,{"disambiguationData":[OSD([sQuery(id+"F2.wireOp",EDGE,"E336.MirrorC")])]})])],"derivedFrom":makeQuery(id+"F8.opSweep","SWEPT_FACE",FACE,{"disambiguationData":[OSD([sQuery(id+"F0.wireOp",EDGE,"E0"),sQuery(id+"F7.wireOp",EDGE,"E620.4")])]})});
            var Q267;
            Q267=makeQuery(id+"F8.boolean.opBoolean","COPY",FACE,{"disambiguationData":[TD([makeQuery(id+"F4.opExtrude","SWEPT_FACE",FACE,{"disambiguationData":[OSD([sQuery(id+"F2.wireOp",EDGE,"E421.MirrorC")])]})])],"derivedFrom":makeQuery(id+"F8.opSweep","SWEPT_FACE",FACE,{"disambiguationData":[OSD([sQuery(id+"F0.wireOp",EDGE,"E0"),sQuery(id+"F7.wireOp",EDGE,"E620.4")])]})});
            var Q268;
            Q268=makeQuery(id+"F8.boolean.opBoolean","COPY",FACE,{"disambiguationData":[TD([makeQuery(id+"F4.opExtrude","SWEPT_FACE",FACE,{"disambiguationData":[OSD([sQuery(id+"F2.wireOp",EDGE,"E345.MirrorC")])]})])],"derivedFrom":makeQuery(id+"F8.opSweep","SWEPT_FACE",FACE,{"disambiguationData":[OSD([sQuery(id+"F0.wireOp",EDGE,"E0"),sQuery(id+"F7.wireOp",EDGE,"E620.4")])]})});
            var Q269;
            Q269=makeQuery(id+"F8.boolean.opBoolean","COPY",FACE,{"disambiguationData":[TD([makeQuery(id+"F4.opExtrude","SWEPT_FACE",FACE,{"disambiguationData":[OSD([sQuery(id+"F2.wireOp",EDGE,"E354.MirrorC")])]})])],"derivedFrom":makeQuery(id+"F8.opSweep","SWEPT_FACE",FACE,{"disambiguationData":[OSD([sQuery(id+"F0.wireOp",EDGE,"E0"),sQuery(id+"F7.wireOp",EDGE,"E620.4")])]})});
            var Q270;
            Q270=makeQuery(id+"F8.boolean.opBoolean","COPY",FACE,{"disambiguationData":[TD([makeQuery(id+"F4.opExtrude","SWEPT_FACE",FACE,{"disambiguationData":[OSD([sQuery(id+"F2.wireOp",EDGE,"E359.MirrorC")])]})])],"derivedFrom":makeQuery(id+"F8.opSweep","SWEPT_FACE",FACE,{"disambiguationData":[OSD([sQuery(id+"F0.wireOp",EDGE,"E0"),sQuery(id+"F7.wireOp",EDGE,"E620.4")])]})});
            var Q271;
            Q271=makeQuery(id+"F8.boolean.opBoolean","COPY",FACE,{"disambiguationData":[TD([makeQuery(id+"F4.opExtrude","SWEPT_FACE",FACE,{"disambiguationData":[OSD([sQuery(id+"F2.wireOp",EDGE,"E402.MirrorC")])]})])],"derivedFrom":makeQuery(id+"F8.opSweep","SWEPT_FACE",FACE,{"disambiguationData":[OSD([sQuery(id+"F0.wireOp",EDGE,"E0"),sQuery(id+"F7.wireOp",EDGE,"E620.4")])]})});
            var Q272;
            Q272=makeQuery(id+"F8.boolean.opBoolean","COPY",FACE,{"disambiguationData":[TD([makeQuery(id+"F4.opExtrude","SWEPT_FACE",FACE,{"disambiguationData":[OSD([sQuery(id+"F2.wireOp",EDGE,"E344.MirrorC")])]})])],"derivedFrom":makeQuery(id+"F8.opSweep","SWEPT_FACE",FACE,{"disambiguationData":[OSD([sQuery(id+"F0.wireOp",EDGE,"E0"),sQuery(id+"F7.wireOp",EDGE,"E620.4")])]})});
            var Q273;
            Q273=makeQuery(id+"F8.boolean.opBoolean","COPY",FACE,{"disambiguationData":[TD([makeQuery(id+"F4.opExtrude","SWEPT_FACE",FACE,{"disambiguationData":[OSD([sQuery(id+"F2.wireOp",EDGE,"E510.MirrorC")])]})])],"derivedFrom":makeQuery(id+"F8.opSweep","SWEPT_FACE",FACE,{"disambiguationData":[OSD([sQuery(id+"F0.wireOp",EDGE,"E0"),sQuery(id+"F7.wireOp",EDGE,"E620.5")])]})});
            var Q274;
            Q274=makeQuery(id+"F8.boolean.opBoolean","COPY",FACE,{"disambiguationData":[TD([makeQuery(id+"F4.opExtrude","SWEPT_FACE",FACE,{"disambiguationData":[OSD([sQuery(id+"F2.wireOp",EDGE,"E497.MirrorC")])]})])],"derivedFrom":makeQuery(id+"F8.opSweep","SWEPT_FACE",FACE,{"disambiguationData":[OSD([sQuery(id+"F0.wireOp",EDGE,"E0"),sQuery(id+"F7.wireOp",EDGE,"E620.5")])]})});
            var Q275;
            Q275=makeQuery(id+"F8.boolean.opBoolean","COPY",FACE,{"disambiguationData":[TD([makeQuery(id+"F4.opExtrude","SWEPT_FACE",FACE,{"disambiguationData":[OSD([sQuery(id+"F2.wireOp",EDGE,"E492.MirrorC")])]})])],"derivedFrom":makeQuery(id+"F8.opSweep","SWEPT_FACE",FACE,{"disambiguationData":[OSD([sQuery(id+"F0.wireOp",EDGE,"E0"),sQuery(id+"F7.wireOp",EDGE,"E620.5")])]})});
            var Q276;
            Q276=makeQuery(id+"F8.boolean.opBoolean","COPY",FACE,{"disambiguationData":[TD([makeQuery(id+"F4.opExtrude","SWEPT_FACE",FACE,{"disambiguationData":[OSD([sQuery(id+"F2.wireOp",EDGE,"E551.MirrorC")])]})])],"derivedFrom":makeQuery(id+"F8.opSweep","SWEPT_FACE",FACE,{"disambiguationData":[OSD([sQuery(id+"F0.wireOp",EDGE,"E0"),sQuery(id+"F7.wireOp",EDGE,"E620.5")])]})});
            var Q277;
            Q277=makeQuery(id+"F8.boolean.opBoolean","COPY",FACE,{"disambiguationData":[TD([makeQuery(id+"F4.opExtrude","SWEPT_FACE",FACE,{"disambiguationData":[OSD([sQuery(id+"F2.wireOp",EDGE,"E543.MirrorC")])]})])],"derivedFrom":makeQuery(id+"F8.opSweep","SWEPT_FACE",FACE,{"disambiguationData":[OSD([sQuery(id+"F0.wireOp",EDGE,"E0"),sQuery(id+"F7.wireOp",EDGE,"E620.5")])]})});
            var Q278;
            Q278=makeQuery(id+"F8.boolean.opBoolean","COPY",FACE,{"disambiguationData":[TD([makeQuery(id+"F4.opExtrude","SWEPT_FACE",FACE,{"disambiguationData":[OSD([sQuery(id+"F2.wireOp",EDGE,"E514.MirrorC")])]})])],"derivedFrom":makeQuery(id+"F8.opSweep","SWEPT_FACE",FACE,{"disambiguationData":[OSD([sQuery(id+"F0.wireOp",EDGE,"E0"),sQuery(id+"F7.wireOp",EDGE,"E620.5")])]})});
            var Q279;
            Q279=makeQuery(id+"F8.boolean.opBoolean","COPY",FACE,{"disambiguationData":[TD([makeQuery(id+"F4.opExtrude","SWEPT_FACE",FACE,{"disambiguationData":[OSD([sQuery(id+"F2.wireOp",EDGE,"E480.MirrorC")])]})])],"derivedFrom":makeQuery(id+"F8.opSweep","SWEPT_FACE",FACE,{"disambiguationData":[OSD([sQuery(id+"F0.wireOp",EDGE,"E0"),sQuery(id+"F7.wireOp",EDGE,"E620.5")])]})});
            var Q280;
            Q280=makeQuery(id+"F8.boolean.opBoolean","COPY",FACE,{"disambiguationData":[TD([makeQuery(id+"F4.opExtrude","SWEPT_FACE",FACE,{"disambiguationData":[OSD([sQuery(id+"F2.wireOp",EDGE,"E539.MirrorC")])]})])],"derivedFrom":makeQuery(id+"F8.opSweep","SWEPT_FACE",FACE,{"disambiguationData":[OSD([sQuery(id+"F0.wireOp",EDGE,"E0"),sQuery(id+"F7.wireOp",EDGE,"E620.5")])]})});
            var Q281;
            Q281=makeQuery(id+"F8.boolean.opBoolean","COPY",FACE,{"disambiguationData":[TD([makeQuery(id+"F4.opExtrude","SWEPT_FACE",FACE,{"disambiguationData":[OSD([sQuery(id+"F2.wireOp",EDGE,"E504.MirrorC")])]})])],"derivedFrom":makeQuery(id+"F8.opSweep","SWEPT_FACE",FACE,{"disambiguationData":[OSD([sQuery(id+"F0.wireOp",EDGE,"E0"),sQuery(id+"F7.wireOp",EDGE,"E620.5")])]})});
            var Q282;
            Q282=makeQuery(id+"F8.boolean.opBoolean","COPY",FACE,{"disambiguationData":[TD([makeQuery(id+"F4.opExtrude","SWEPT_FACE",FACE,{"disambiguationData":[OSD([sQuery(id+"F2.wireOp",EDGE,"E483.MirrorC")])]})])],"derivedFrom":makeQuery(id+"F8.opSweep","SWEPT_FACE",FACE,{"disambiguationData":[OSD([sQuery(id+"F0.wireOp",EDGE,"E0"),sQuery(id+"F7.wireOp",EDGE,"E620.5")])]})});
            var Q283;
            Q283=makeQuery(id+"F8.boolean.opBoolean","COPY",FACE,{"disambiguationData":[TD([makeQuery(id+"F4.opExtrude","SWEPT_FACE",FACE,{"disambiguationData":[OSD([sQuery(id+"F2.wireOp",EDGE,"E554.MirrorC")])]})])],"derivedFrom":makeQuery(id+"F8.opSweep","SWEPT_FACE",FACE,{"disambiguationData":[OSD([sQuery(id+"F0.wireOp",EDGE,"E0"),sQuery(id+"F7.wireOp",EDGE,"E620.5")])]})});
            var Q284;
            Q284=makeQuery(id+"F8.boolean.opBoolean","COPY",FACE,{"disambiguationData":[TD([makeQuery(id+"F4.opExtrude","SWEPT_FACE",FACE,{"disambiguationData":[OSD([sQuery(id+"F2.wireOp",EDGE,"E445.MirrorC")])]})])],"derivedFrom":makeQuery(id+"F8.opSweep","SWEPT_FACE",FACE,{"disambiguationData":[OSD([sQuery(id+"F0.wireOp",EDGE,"E0"),sQuery(id+"F7.wireOp",EDGE,"E620.5")])]})});
            var Q285;
            Q285=makeQuery(id+"F8.boolean.opBoolean","COPY",FACE,{"disambiguationData":[TD([makeQuery(id+"F4.opExtrude","SWEPT_FACE",FACE,{"disambiguationData":[OSD([sQuery(id+"F2.wireOp",EDGE,"E478.MirrorC")])]})])],"derivedFrom":makeQuery(id+"F8.opSweep","SWEPT_FACE",FACE,{"disambiguationData":[OSD([sQuery(id+"F0.wireOp",EDGE,"E0"),sQuery(id+"F7.wireOp",EDGE,"E620.5")])]})});
            var Q286;
            Q286=makeQuery(id+"F8.boolean.opBoolean","COPY",FACE,{"disambiguationData":[TD([makeQuery(id+"F4.opExtrude","SWEPT_FACE",FACE,{"disambiguationData":[OSD([sQuery(id+"F2.wireOp",EDGE,"E547.MirrorC")])]})])],"derivedFrom":makeQuery(id+"F8.opSweep","SWEPT_FACE",FACE,{"disambiguationData":[OSD([sQuery(id+"F0.wireOp",EDGE,"E0"),sQuery(id+"F7.wireOp",EDGE,"E620.5")])]})});
            var Q287;
            Q287=makeQuery(id+"F8.boolean.opBoolean","COPY",FACE,{"disambiguationData":[TD([makeQuery(id+"F4.opExtrude","SWEPT_FACE",FACE,{"disambiguationData":[OSD([sQuery(id+"F2.wireOp",EDGE,"E452.MirrorC")])]})])],"derivedFrom":makeQuery(id+"F8.opSweep","SWEPT_FACE",FACE,{"disambiguationData":[OSD([sQuery(id+"F0.wireOp",EDGE,"E0"),sQuery(id+"F7.wireOp",EDGE,"E620.5")])]})});
            var Q288;
            Q288=makeQuery(id+"F8.boolean.opBoolean","COPY",FACE,{"disambiguationData":[TD([makeQuery(id+"F4.opExtrude","SWEPT_FACE",FACE,{"disambiguationData":[OSD([sQuery(id+"F2.wireOp",EDGE,"E489.MirrorC")])]})])],"derivedFrom":makeQuery(id+"F8.opSweep","SWEPT_FACE",FACE,{"disambiguationData":[OSD([sQuery(id+"F0.wireOp",EDGE,"E0"),sQuery(id+"F7.wireOp",EDGE,"E620.5")])]})});
            var Q289;
            Q289=makeQuery(id+"F8.boolean.opBoolean","COPY",FACE,{"disambiguationData":[TD([makeQuery(id+"F4.opExtrude","SWEPT_FACE",FACE,{"disambiguationData":[OSD([sQuery(id+"F2.wireOp",EDGE,"E463.MirrorC")])]})])],"derivedFrom":makeQuery(id+"F8.opSweep","SWEPT_FACE",FACE,{"disambiguationData":[OSD([sQuery(id+"F0.wireOp",EDGE,"E0"),sQuery(id+"F7.wireOp",EDGE,"E620.5")])]})});
            var Q290;
            Q290=makeQuery(id+"F8.boolean.opBoolean","COPY",FACE,{"disambiguationData":[TD([makeQuery(id+"F4.opExtrude","SWEPT_FACE",FACE,{"disambiguationData":[OSD([sQuery(id+"F2.wireOp",EDGE,"E513.MirrorC")])]})])],"derivedFrom":makeQuery(id+"F8.opSweep","SWEPT_FACE",FACE,{"disambiguationData":[OSD([sQuery(id+"F0.wireOp",EDGE,"E0"),sQuery(id+"F7.wireOp",EDGE,"E620.5")])]})});
            var Q291;
            Q291=makeQuery(id+"F8.boolean.opBoolean","COPY",FACE,{"disambiguationData":[TD([makeQuery(id+"F4.opExtrude","SWEPT_FACE",FACE,{"disambiguationData":[OSD([sQuery(id+"F2.wireOp",EDGE,"E470.MirrorC")])]})])],"derivedFrom":makeQuery(id+"F8.opSweep","SWEPT_FACE",FACE,{"disambiguationData":[OSD([sQuery(id+"F0.wireOp",EDGE,"E0"),sQuery(id+"F7.wireOp",EDGE,"E620.5")])]})});
            var Q292;
            Q292=makeQuery(id+"F8.boolean.opBoolean","COPY",FACE,{"disambiguationData":[TD([makeQuery(id+"F4.opExtrude","SWEPT_FACE",FACE,{"disambiguationData":[OSD([sQuery(id+"F2.wireOp",EDGE,"E447.MirrorC")])]})])],"derivedFrom":makeQuery(id+"F8.opSweep","SWEPT_FACE",FACE,{"disambiguationData":[OSD([sQuery(id+"F0.wireOp",EDGE,"E0"),sQuery(id+"F7.wireOp",EDGE,"E620.5")])]})});
            var Q293;
            Q293=makeQuery(id+"F8.boolean.opBoolean","COPY",FACE,{"disambiguationData":[TD([makeQuery(id+"F4.opExtrude","SWEPT_FACE",FACE,{"disambiguationData":[OSD([sQuery(id+"F2.wireOp",EDGE,"E507.MirrorC")])]})])],"derivedFrom":makeQuery(id+"F8.opSweep","SWEPT_FACE",FACE,{"disambiguationData":[OSD([sQuery(id+"F0.wireOp",EDGE,"E0"),sQuery(id+"F7.wireOp",EDGE,"E620.5")])]})});
            var Q294;
            Q294=makeQuery(id+"F8.boolean.opBoolean","COPY",FACE,{"disambiguationData":[TD([makeQuery(id+"F4.opExtrude","SWEPT_FACE",FACE,{"disambiguationData":[OSD([sQuery(id+"F2.wireOp",EDGE,"E455.MirrorC")])]})])],"derivedFrom":makeQuery(id+"F8.opSweep","SWEPT_FACE",FACE,{"disambiguationData":[OSD([sQuery(id+"F0.wireOp",EDGE,"E0"),sQuery(id+"F7.wireOp",EDGE,"E620.5")])]})});
            var Q295;
            Q295=makeQuery(id+"F8.boolean.opBoolean","COPY",FACE,{"disambiguationData":[TD([makeQuery(id+"F4.opExtrude","SWEPT_FACE",FACE,{"disambiguationData":[OSD([sQuery(id+"F2.wireOp",EDGE,"E538.MirrorC")])]})])],"derivedFrom":makeQuery(id+"F8.opSweep","SWEPT_FACE",FACE,{"disambiguationData":[OSD([sQuery(id+"F0.wireOp",EDGE,"E0"),sQuery(id+"F7.wireOp",EDGE,"E620.5")])]})});
            var Q296;
            Q296=makeQuery(id+"F8.boolean.opBoolean","COPY",FACE,{"disambiguationData":[TD([makeQuery(id+"F4.opExtrude","SWEPT_FACE",FACE,{"disambiguationData":[OSD([sQuery(id+"F2.wireOp",EDGE,"E465.MirrorC")])]})])],"derivedFrom":makeQuery(id+"F8.opSweep","SWEPT_FACE",FACE,{"disambiguationData":[OSD([sQuery(id+"F0.wireOp",EDGE,"E0"),sQuery(id+"F7.wireOp",EDGE,"E620.5")])]})});
            var Q297;
            Q297=makeQuery(id+"F8.boolean.opBoolean","COPY",FACE,{"disambiguationData":[TD([makeQuery(id+"F4.opExtrude","SWEPT_FACE",FACE,{"disambiguationData":[OSD([sQuery(id+"F2.wireOp",EDGE,"E376.MirrorC")])]})])],"derivedFrom":makeQuery(id+"F8.opSweep","SWEPT_FACE",FACE,{"disambiguationData":[OSD([sQuery(id+"F0.wireOp",EDGE,"E0"),sQuery(id+"F7.wireOp",EDGE,"E620.4")])]})});
            var Q298;
            Q298=makeQuery(id+"F8.boolean.opBoolean","COPY",FACE,{"disambiguationData":[TD([makeQuery(id+"F4.opExtrude","SWEPT_FACE",FACE,{"disambiguationData":[OSD([sQuery(id+"F2.wireOp",EDGE,"E416.MirrorC")])]})])],"derivedFrom":makeQuery(id+"F8.opSweep","SWEPT_FACE",FACE,{"disambiguationData":[OSD([sQuery(id+"F0.wireOp",EDGE,"E0"),sQuery(id+"F7.wireOp",EDGE,"E620.4")])]})});
            var Q299;
            Q299=makeQuery(id+"F8.boolean.opBoolean","COPY",FACE,{"disambiguationData":[TD([makeQuery(id+"F4.opExtrude","SWEPT_FACE",FACE,{"disambiguationData":[OSD([sQuery(id+"F2.wireOp",EDGE,"E423.MirrorC")])]})])],"derivedFrom":makeQuery(id+"F8.opSweep","SWEPT_FACE",FACE,{"disambiguationData":[OSD([sQuery(id+"F0.wireOp",EDGE,"E0"),sQuery(id+"F7.wireOp",EDGE,"E620.4")])]})});
            var Q300;
            Q300=makeQuery(id+"F8.boolean.opBoolean","COPY",FACE,{"disambiguationData":[TD([makeQuery(id+"F4.opExtrude","SWEPT_FACE",FACE,{"disambiguationData":[OSD([sQuery(id+"F2.wireOp",EDGE,"E438.MirrorC")])]})])],"derivedFrom":makeQuery(id+"F8.opSweep","SWEPT_FACE",FACE,{"disambiguationData":[OSD([sQuery(id+"F0.wireOp",EDGE,"E0"),sQuery(id+"F7.wireOp",EDGE,"E620.4")])]})});
            var Q301;
            Q301=makeQuery(id+"F8.boolean.opBoolean","COPY",FACE,{"disambiguationData":[TD([makeQuery(id+"F4.opExtrude","SWEPT_FACE",FACE,{"disambiguationData":[OSD([sQuery(id+"F2.wireOp",EDGE,"E369.MirrorC")])]})])],"derivedFrom":makeQuery(id+"F8.opSweep","SWEPT_FACE",FACE,{"disambiguationData":[OSD([sQuery(id+"F0.wireOp",EDGE,"E0"),sQuery(id+"F7.wireOp",EDGE,"E620.4")])]})});
            var Q302;
            Q302=makeQuery(id+"F8.boolean.opBoolean","COPY",FACE,{"disambiguationData":[TD([makeQuery(id+"F4.opExtrude","SWEPT_FACE",FACE,{"disambiguationData":[OSD([sQuery(id+"F2.wireOp",EDGE,"E384.MirrorC")])]})])],"derivedFrom":makeQuery(id+"F8.opSweep","SWEPT_FACE",FACE,{"disambiguationData":[OSD([sQuery(id+"F0.wireOp",EDGE,"E0"),sQuery(id+"F7.wireOp",EDGE,"E620.4")])]})});
            var Q303;
            Q303=makeQuery(id+"F8.boolean.opBoolean","COPY",FACE,{"disambiguationData":[TD([makeQuery(id+"F4.opExtrude","SWEPT_FACE",FACE,{"disambiguationData":[OSD([sQuery(id+"F2.wireOp",EDGE,"E388.MirrorC")])]})])],"derivedFrom":makeQuery(id+"F8.opSweep","SWEPT_FACE",FACE,{"disambiguationData":[OSD([sQuery(id+"F0.wireOp",EDGE,"E0"),sQuery(id+"F7.wireOp",EDGE,"E620.4")])]})});
            var Q304;
            Q304=makeQuery(id+"F8.boolean.opBoolean","COPY",FACE,{"disambiguationData":[TD([makeQuery(id+"F4.opExtrude","SWEPT_FACE",FACE,{"disambiguationData":[OSD([sQuery(id+"F2.wireOp",EDGE,"E420.MirrorC")])]})])],"derivedFrom":makeQuery(id+"F8.opSweep","SWEPT_FACE",FACE,{"disambiguationData":[OSD([sQuery(id+"F0.wireOp",EDGE,"E0"),sQuery(id+"F7.wireOp",EDGE,"E620.4")])]})});
            var Q305;
            Q305=makeQuery(id+"F8.boolean.opBoolean","COPY",FACE,{"disambiguationData":[TD([makeQuery(id+"F4.opExtrude","SWEPT_FACE",FACE,{"disambiguationData":[OSD([sQuery(id+"F2.wireOp",EDGE,"E440.MirrorC")])]})])],"derivedFrom":makeQuery(id+"F8.opSweep","SWEPT_FACE",FACE,{"disambiguationData":[OSD([sQuery(id+"F0.wireOp",EDGE,"E0"),sQuery(id+"F7.wireOp",EDGE,"E620.4")])]})});
            var Q306;
            Q306=makeQuery(id+"F8.boolean.opBoolean","COPY",FACE,{"disambiguationData":[TD([makeQuery(id+"F4.opExtrude","SWEPT_FACE",FACE,{"disambiguationData":[OSD([sQuery(id+"F2.wireOp",EDGE,"E337.MirrorC")])]})])],"derivedFrom":makeQuery(id+"F8.opSweep","SWEPT_FACE",FACE,{"disambiguationData":[OSD([sQuery(id+"F0.wireOp",EDGE,"E0"),sQuery(id+"F7.wireOp",EDGE,"E620.4")])]})});
            var Q307;
            Q307=makeQuery(id+"F8.boolean.opBoolean","COPY",FACE,{"disambiguationData":[TD([makeQuery(id+"F4.opExtrude","SWEPT_FACE",FACE,{"disambiguationData":[OSD([sQuery(id+"F2.wireOp",EDGE,"E324.MirrorC")])]})])],"derivedFrom":makeQuery(id+"F8.opSweep","SWEPT_FACE",FACE,{"disambiguationData":[OSD([sQuery(id+"F0.wireOp",EDGE,"E0"),sQuery(id+"F7.wireOp",EDGE,"E620.4")])]})});
            var Q308;
            Q308=makeQuery(id+"F8.boolean.opBoolean","COPY",FACE,{"disambiguationData":[TD([makeQuery(id+"F4.opExtrude","SWEPT_FACE",FACE,{"disambiguationData":[OSD([sQuery(id+"F2.wireOp",EDGE,"E403.MirrorC")])]})])],"derivedFrom":makeQuery(id+"F8.opSweep","SWEPT_FACE",FACE,{"disambiguationData":[OSD([sQuery(id+"F0.wireOp",EDGE,"E0"),sQuery(id+"F7.wireOp",EDGE,"E620.4")])]})});
            var Q309;
            Q309=makeQuery(id+"F8.boolean.opBoolean","COPY",FACE,{"disambiguationData":[TD([makeQuery(id+"F4.opExtrude","SWEPT_FACE",FACE,{"disambiguationData":[OSD([sQuery(id+"F2.wireOp",EDGE,"E409.MirrorC")])]})])],"derivedFrom":makeQuery(id+"F8.opSweep","SWEPT_FACE",FACE,{"disambiguationData":[OSD([sQuery(id+"F0.wireOp",EDGE,"E0"),sQuery(id+"F7.wireOp",EDGE,"E620.4")])]})});
            var Q310;
            Q310=makeQuery(id+"F8.boolean.opBoolean","COPY",FACE,{"disambiguationData":[TD([makeQuery(id+"F4.opExtrude","SWEPT_FACE",FACE,{"disambiguationData":[OSD([sQuery(id+"F2.wireOp",EDGE,"E328.MirrorC")])]})])],"derivedFrom":makeQuery(id+"F8.opSweep","SWEPT_FACE",FACE,{"disambiguationData":[OSD([sQuery(id+"F0.wireOp",EDGE,"E0"),sQuery(id+"F7.wireOp",EDGE,"E620.4")])]})});
            var Q311;
            Q311=makeQuery(id+"F8.boolean.opBoolean","COPY",FACE,{"disambiguationData":[TD([makeQuery(id+"F4.opExtrude","SWEPT_FACE",FACE,{"disambiguationData":[OSD([sQuery(id+"F2.wireOp",EDGE,"E396.MirrorC")])]})])],"derivedFrom":makeQuery(id+"F8.opSweep","SWEPT_FACE",FACE,{"disambiguationData":[OSD([sQuery(id+"F0.wireOp",EDGE,"E0"),sQuery(id+"F7.wireOp",EDGE,"E620.4")])]})});
            var Q312;
            Q312=makeQuery(id+"F8.boolean.opBoolean","COPY",FACE,{"disambiguationData":[TD([makeQuery(id+"F4.opExtrude","SWEPT_FACE",FACE,{"disambiguationData":[OSD([sQuery(id+"F2.wireOp",EDGE,"E370.MirrorC")])]})])],"derivedFrom":makeQuery(id+"F8.opSweep","SWEPT_FACE",FACE,{"disambiguationData":[OSD([sQuery(id+"F0.wireOp",EDGE,"E0"),sQuery(id+"F7.wireOp",EDGE,"E620.4")])]})});
            var Q313;
            Q313=makeQuery(id+"F8.boolean.opBoolean","COPY",FACE,{"disambiguationData":[TD([makeQuery(id+"F4.opExtrude","SWEPT_FACE",FACE,{"disambiguationData":[OSD([sQuery(id+"F2.wireOp",EDGE,"E399.MirrorC")])]})])],"derivedFrom":makeQuery(id+"F8.opSweep","SWEPT_FACE",FACE,{"disambiguationData":[OSD([sQuery(id+"F0.wireOp",EDGE,"E0"),sQuery(id+"F7.wireOp",EDGE,"E620.4")])]})});
            var Q314;
            Q314=makeQuery(id+"F8.boolean.opBoolean","COPY",FACE,{"disambiguationData":[TD([makeQuery(id+"F4.opExtrude","SWEPT_FACE",FACE,{"disambiguationData":[OSD([sQuery(id+"F2.wireOp",EDGE,"E430.MirrorC")])]})])],"derivedFrom":makeQuery(id+"F8.opSweep","SWEPT_FACE",FACE,{"disambiguationData":[OSD([sQuery(id+"F0.wireOp",EDGE,"E0"),sQuery(id+"F7.wireOp",EDGE,"E620.4")])]})});
            var Q315;
            Q315=makeQuery(id+"F8.boolean.opBoolean","COPY",FACE,{"disambiguationData":[TD([makeQuery(id+"F4.opExtrude","SWEPT_FACE",FACE,{"disambiguationData":[OSD([sQuery(id+"F2.wireOp",EDGE,"E435.MirrorC")])]})])],"derivedFrom":makeQuery(id+"F8.opSweep","SWEPT_FACE",FACE,{"disambiguationData":[OSD([sQuery(id+"F0.wireOp",EDGE,"E0"),sQuery(id+"F7.wireOp",EDGE,"E620.4")])]})});
            var Q316;
            Q316=makeQuery(id+"F8.boolean.opBoolean","COPY",FACE,{"disambiguationData":[TD([makeQuery(id+"F4.opExtrude","SWEPT_FACE",FACE,{"disambiguationData":[OSD([sQuery(id+"F2.wireOp",EDGE,"E427.MirrorC")])]})])],"derivedFrom":makeQuery(id+"F8.opSweep","SWEPT_FACE",FACE,{"disambiguationData":[OSD([sQuery(id+"F0.wireOp",EDGE,"E0"),sQuery(id+"F7.wireOp",EDGE,"E620.4")])]})});
            var Q317;
            Q317=makeQuery(id+"F8.boolean.opBoolean","COPY",FACE,{"disambiguationData":[TD([makeQuery(id+"F4.opExtrude","SWEPT_FACE",FACE,{"disambiguationData":[OSD([sQuery(id+"F2.wireOp",EDGE,"E428.MirrorC")])]})])],"derivedFrom":makeQuery(id+"F8.opSweep","SWEPT_FACE",FACE,{"disambiguationData":[OSD([sQuery(id+"F0.wireOp",EDGE,"E0"),sQuery(id+"F7.wireOp",EDGE,"E620.4")])]})});
            var Q318;
            Q318=makeQuery(id+"F8.boolean.opBoolean","COPY",FACE,{"disambiguationData":[TD([makeQuery(id+"F4.opExtrude","SWEPT_FACE",FACE,{"disambiguationData":[OSD([sQuery(id+"F2.wireOp",EDGE,"E374.MirrorC")])]})])],"derivedFrom":makeQuery(id+"F8.opSweep","SWEPT_FACE",FACE,{"disambiguationData":[OSD([sQuery(id+"F0.wireOp",EDGE,"E0"),sQuery(id+"F7.wireOp",EDGE,"E620.4")])]})});
            var Q319;
            Q319=makeQuery(id+"F8.boolean.opBoolean","COPY",FACE,{"disambiguationData":[TD([makeQuery(id+"F4.opExtrude","SWEPT_FACE",FACE,{"disambiguationData":[OSD([sQuery(id+"F2.wireOp",EDGE,"E378.MirrorC")])]})])],"derivedFrom":makeQuery(id+"F8.opSweep","SWEPT_FACE",FACE,{"disambiguationData":[OSD([sQuery(id+"F0.wireOp",EDGE,"E0"),sQuery(id+"F7.wireOp",EDGE,"E620.4")])]})});
            var Q320;
            Q320=makeQuery(id+"F8.boolean.opBoolean","COPY",FACE,{"disambiguationData":[TD([makeQuery(id+"F4.opExtrude","SWEPT_FACE",FACE,{"disambiguationData":[OSD([sQuery(id+"F2.wireOp",EDGE,"E329.MirrorC")])]})])],"derivedFrom":makeQuery(id+"F8.opSweep","SWEPT_FACE",FACE,{"disambiguationData":[OSD([sQuery(id+"F0.wireOp",EDGE,"E0"),sQuery(id+"F7.wireOp",EDGE,"E620.4")])]})});
            var Q321;
            Q321=makeQuery(id+"F8.boolean.opBoolean","COPY",FACE,{"disambiguationData":[TD([makeQuery(id+"F4.opExtrude","SWEPT_FACE",FACE,{"disambiguationData":[OSD([sQuery(id+"F2.wireOp",EDGE,"E377.MirrorC")])]})])],"derivedFrom":makeQuery(id+"F8.opSweep","SWEPT_FACE",FACE,{"disambiguationData":[OSD([sQuery(id+"F0.wireOp",EDGE,"E0"),sQuery(id+"F7.wireOp",EDGE,"E620.4")])]})});
            var Q322;
            Q322=makeQuery(id+"F8.boolean.opBoolean","COPY",FACE,{"disambiguationData":[TD([makeQuery(id+"F4.opExtrude","SWEPT_FACE",FACE,{"disambiguationData":[OSD([sQuery(id+"F2.wireOp",EDGE,"E432.MirrorC")])]})])],"derivedFrom":makeQuery(id+"F8.opSweep","SWEPT_FACE",FACE,{"disambiguationData":[OSD([sQuery(id+"F0.wireOp",EDGE,"E0"),sQuery(id+"F7.wireOp",EDGE,"E620.4")])]})});
            var Q323;
            Q323=makeQuery(id+"F8.boolean.opBoolean","COPY",FACE,{"disambiguationData":[TD([makeQuery(id+"F4.opExtrude","SWEPT_FACE",FACE,{"disambiguationData":[OSD([sQuery(id+"F2.wireOp",EDGE,"E341.MirrorC")])]})])],"derivedFrom":makeQuery(id+"F8.opSweep","SWEPT_FACE",FACE,{"disambiguationData":[OSD([sQuery(id+"F0.wireOp",EDGE,"E0"),sQuery(id+"F7.wireOp",EDGE,"E620.4")])]})});
            var Q324;
            Q324=makeQuery(id+"F8.boolean.opBoolean","COPY",FACE,{"disambiguationData":[TD([makeQuery(id+"F4.opExtrude","SWEPT_FACE",FACE,{"disambiguationData":[OSD([sQuery(id+"F2.wireOp",EDGE,"E365.MirrorC")])]})])],"derivedFrom":makeQuery(id+"F8.opSweep","SWEPT_FACE",FACE,{"disambiguationData":[OSD([sQuery(id+"F0.wireOp",EDGE,"E0"),sQuery(id+"F7.wireOp",EDGE,"E620.4")])]})});
            var Q325;
            Q325=makeQuery(id+"F8.boolean.opBoolean","COPY",FACE,{"disambiguationData":[TD([makeQuery(id+"F4.opExtrude","SWEPT_FACE",FACE,{"disambiguationData":[OSD([sQuery(id+"F2.wireOp",EDGE,"E433.MirrorC")])]})])],"derivedFrom":makeQuery(id+"F8.opSweep","SWEPT_FACE",FACE,{"disambiguationData":[OSD([sQuery(id+"F0.wireOp",EDGE,"E0"),sQuery(id+"F7.wireOp",EDGE,"E620.4")])]})});
            var Q326;
            Q326=makeQuery(id+"F8.boolean.opBoolean","COPY",FACE,{"disambiguationData":[TD([makeQuery(id+"F4.opExtrude","SWEPT_FACE",FACE,{"disambiguationData":[OSD([sQuery(id+"F2.wireOp",EDGE,"E327.MirrorC")])]})])],"derivedFrom":makeQuery(id+"F8.opSweep","SWEPT_FACE",FACE,{"disambiguationData":[OSD([sQuery(id+"F0.wireOp",EDGE,"E0"),sQuery(id+"F7.wireOp",EDGE,"E620.4")])]})});
            var Q327;
            Q327=makeQuery(id+"F8.boolean.opBoolean","COPY",FACE,{"disambiguationData":[TD([makeQuery(id+"F4.opExtrude","SWEPT_FACE",FACE,{"disambiguationData":[OSD([sQuery(id+"F2.wireOp",EDGE,"E408.MirrorC")])]})])],"derivedFrom":makeQuery(id+"F8.opSweep","SWEPT_FACE",FACE,{"disambiguationData":[OSD([sQuery(id+"F0.wireOp",EDGE,"E0"),sQuery(id+"F7.wireOp",EDGE,"E620.4")])]})});
            var Q328;
            Q328=makeQuery(id+"F8.boolean.opBoolean","COPY",FACE,{"disambiguationData":[TD([makeQuery(id+"F4.opExtrude","SWEPT_FACE",FACE,{"disambiguationData":[OSD([sQuery(id+"F2.wireOp",EDGE,"E528.MirrorC")])]})])],"derivedFrom":makeQuery(id+"F8.opSweep","SWEPT_FACE",FACE,{"disambiguationData":[OSD([sQuery(id+"F0.wireOp",EDGE,"E0"),sQuery(id+"F7.wireOp",EDGE,"E620.5")])]})});
            var Q329;
            Q329=makeQuery(id+"F8.boolean.opBoolean","COPY",FACE,{"disambiguationData":[TD([makeQuery(id+"F4.opExtrude","SWEPT_FACE",FACE,{"disambiguationData":[OSD([sQuery(id+"F2.wireOp",EDGE,"E473.MirrorC")])]})])],"derivedFrom":makeQuery(id+"F8.opSweep","SWEPT_FACE",FACE,{"disambiguationData":[OSD([sQuery(id+"F0.wireOp",EDGE,"E0"),sQuery(id+"F7.wireOp",EDGE,"E620.5")])]})});
            var Q330;
            Q330=makeQuery(id+"F8.boolean.opBoolean","COPY",FACE,{"disambiguationData":[TD([makeQuery(id+"F4.opExtrude","SWEPT_FACE",FACE,{"disambiguationData":[OSD([sQuery(id+"F2.wireOp",EDGE,"E456.MirrorC")])]})])],"derivedFrom":makeQuery(id+"F8.opSweep","SWEPT_FACE",FACE,{"disambiguationData":[OSD([sQuery(id+"F0.wireOp",EDGE,"E0"),sQuery(id+"F7.wireOp",EDGE,"E620.5")])]})});
            var Q331;
            Q331=makeQuery(id+"F8.boolean.opBoolean","COPY",FACE,{"disambiguationData":[TD([makeQuery(id+"F4.opExtrude","SWEPT_FACE",FACE,{"disambiguationData":[OSD([sQuery(id+"F2.wireOp",EDGE,"E325.MirrorC")])]})])],"derivedFrom":makeQuery(id+"F8.opSweep","SWEPT_FACE",FACE,{"disambiguationData":[OSD([sQuery(id+"F0.wireOp",EDGE,"E0"),sQuery(id+"F7.wireOp",EDGE,"E620.5")])]})});
            var Q332;
            Q332=makeQuery(id+"F8.boolean.opBoolean","COPY",FACE,{"disambiguationData":[TD([makeQuery(id+"F4.opExtrude","SWEPT_FACE",FACE,{"disambiguationData":[OSD([sQuery(id+"F2.wireOp",EDGE,"E453.MirrorC")])]})])],"derivedFrom":makeQuery(id+"F8.opSweep","SWEPT_FACE",FACE,{"disambiguationData":[OSD([sQuery(id+"F0.wireOp",EDGE,"E0"),sQuery(id+"F7.wireOp",EDGE,"E620.5")])]})});
            var Q333;
            Q333=makeQuery(id+"F8.boolean.opBoolean","COPY",FACE,{"disambiguationData":[TD([makeQuery(id+"F4.opExtrude","SWEPT_FACE",FACE,{"disambiguationData":[OSD([sQuery(id+"F2.wireOp",EDGE,"E461.MirrorC")])]})])],"derivedFrom":makeQuery(id+"F8.opSweep","SWEPT_FACE",FACE,{"disambiguationData":[OSD([sQuery(id+"F0.wireOp",EDGE,"E0"),sQuery(id+"F7.wireOp",EDGE,"E620.5")])]})});
            var Q334;
            Q334=makeQuery(id+"F8.boolean.opBoolean","COPY",FACE,{"disambiguationData":[TD([makeQuery(id+"F4.opExtrude","SWEPT_FACE",FACE,{"disambiguationData":[OSD([sQuery(id+"F2.wireOp",EDGE,"E468.MirrorC")])]})])],"derivedFrom":makeQuery(id+"F8.opSweep","SWEPT_FACE",FACE,{"disambiguationData":[OSD([sQuery(id+"F0.wireOp",EDGE,"E0"),sQuery(id+"F7.wireOp",EDGE,"E620.5")])]})});
            var Q335;
            Q335=makeQuery(id+"F8.boolean.opBoolean","COPY",FACE,{"disambiguationData":[TD([makeQuery(id+"F4.opExtrude","SWEPT_FACE",FACE,{"disambiguationData":[OSD([sQuery(id+"F2.wireOp",EDGE,"E481.MirrorC")])]})])],"derivedFrom":makeQuery(id+"F8.opSweep","SWEPT_FACE",FACE,{"disambiguationData":[OSD([sQuery(id+"F0.wireOp",EDGE,"E0"),sQuery(id+"F7.wireOp",EDGE,"E620.5")])]})});
            var Q336;
            Q336=makeQuery(id+"F8.boolean.opBoolean","COPY",FACE,{"disambiguationData":[TD([makeQuery(id+"F4.opExtrude","SWEPT_FACE",FACE,{"disambiguationData":[OSD([sQuery(id+"F2.wireOp",EDGE,"E467.MirrorC")])]})])],"derivedFrom":makeQuery(id+"F8.opSweep","SWEPT_FACE",FACE,{"disambiguationData":[OSD([sQuery(id+"F0.wireOp",EDGE,"E0"),sQuery(id+"F7.wireOp",EDGE,"E620.5")])]})});
            var Q337;
            Q337=makeQuery(id+"F8.boolean.opBoolean","COPY",FACE,{"disambiguationData":[TD([makeQuery(id+"F4.opExtrude","SWEPT_FACE",FACE,{"disambiguationData":[OSD([sQuery(id+"F2.wireOp",EDGE,"E471.MirrorC")])]})])],"derivedFrom":makeQuery(id+"F8.opSweep","SWEPT_FACE",FACE,{"disambiguationData":[OSD([sQuery(id+"F0.wireOp",EDGE,"E0"),sQuery(id+"F7.wireOp",EDGE,"E620.5")])]})});
            var Q338;
            Q338=makeQuery(id+"F8.boolean.opBoolean","COPY",FACE,{"disambiguationData":[TD([makeQuery(id+"F4.opExtrude","SWEPT_FACE",FACE,{"disambiguationData":[OSD([sQuery(id+"F2.wireOp",EDGE,"E506.MirrorC")])]})])],"derivedFrom":makeQuery(id+"F8.opSweep","SWEPT_FACE",FACE,{"disambiguationData":[OSD([sQuery(id+"F0.wireOp",EDGE,"E0"),sQuery(id+"F7.wireOp",EDGE,"E620.5")])]})});
            var Q339;
            Q339=makeQuery(id+"F8.boolean.opBoolean","COPY",FACE,{"disambiguationData":[TD([makeQuery(id+"F4.opExtrude","SWEPT_FACE",FACE,{"disambiguationData":[OSD([sQuery(id+"F2.wireOp",EDGE,"E521.MirrorC")])]})])],"derivedFrom":makeQuery(id+"F8.opSweep","SWEPT_FACE",FACE,{"disambiguationData":[OSD([sQuery(id+"F0.wireOp",EDGE,"E0"),sQuery(id+"F7.wireOp",EDGE,"E620.5")])]})});
            var Q340;
            Q340=makeQuery(id+"F8.boolean.opBoolean","COPY",FACE,{"disambiguationData":[TD([makeQuery(id+"F4.opExtrude","SWEPT_FACE",FACE,{"disambiguationData":[OSD([sQuery(id+"F2.wireOp",EDGE,"E530.MirrorC")])]})])],"derivedFrom":makeQuery(id+"F8.opSweep","SWEPT_FACE",FACE,{"disambiguationData":[OSD([sQuery(id+"F0.wireOp",EDGE,"E0"),sQuery(id+"F7.wireOp",EDGE,"E620.5")])]})});
            var Q341;
            Q341=makeQuery(id+"F8.boolean.opBoolean","COPY",FACE,{"disambiguationData":[TD([makeQuery(id+"F4.opExtrude","SWEPT_FACE",FACE,{"disambiguationData":[OSD([sQuery(id+"F2.wireOp",EDGE,"E502.MirrorC")])]})])],"derivedFrom":makeQuery(id+"F8.opSweep","SWEPT_FACE",FACE,{"disambiguationData":[OSD([sQuery(id+"F0.wireOp",EDGE,"E0"),sQuery(id+"F7.wireOp",EDGE,"E620.5")])]})});
            var Q342;
            Q342=makeQuery(id+"F8.boolean.opBoolean","COPY",FACE,{"disambiguationData":[TD([makeQuery(id+"F4.opExtrude","SWEPT_FACE",FACE,{"disambiguationData":[OSD([sQuery(id+"F2.wireOp",EDGE,"E555.MirrorC")])]})])],"derivedFrom":makeQuery(id+"F8.opSweep","SWEPT_FACE",FACE,{"disambiguationData":[OSD([sQuery(id+"F0.wireOp",EDGE,"E0"),sQuery(id+"F7.wireOp",EDGE,"E620.5")])]})});
            var Q343;
            Q343=makeQuery(id+"F8.boolean.opBoolean","COPY",FACE,{"disambiguationData":[TD([makeQuery(id+"F4.opExtrude","SWEPT_FACE",FACE,{"disambiguationData":[OSD([sQuery(id+"F2.wireOp",EDGE,"E449.MirrorC")])]})])],"derivedFrom":makeQuery(id+"F8.opSweep","SWEPT_FACE",FACE,{"disambiguationData":[OSD([sQuery(id+"F0.wireOp",EDGE,"E0"),sQuery(id+"F7.wireOp",EDGE,"E620.5")])]})});
            var Q344;
            Q344=makeQuery(id+"F8.boolean.opBoolean","COPY",FACE,{"disambiguationData":[TD([makeQuery(id+"F4.opExtrude","SWEPT_FACE",FACE,{"disambiguationData":[OSD([sQuery(id+"F2.wireOp",EDGE,"E527.MirrorC")])]})])],"derivedFrom":makeQuery(id+"F8.opSweep","SWEPT_FACE",FACE,{"disambiguationData":[OSD([sQuery(id+"F0.wireOp",EDGE,"E0"),sQuery(id+"F7.wireOp",EDGE,"E620.5")])]})});
            var Q345;
            Q345=makeQuery(id+"F8.boolean.opBoolean","COPY",FACE,{"disambiguationData":[TD([makeQuery(id+"F4.opExtrude","SWEPT_FACE",FACE,{"disambiguationData":[OSD([sQuery(id+"F2.wireOp",EDGE,"E491.MirrorC")])]})])],"derivedFrom":makeQuery(id+"F8.opSweep","SWEPT_FACE",FACE,{"disambiguationData":[OSD([sQuery(id+"F0.wireOp",EDGE,"E0"),sQuery(id+"F7.wireOp",EDGE,"E620.5")])]})});
            var Q346;
            Q346=makeQuery(id+"F8.boolean.opBoolean","COPY",FACE,{"disambiguationData":[TD([makeQuery(id+"F4.opExtrude","SWEPT_FACE",FACE,{"disambiguationData":[OSD([sQuery(id+"F2.wireOp",EDGE,"E444.MirrorC")])]})])],"derivedFrom":makeQuery(id+"F8.opSweep","SWEPT_FACE",FACE,{"disambiguationData":[OSD([sQuery(id+"F0.wireOp",EDGE,"E0"),sQuery(id+"F7.wireOp",EDGE,"E620.5")])]})});
            var Q347;
            Q347=makeQuery(id+"F8.boolean.opBoolean","COPY",FACE,{"disambiguationData":[TD([makeQuery(id+"F4.opExtrude","SWEPT_FACE",FACE,{"disambiguationData":[OSD([sQuery(id+"F2.wireOp",EDGE,"E496.MirrorC")])]})])],"derivedFrom":makeQuery(id+"F8.opSweep","SWEPT_FACE",FACE,{"disambiguationData":[OSD([sQuery(id+"F0.wireOp",EDGE,"E0"),sQuery(id+"F7.wireOp",EDGE,"E620.5")])]})});
            var Q348;
            Q348=makeQuery(id+"F8.boolean.opBoolean","COPY",FACE,{"disambiguationData":[TD([makeQuery(id+"F4.opExtrude","SWEPT_FACE",FACE,{"disambiguationData":[OSD([sQuery(id+"F2.wireOp",EDGE,"E536.MirrorC")])]})])],"derivedFrom":makeQuery(id+"F8.opSweep","SWEPT_FACE",FACE,{"disambiguationData":[OSD([sQuery(id+"F0.wireOp",EDGE,"E0"),sQuery(id+"F7.wireOp",EDGE,"E620.5")])]})});
            var Q349;
            Q349=makeQuery(id+"F8.boolean.opBoolean","COPY",FACE,{"disambiguationData":[TD([makeQuery(id+"F4.opExtrude","SWEPT_FACE",FACE,{"disambiguationData":[OSD([sQuery(id+"F2.wireOp",EDGE,"E460.MirrorC")])]})])],"derivedFrom":makeQuery(id+"F8.opSweep","SWEPT_FACE",FACE,{"disambiguationData":[OSD([sQuery(id+"F0.wireOp",EDGE,"E0"),sQuery(id+"F7.wireOp",EDGE,"E620.5")])]})});
            var Q350;
            Q350=makeQuery(id+"F8.boolean.opBoolean","COPY",FACE,{"disambiguationData":[TD([makeQuery(id+"F4.opExtrude","SWEPT_FACE",FACE,{"disambiguationData":[OSD([sQuery(id+"F2.wireOp",EDGE,"E511.MirrorC")])]})])],"derivedFrom":makeQuery(id+"F8.opSweep","SWEPT_FACE",FACE,{"disambiguationData":[OSD([sQuery(id+"F0.wireOp",EDGE,"E0"),sQuery(id+"F7.wireOp",EDGE,"E620.5")])]})});
            var Q351;
            Q351=makeQuery(id+"F8.boolean.opBoolean","COPY",FACE,{"disambiguationData":[TD([makeQuery(id+"F4.opExtrude","SWEPT_FACE",FACE,{"disambiguationData":[OSD([sQuery(id+"F2.wireOp",EDGE,"E553.MirrorC")])]})])],"derivedFrom":makeQuery(id+"F8.opSweep","SWEPT_FACE",FACE,{"disambiguationData":[OSD([sQuery(id+"F0.wireOp",EDGE,"E0"),sQuery(id+"F7.wireOp",EDGE,"E620.5")])]})});
            var Q352;
            Q352=makeQuery(id+"F8.boolean.opBoolean","COPY",FACE,{"disambiguationData":[TD([makeQuery(id+"F4.opExtrude","SWEPT_FACE",FACE,{"disambiguationData":[OSD([sQuery(id+"F2.wireOp",EDGE,"E550.MirrorC")])]})])],"derivedFrom":makeQuery(id+"F8.opSweep","SWEPT_FACE",FACE,{"disambiguationData":[OSD([sQuery(id+"F0.wireOp",EDGE,"E0"),sQuery(id+"F7.wireOp",EDGE,"E620.5")])]})});
            var Q353;
            Q353=makeQuery(id+"F8.boolean.opBoolean","COPY",FACE,{"disambiguationData":[TD([makeQuery(id+"F4.opExtrude","SWEPT_FACE",FACE,{"disambiguationData":[OSD([sQuery(id+"F2.wireOp",EDGE,"E516.MirrorC")])]})])],"derivedFrom":makeQuery(id+"F8.opSweep","SWEPT_FACE",FACE,{"disambiguationData":[OSD([sQuery(id+"F0.wireOp",EDGE,"E0"),sQuery(id+"F7.wireOp",EDGE,"E620.5")])]})});
            var Q354;
            Q354=makeQuery(id+"F8.boolean.opBoolean","COPY",FACE,{"disambiguationData":[TD([makeQuery(id+"F4.opExtrude","SWEPT_FACE",FACE,{"disambiguationData":[OSD([sQuery(id+"F2.wireOp",EDGE,"E389.MirrorC")])]})])],"derivedFrom":makeQuery(id+"F8.opSweep","SWEPT_FACE",FACE,{"disambiguationData":[OSD([sQuery(id+"F0.wireOp",EDGE,"E0"),sQuery(id+"F7.wireOp",EDGE,"E620.4")])]})});
            var Q355;
            Q355=makeQuery(id+"F8.boolean.opBoolean","COPY",FACE,{"disambiguationData":[TD([makeQuery(id+"F4.opExtrude","SWEPT_FACE",FACE,{"disambiguationData":[OSD([sQuery(id+"F2.wireOp",EDGE,"E429.MirrorC")])]})])],"derivedFrom":makeQuery(id+"F8.opSweep","SWEPT_FACE",FACE,{"disambiguationData":[OSD([sQuery(id+"F0.wireOp",EDGE,"E0"),sQuery(id+"F7.wireOp",EDGE,"E620.4")])]})});
            var Q356;
            Q356=makeQuery(id+"F8.boolean.opBoolean","COPY",FACE,{"disambiguationData":[TD([makeQuery(id+"F4.opExtrude","SWEPT_FACE",FACE,{"disambiguationData":[OSD([sQuery(id+"F2.wireOp",EDGE,"E436.MirrorC")])]})])],"derivedFrom":makeQuery(id+"F8.opSweep","SWEPT_FACE",FACE,{"disambiguationData":[OSD([sQuery(id+"F0.wireOp",EDGE,"E0"),sQuery(id+"F7.wireOp",EDGE,"E620.4")])]})});
            var Q357;
            Q357=makeQuery(id+"F8.boolean.opBoolean","COPY",FACE,{"disambiguationData":[TD([makeQuery(id+"F4.opExtrude","SWEPT_FACE",FACE,{"disambiguationData":[OSD([sQuery(id+"F2.wireOp",EDGE,"E424.MirrorC")])]})])],"derivedFrom":makeQuery(id+"F8.opSweep","SWEPT_FACE",FACE,{"disambiguationData":[OSD([sQuery(id+"F0.wireOp",EDGE,"E0"),sQuery(id+"F7.wireOp",EDGE,"E620.4")])]})});
            var Q358;
            Q358=makeQuery(id+"F8.boolean.opBoolean","COPY",FACE,{"disambiguationData":[TD([makeQuery(id+"F4.opExtrude","SWEPT_FACE",FACE,{"disambiguationData":[OSD([sQuery(id+"F2.wireOp",EDGE,"E364.MirrorC")])]})])],"derivedFrom":makeQuery(id+"F8.opSweep","SWEPT_FACE",FACE,{"disambiguationData":[OSD([sQuery(id+"F0.wireOp",EDGE,"E0"),sQuery(id+"F7.wireOp",EDGE,"E620.4")])]})});
            var Q359;
            Q359=makeQuery(id+"F8.boolean.opBoolean","COPY",FACE,{"disambiguationData":[TD([makeQuery(id+"F4.opExtrude","SWEPT_FACE",FACE,{"disambiguationData":[OSD([sQuery(id+"F2.wireOp",EDGE,"E353.MirrorC")])]})])],"derivedFrom":makeQuery(id+"F8.opSweep","SWEPT_FACE",FACE,{"disambiguationData":[OSD([sQuery(id+"F0.wireOp",EDGE,"E0"),sQuery(id+"F7.wireOp",EDGE,"E620.4")])]})});
            var Q360;
            Q360=makeQuery(id+"F8.boolean.opBoolean","COPY",FACE,{"disambiguationData":[TD([makeQuery(id+"F4.opExtrude","SWEPT_FACE",FACE,{"disambiguationData":[OSD([sQuery(id+"F2.wireOp",EDGE,"E340.MirrorC")])]})])],"derivedFrom":makeQuery(id+"F8.opSweep","SWEPT_FACE",FACE,{"disambiguationData":[OSD([sQuery(id+"F0.wireOp",EDGE,"E0"),sQuery(id+"F7.wireOp",EDGE,"E620.4")])]})});
            var Q361;
            Q361=makeQuery(id+"F8.boolean.opBoolean","COPY",FACE,{"disambiguationData":[TD([makeQuery(id+"F4.opExtrude","SWEPT_FACE",FACE,{"disambiguationData":[OSD([sQuery(id+"F2.wireOp",EDGE,"E346.MirrorC")])]})])],"derivedFrom":makeQuery(id+"F8.opSweep","SWEPT_FACE",FACE,{"disambiguationData":[OSD([sQuery(id+"F0.wireOp",EDGE,"E0"),sQuery(id+"F7.wireOp",EDGE,"E620.4")])]})});
            var Q362;
            Q362=makeQuery(id+"F8.boolean.opBoolean","COPY",FACE,{"disambiguationData":[TD([makeQuery(id+"F4.opExtrude","SWEPT_FACE",FACE,{"disambiguationData":[OSD([sQuery(id+"F2.wireOp",EDGE,"E382.MirrorC")])]})])],"derivedFrom":makeQuery(id+"F8.opSweep","SWEPT_FACE",FACE,{"disambiguationData":[OSD([sQuery(id+"F0.wireOp",EDGE,"E0"),sQuery(id+"F7.wireOp",EDGE,"E620.4")])]})});
            fillet(context, id + "F11", {"entities" : qUnion([Q0, Q1, Q2, Q3, Q4, Q5, Q6, Q7, Q8, Q9, Q10, Q11, Q12, Q13, Q14, Q15, Q16, Q17, Q18, Q19, Q20, Q21, Q22, Q23, Q24, Q25, Q26, Q27, Q28, Q29, Q30, Q31, Q32, Q33, Q34, Q35, Q36, Q37, Q38, Q39, Q40, Q41, Q42, Q43, Q44, Q45, Q46, Q47, Q48, Q49, Q50, Q51, Q52, Q53, Q54, Q55, Q56, Q57, Q58, Q59, Q60, Q61, Q62, Q63, Q64, Q65, Q66, Q67, Q68, Q69, Q70, Q71, Q72, Q73, Q74, Q75, Q76, Q77, Q78, Q79, Q80, Q81, Q82, Q83, Q84, Q85, Q86, Q87, Q88, Q89, Q90, Q91, Q92, Q93, Q94, Q95, Q96, Q97, Q98, Q99, Q100, Q101, Q102, Q103, Q104, Q105, Q106, Q107, Q108, Q109, Q110, Q111, Q112, Q113, Q114, Q115, Q116, Q117, Q118, Q119, Q120, Q121, Q122, Q123, Q124, Q125, Q126, Q127, Q128, Q129, Q130, Q131, Q132, Q133, Q134, Q135, Q136, Q137, Q138, Q139, Q140, Q141, Q142, Q143, Q144, Q145, Q146, Q147, Q148, Q149, Q150, Q151, Q152, Q153, Q154, Q155, Q156, Q157, Q158, Q159, Q160, Q161, Q162, Q163, Q164, Q165, Q166, Q167, Q168, Q169, Q170, Q171, Q172, Q173, Q174, Q175, Q176, Q177, Q178, Q179, Q180, Q181, Q182, Q183, Q184, Q185, Q186, Q187, Q188, Q189, Q190, Q191, Q192, Q193, Q194, Q195, Q196, Q197, Q198, Q199, Q200, Q201, Q202, Q203, Q204, Q205, Q206, Q207, Q208, Q209, Q210, Q211, Q212, Q213, Q214, Q215, Q216, Q217, Q218, Q219, Q220, Q221, Q222, Q223, Q224, Q225, Q226, Q227, Q228, Q229, Q230, Q231, Q232, Q233, Q234, Q235, Q236, Q237, Q238, Q239, Q240, Q241, Q242, Q243, Q244, Q245, Q246, Q247, Q248, Q249, Q250, Q251, Q252, Q253, Q254, Q255, Q256, Q257, Q258, Q259, Q260, Q261, Q262, Q263, Q264, Q265, Q266, Q267, Q268, Q269, Q270, Q271, Q272, Q273, Q274, Q275, Q276, Q277, Q278, Q279, Q280, Q281, Q282, Q283, Q284, Q285, Q286, Q287, Q288, Q289, Q290, Q291, Q292, Q293, Q294, Q295, Q296, Q297, Q298, Q299, Q300, Q301, Q302, Q303, Q304, Q305, Q306, Q307, Q308, Q309, Q310, Q311, Q312, Q313, Q314, Q315, Q316, Q317, Q318, Q319, Q320, Q321, Q322, Q323, Q324, Q325, Q326, Q327, Q328, Q329, Q330, Q331, Q332, Q333, Q334, Q335, Q336, Q337, Q338, Q339, Q340, Q341, Q342, Q343, Q344, Q345, Q346, Q347, Q348, Q349, Q350, Q351, Q352, Q353, Q354, Q355, Q356, Q357, Q358, Q359, Q360, Q361, Q362]), "radius" : 0.3 * mm, "tangentPropagation" : true, "allowEdgeOverflow" : false});
        }
        {
            var Q0;
            Q0 = qSketchRegion(id + "F1", true);
            var Q1;
            Q1=sQuery(id+"F0.wireOp",EDGE,"E0");
            sweep(context, id + "F12", {"profiles" : qUnion([Q0]), "path" : qUnion([Q1])});
        }
        {
            var Q0;
            Q0=makeQuery(id+"F8.boolean.opBoolean","SPLIT",BODY,{"disambiguationData":[OD(0.0)],"derivedFrom":makeQuery(id+"F4.opExtrude","SWEPT_BODY",BODY,{"disambiguationData":[OSD([sQuery(id+"F2.wireOp",EDGE,"E25")])]})});
            var Q1;
            Q1=makeQuery(id+"F12.opSweep","SWEPT_BODY",BODY,{"disambiguationData":[OSD([sQuery(id+"F0.wireOp",EDGE,"E0"),sQuery(id+"F1.wireOp",EDGE,"E5"),sQuery(id+"F1.wireOp",EDGE,"E6"),sQuery(id+"F1.wireOp",EDGE,"E7"),sQuery(id+"F1.wireOp",EDGE,"E8.0"),sQuery(id+"F1.wireOp",EDGE,"E8.1"),sQuery(id+"F1.wireOp",EDGE,"E10")])]});
            booleanBodies(context, id + "F13", {"operationType" : BooleanOperationType.SUBTRACTION, "tools" : qUnion([Q0]), "targets" : qUnion([Q1])});
        }
    });
